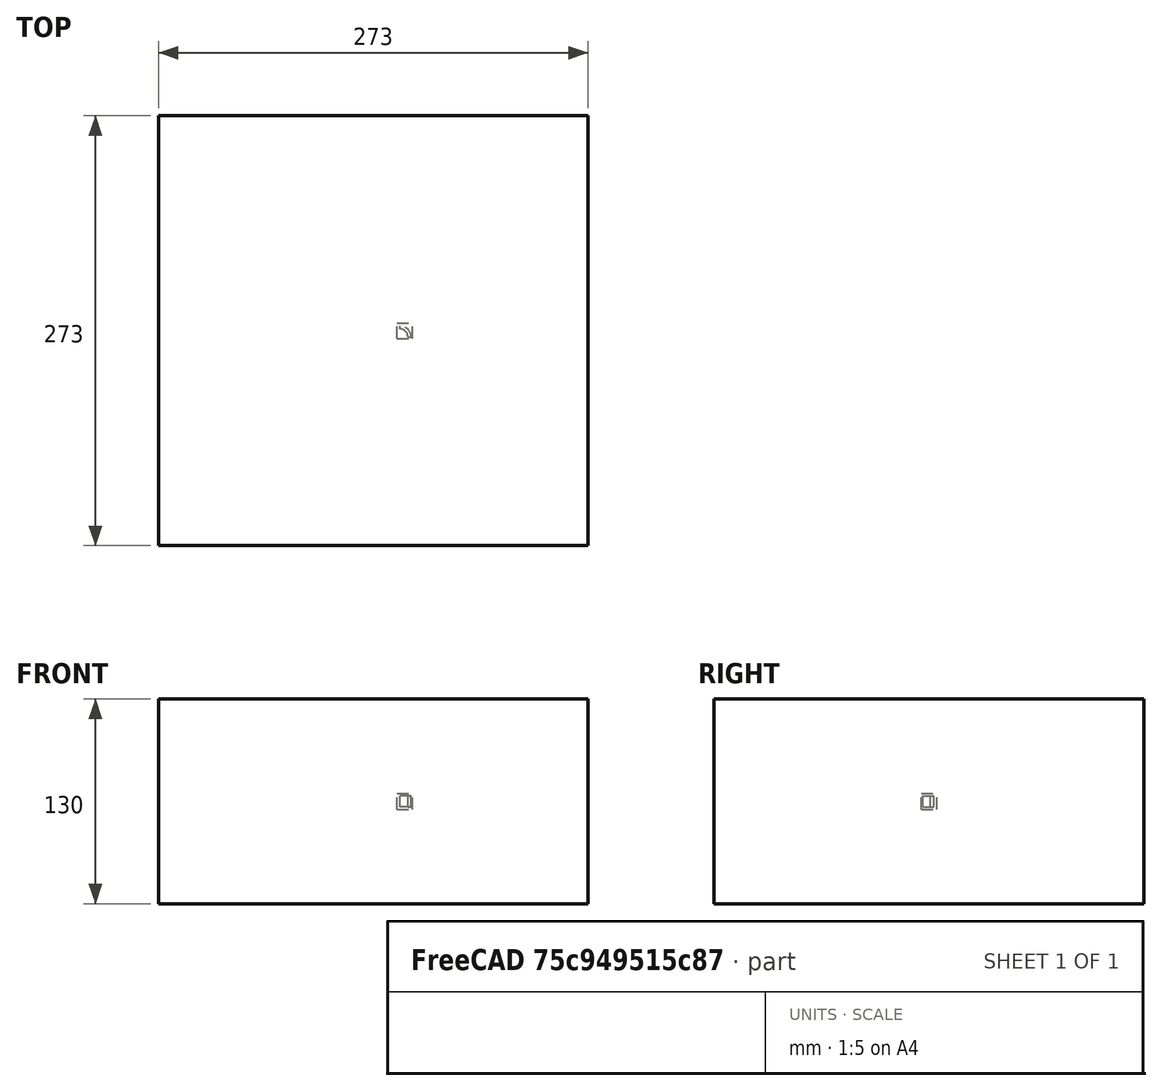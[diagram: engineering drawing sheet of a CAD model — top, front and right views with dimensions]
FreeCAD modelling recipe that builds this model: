
FCSTD DOCUMENT  (FreeCAD 0.20RUnknown)
Label: polarArray-container-d
License: All rights reserved
LicenseURL: http://en.wikipedia.org/wiki/All_rights_reserved
objects: App::DocumentObjectGroupPython×1251, Part::FeaturePython×4, App::Part×4
note: 3 computed .brp shape members not serialized (recipe doc carries the construction recipe); baked Part::Feature solids carry a one-line shape summary decoded from their .brp

FEATURE [App::DocumentObjectGroupPython] HALFPI  # scripted group (container) (typed FeaturePython)
  name = HALFPI
  value = pi/2.
FEATURE [App::DocumentObjectGroupPython] PI  # scripted group (container) (typed FeaturePython)
  name = PI
  value = 1.*pi
FEATURE [App::DocumentObjectGroupPython] TWOPI  # scripted group (container) (typed FeaturePython)
  name = TWOPI
  value = 2.*pi
FEATURE [App::DocumentObjectGroupPython] Constants  # scripted group (container) (typed FeaturePython)
  Group = -> [HALFPI,PI,TWOPI]
FEATURE [App::DocumentObjectGroupPython] Variables  # scripted group (container) (typed FeaturePython)
FEATURE [App::DocumentObjectGroupPython] Quantities  # scripted group (container) (typed FeaturePython)
FEATURE [App::DocumentObjectGroupPython] Isotopes  # scripted group (container) (typed FeaturePython)
FEATURE [App::DocumentObjectGroupPython] Elements  # scripted group (container) (typed FeaturePython)
FEATURE [App::DocumentObjectGroupPython] Matrix  # scripted group (container) (typed FeaturePython)
FEATURE [App::DocumentObjectGroupPython] Surfaces  # scripted group (container) (typed FeaturePython)
FEATURE [App::DocumentObjectGroupPython] Opticals  # scripted group (container) (typed FeaturePython)
  Group = -> [Matrix,Surfaces]
FEATURE [App::DocumentObjectGroupPython] G4Isotopes  # scripted group (container) (typed FeaturePython)
FEATURE [App::DocumentObjectGroupPython] H_element  # scripted group (container) (typed FeaturePython)
  Z = 1
  atom_value = 1.008
  formula = H
  name = H_element
FEATURE [App::DocumentObjectGroupPython] He_element  # scripted group (container) (typed FeaturePython)
  Z = 2
  atom_value = 4.0026
  formula = He
  name = He_element
FEATURE [App::DocumentObjectGroupPython] Li_element  # scripted group (container) (typed FeaturePython)
  Z = 3
  atom_value = 6.94
  formula = Li
  name = Li_element
FEATURE [App::DocumentObjectGroupPython] Be_element  # scripted group (container) (typed FeaturePython)
  Z = 4
  atom_value = 9.01218
  formula = Be
  name = Be_element
FEATURE [App::DocumentObjectGroupPython] B_element  # scripted group (container) (typed FeaturePython)
  Z = 5
  atom_value = 10.81
  formula = B
  name = B_element
FEATURE [App::DocumentObjectGroupPython] C_element  # scripted group (container) (typed FeaturePython)
  Z = 6
  atom_value = 12.011
  formula = C
  name = C_element
FEATURE [App::DocumentObjectGroupPython] N_element  # scripted group (container) (typed FeaturePython)
  Z = 7
  atom_value = 14.007
  formula = N
  name = N_element
FEATURE [App::DocumentObjectGroupPython] O_element  # scripted group (container) (typed FeaturePython)
  Z = 8
  atom_value = 15.999
  formula = O
  name = O_element
FEATURE [App::DocumentObjectGroupPython] F_element  # scripted group (container) (typed FeaturePython)
  Z = 9
  atom_value = 18.9984
  formula = F
  name = F_element
FEATURE [App::DocumentObjectGroupPython] Ne_element  # scripted group (container) (typed FeaturePython)
  Z = 10
  atom_value = 20.1797
  formula = Ne
  name = Ne_element
FEATURE [App::DocumentObjectGroupPython] Na_element  # scripted group (container) (typed FeaturePython)
  Z = 11
  atom_value = 22.9898
  formula = Na
  name = Na_element
FEATURE [App::DocumentObjectGroupPython] Mg_element  # scripted group (container) (typed FeaturePython)
  Z = 12
  atom_value = 24.305
  formula = Mg
  name = Mg_element
FEATURE [App::DocumentObjectGroupPython] Al_element  # scripted group (container) (typed FeaturePython)
  Z = 13
  atom_value = 26.9815
  formula = Al
  name = Al_element
FEATURE [App::DocumentObjectGroupPython] Si_element  # scripted group (container) (typed FeaturePython)
  Z = 14
  atom_value = 28.085
  formula = Si
  name = Si_element
FEATURE [App::DocumentObjectGroupPython] P_element  # scripted group (container) (typed FeaturePython)
  Z = 15
  atom_value = 30.9738
  formula = P
  name = P_element
FEATURE [App::DocumentObjectGroupPython] S_element  # scripted group (container) (typed FeaturePython)
  Z = 16
  atom_value = 32.06
  formula = S
  name = S_element
FEATURE [App::DocumentObjectGroupPython] Cl_element  # scripted group (container) (typed FeaturePython)
  Z = 17
  atom_value = 35.45
  formula = Cl
  name = Cl_element
FEATURE [App::DocumentObjectGroupPython] Ar_element  # scripted group (container) (typed FeaturePython)
  Z = 18
  atom_value = 39.95
  formula = Ar
  name = Ar_element
FEATURE [App::DocumentObjectGroupPython] K_element  # scripted group (container) (typed FeaturePython)
  Z = 19
  atom_value = 39.0983
  formula = K
  name = K_element
FEATURE [App::DocumentObjectGroupPython] Ca_element  # scripted group (container) (typed FeaturePython)
  Z = 20
  atom_value = 40.078
  formula = Ca
  name = Ca_element
FEATURE [App::DocumentObjectGroupPython] Sc_element  # scripted group (container) (typed FeaturePython)
  Z = 21
  atom_value = 44.9559
  formula = Sc
  name = Sc_element
FEATURE [App::DocumentObjectGroupPython] Ti_element  # scripted group (container) (typed FeaturePython)
  Z = 22
  atom_value = 47.867
  formula = Ti
  name = Ti_element
FEATURE [App::DocumentObjectGroupPython] V_element  # scripted group (container) (typed FeaturePython)
  Z = 23
  atom_value = 50.9415
  formula = V
  name = V_element
FEATURE [App::DocumentObjectGroupPython] Cr_element  # scripted group (container) (typed FeaturePython)
  Z = 24
  atom_value = 51.9961
  formula = Cr
  name = Cr_element
FEATURE [App::DocumentObjectGroupPython] Mn_element  # scripted group (container) (typed FeaturePython)
  Z = 25
  atom_value = 54.938
  formula = Mn
  name = Mn_element
FEATURE [App::DocumentObjectGroupPython] Fe_element  # scripted group (container) (typed FeaturePython)
  Z = 26
  atom_value = 55.845
  formula = Fe
  name = Fe_element
FEATURE [App::DocumentObjectGroupPython] Co_element  # scripted group (container) (typed FeaturePython)
  Z = 27
  atom_value = 58.9332
  formula = Co
  name = Co_element
FEATURE [App::DocumentObjectGroupPython] Ni_element  # scripted group (container) (typed FeaturePython)
  Z = 28
  atom_value = 58.6934
  formula = Ni
  name = Ni_element
FEATURE [App::DocumentObjectGroupPython] Cu_element  # scripted group (container) (typed FeaturePython)
  Z = 29
  atom_value = 63.546
  formula = Cu
  name = Cu_element
FEATURE [App::DocumentObjectGroupPython] Zn_element  # scripted group (container) (typed FeaturePython)
  Z = 30
  atom_value = 65.38
  formula = Zn
  name = Zn_element
FEATURE [App::DocumentObjectGroupPython] Ga_element  # scripted group (container) (typed FeaturePython)
  Z = 31
  atom_value = 69.723
  formula = Ga
  name = Ga_element
FEATURE [App::DocumentObjectGroupPython] Ge_element  # scripted group (container) (typed FeaturePython)
  Z = 32
  atom_value = 72.63
  formula = Ge
  name = Ge_element
FEATURE [App::DocumentObjectGroupPython] As_element  # scripted group (container) (typed FeaturePython)
  Z = 33
  atom_value = 74.9216
  formula = As
  name = As_element
FEATURE [App::DocumentObjectGroupPython] Se_element  # scripted group (container) (typed FeaturePython)
  Z = 34
  atom_value = 78.971
  formula = Se
  name = Se_element
FEATURE [App::DocumentObjectGroupPython] Br_element  # scripted group (container) (typed FeaturePython)
  Z = 35
  atom_value = 79.904
  formula = Br
  name = Br_element
FEATURE [App::DocumentObjectGroupPython] Kr_element  # scripted group (container) (typed FeaturePython)
  Z = 36
  atom_value = 83.798
  formula = Kr
  name = Kr_element
FEATURE [App::DocumentObjectGroupPython] Rb_element  # scripted group (container) (typed FeaturePython)
  Z = 37
  atom_value = 85.4678
  formula = Rb
  name = Rb_element
FEATURE [App::DocumentObjectGroupPython] Sr_element  # scripted group (container) (typed FeaturePython)
  Z = 38
  atom_value = 87.62
  formula = Sr
  name = Sr_element
FEATURE [App::DocumentObjectGroupPython] Y_element  # scripted group (container) (typed FeaturePython)
  Z = 39
  atom_value = 88.9058
  formula = Y
  name = Y_element
FEATURE [App::DocumentObjectGroupPython] Zr_element  # scripted group (container) (typed FeaturePython)
  Z = 40
  atom_value = 91.224
  formula = Zr
  name = Zr_element
FEATURE [App::DocumentObjectGroupPython] Nb_element  # scripted group (container) (typed FeaturePython)
  Z = 41
  atom_value = 92.9064
  formula = Nb
  name = Nb_element
FEATURE [App::DocumentObjectGroupPython] Mo_element  # scripted group (container) (typed FeaturePython)
  Z = 42
  atom_value = 95.95
  formula = Mo
  name = Mo_element
FEATURE [App::DocumentObjectGroupPython] Tc_element  # scripted group (container) (typed FeaturePython)
  Z = 43
  atom_value = 97
  formula = Tc
  name = Tc_element
FEATURE [App::DocumentObjectGroupPython] Ru_element  # scripted group (container) (typed FeaturePython)
  Z = 44
  atom_value = 101.07
  formula = Ru
  name = Ru_element
FEATURE [App::DocumentObjectGroupPython] Rh_element  # scripted group (container) (typed FeaturePython)
  Z = 45
  atom_value = 102.905
  formula = Rh
  name = Rh_element
FEATURE [App::DocumentObjectGroupPython] Pd_element  # scripted group (container) (typed FeaturePython)
  Z = 46
  atom_value = 106.42
  formula = Pd
  name = Pd_element
FEATURE [App::DocumentObjectGroupPython] Ag_element  # scripted group (container) (typed FeaturePython)
  Z = 47
  atom_value = 107.868
  formula = Ag
  name = Ag_element
FEATURE [App::DocumentObjectGroupPython] Cd_element  # scripted group (container) (typed FeaturePython)
  Z = 48
  atom_value = 112.414
  formula = Cd
  name = Cd_element
FEATURE [App::DocumentObjectGroupPython] In_element  # scripted group (container) (typed FeaturePython)
  Z = 49
  atom_value = 114.818
  formula = In
  name = In_element
FEATURE [App::DocumentObjectGroupPython] Sn_element  # scripted group (container) (typed FeaturePython)
  Z = 50
  atom_value = 118.71
  formula = Sn
  name = Sn_element
FEATURE [App::DocumentObjectGroupPython] Sb_element  # scripted group (container) (typed FeaturePython)
  Z = 51
  atom_value = 121.76
  formula = Sb
  name = Sb_element
FEATURE [App::DocumentObjectGroupPython] Te_element  # scripted group (container) (typed FeaturePython)
  Z = 52
  atom_value = 127.6
  formula = Te
  name = Te_element
FEATURE [App::DocumentObjectGroupPython] I_element  # scripted group (container) (typed FeaturePython)
  Z = 53
  atom_value = 126.904
  formula = I
  name = I_element
FEATURE [App::DocumentObjectGroupPython] Xe_element  # scripted group (container) (typed FeaturePython)
  Z = 54
  atom_value = 131.293
  formula = Xe
  name = Xe_element
FEATURE [App::DocumentObjectGroupPython] Cs_element  # scripted group (container) (typed FeaturePython)
  Z = 55
  atom_value = 132.905
  formula = Cs
  name = Cs_element
FEATURE [App::DocumentObjectGroupPython] Ba_element  # scripted group (container) (typed FeaturePython)
  Z = 56
  atom_value = 137.327
  formula = Ba
  name = Ba_element
FEATURE [App::DocumentObjectGroupPython] La_element  # scripted group (container) (typed FeaturePython)
  Z = 57
  atom_value = 138.905
  formula = La
  name = La_element
FEATURE [App::DocumentObjectGroupPython] Ce_element  # scripted group (container) (typed FeaturePython)
  Z = 58
  atom_value = 140.116
  formula = Ce
  name = Ce_element
FEATURE [App::DocumentObjectGroupPython] Pr_element  # scripted group (container) (typed FeaturePython)
  Z = 59
  atom_value = 140.908
  formula = Pr
  name = Pr_element
FEATURE [App::DocumentObjectGroupPython] Nd_element  # scripted group (container) (typed FeaturePython)
  Z = 60
  atom_value = 144.242
  formula = Nd
  name = Nd_element
FEATURE [App::DocumentObjectGroupPython] Pm_element  # scripted group (container) (typed FeaturePython)
  Z = 61
  atom_value = 145
  formula = Pm
  name = Pm_element
FEATURE [App::DocumentObjectGroupPython] Sm_element  # scripted group (container) (typed FeaturePython)
  Z = 62
  atom_value = 150.36
  formula = Sm
  name = Sm_element
FEATURE [App::DocumentObjectGroupPython] Eu_element  # scripted group (container) (typed FeaturePython)
  Z = 63
  atom_value = 151.964
  formula = Eu
  name = Eu_element
FEATURE [App::DocumentObjectGroupPython] Gd_element  # scripted group (container) (typed FeaturePython)
  Z = 64
  atom_value = 157.25
  formula = Gd
  name = Gd_element
FEATURE [App::DocumentObjectGroupPython] Tb_element  # scripted group (container) (typed FeaturePython)
  Z = 65
  atom_value = 158.925
  formula = Tb
  name = Tb_element
FEATURE [App::DocumentObjectGroupPython] Dy_element  # scripted group (container) (typed FeaturePython)
  Z = 66
  atom_value = 162.5
  formula = Dy
  name = Dy_element
FEATURE [App::DocumentObjectGroupPython] Ho_element  # scripted group (container) (typed FeaturePython)
  Z = 67
  atom_value = 164.93
  formula = Ho
  name = Ho_element
FEATURE [App::DocumentObjectGroupPython] Er_element  # scripted group (container) (typed FeaturePython)
  Z = 68
  atom_value = 167.259
  formula = Er
  name = Er_element
FEATURE [App::DocumentObjectGroupPython] Tm_element  # scripted group (container) (typed FeaturePython)
  Z = 69
  atom_value = 168.934
  formula = Tm
  name = Tm_element
FEATURE [App::DocumentObjectGroupPython] Yb_element  # scripted group (container) (typed FeaturePython)
  Z = 70
  atom_value = 173.045
  formula = Yb
  name = Yb_element
FEATURE [App::DocumentObjectGroupPython] Lu_element  # scripted group (container) (typed FeaturePython)
  Z = 71
  atom_value = 174.967
  formula = Lu
  name = Lu_element
FEATURE [App::DocumentObjectGroupPython] Hf_element  # scripted group (container) (typed FeaturePython)
  Z = 72
  atom_value = 178.49
  formula = Hf
  name = Hf_element
FEATURE [App::DocumentObjectGroupPython] Ta_element  # scripted group (container) (typed FeaturePython)
  Z = 73
  atom_value = 180.948
  formula = Ta
  name = Ta_element
FEATURE [App::DocumentObjectGroupPython] W_element  # scripted group (container) (typed FeaturePython)
  Z = 74
  atom_value = 183.84
  formula = W
  name = W_element
FEATURE [App::DocumentObjectGroupPython] Re_element  # scripted group (container) (typed FeaturePython)
  Z = 75
  atom_value = 186.207
  formula = Re
  name = Re_element
FEATURE [App::DocumentObjectGroupPython] Os_element  # scripted group (container) (typed FeaturePython)
  Z = 76
  atom_value = 190.23
  formula = Os
  name = Os_element
FEATURE [App::DocumentObjectGroupPython] Ir_element  # scripted group (container) (typed FeaturePython)
  Z = 77
  atom_value = 192.217
  formula = Ir
  name = Ir_element
FEATURE [App::DocumentObjectGroupPython] Pt_element  # scripted group (container) (typed FeaturePython)
  Z = 78
  atom_value = 195.084
  formula = Pt
  name = Pt_element
FEATURE [App::DocumentObjectGroupPython] Au_element  # scripted group (container) (typed FeaturePython)
  Z = 79
  atom_value = 196.967
  formula = Au
  name = Au_element
FEATURE [App::DocumentObjectGroupPython] Hg_element  # scripted group (container) (typed FeaturePython)
  Z = 80
  atom_value = 200.592
  formula = Hg
  name = Hg_element
FEATURE [App::DocumentObjectGroupPython] Tl_element  # scripted group (container) (typed FeaturePython)
  Z = 81
  atom_value = 204.38
  formula = Tl
  name = Tl_element
FEATURE [App::DocumentObjectGroupPython] Pb_element  # scripted group (container) (typed FeaturePython)
  Z = 82
  atom_value = 207.2
  formula = Pb
  name = Pb_element
FEATURE [App::DocumentObjectGroupPython] Bi_element  # scripted group (container) (typed FeaturePython)
  Z = 83
  atom_value = 208.98
  formula = Bi
  name = Bi_element
FEATURE [App::DocumentObjectGroupPython] Po_element  # scripted group (container) (typed FeaturePython)
  Z = 84
  atom_value = 209
  formula = Po
  name = Po_element
FEATURE [App::DocumentObjectGroupPython] At_element  # scripted group (container) (typed FeaturePython)
  Z = 85
  atom_value = 210
  formula = At
  name = At_element
FEATURE [App::DocumentObjectGroupPython] Rn_element  # scripted group (container) (typed FeaturePython)
  Z = 86
  atom_value = 222
  formula = Rn
  name = Rn_element
FEATURE [App::DocumentObjectGroupPython] Fr_element  # scripted group (container) (typed FeaturePython)
  Z = 87
  atom_value = 223
  formula = Fr
  name = Fr_element
FEATURE [App::DocumentObjectGroupPython] Ra_element  # scripted group (container) (typed FeaturePython)
  Z = 88
  atom_value = 226
  formula = Ra
  name = Ra_element
FEATURE [App::DocumentObjectGroupPython] Ac_element  # scripted group (container) (typed FeaturePython)
  Z = 89
  atom_value = 227
  formula = Ac
  name = Ac_element
FEATURE [App::DocumentObjectGroupPython] Th_element  # scripted group (container) (typed FeaturePython)
  Z = 90
  atom_value = 232.038
  formula = Th
  name = Th_element
FEATURE [App::DocumentObjectGroupPython] Pa_element  # scripted group (container) (typed FeaturePython)
  Z = 91
  atom_value = 231.036
  formula = Pa
  name = Pa_element
FEATURE [App::DocumentObjectGroupPython] U_element  # scripted group (container) (typed FeaturePython)
  Z = 92
  atom_value = 238.029
  formula = U
  name = U_element
FEATURE [App::DocumentObjectGroupPython] Np_element  # scripted group (container) (typed FeaturePython)
  Z = 93
  atom_value = 237
  formula = Np
  name = Np_element
FEATURE [App::DocumentObjectGroupPython] Pu_element  # scripted group (container) (typed FeaturePython)
  Z = 94
  atom_value = 244
  formula = Pu
  name = Pu_element
FEATURE [App::DocumentObjectGroupPython] Am_element  # scripted group (container) (typed FeaturePython)
  Z = 95
  atom_value = 243
  formula = Am
  name = Am_element
FEATURE [App::DocumentObjectGroupPython] Cm_element  # scripted group (container) (typed FeaturePython)
  Z = 96
  atom_value = 247
  formula = Cm
  name = Cm_element
FEATURE [App::DocumentObjectGroupPython] Bk_element  # scripted group (container) (typed FeaturePython)
  Z = 97
  atom_value = 247
  formula = Bk
  name = Bk_element
FEATURE [App::DocumentObjectGroupPython] Cf_element  # scripted group (container) (typed FeaturePython)
  Z = 98
  atom_value = 251
  formula = Cf
  name = Cf_element
FEATURE [App::DocumentObjectGroupPython] G4Elements  # scripted group (container) (typed FeaturePython)
  Group = -> [H_element,He_element,Li_element,Be_element,B_element,C_element,N_element,O_element,F_element,Ne_element,Na_element,Mg_element,Al_element,Si_element,P_element,S_element,Cl_element,Ar_element,K_element,Ca_element,Sc_element,Ti_element,V_element,Cr_element,Mn_element,Fe_element,Co_element,Ni_element,Cu_element,Zn_element,Ga_element,Ge_element,As_element,Se_element,Br_element,Kr_element,Rb_element,+61 more]
FEATURE [App::DocumentObjectGroupPython] H_element001  label="H_element : 0.101"  # scripted group (container) (typed FeaturePython)
  n = 0.101327
FEATURE [App::DocumentObjectGroupPython] C_element001  label="C_element : 0.775"  # scripted group (container) (typed FeaturePython)
  n = 0.7755
FEATURE [App::DocumentObjectGroupPython] N_element001  label="N_element : 0.035"  # scripted group (container) (typed FeaturePython)
  n = 0.035057
FEATURE [App::DocumentObjectGroupPython] O_element001  label="O_element : 0.052"  # scripted group (container) (typed FeaturePython)
  n = 0.0523159
FEATURE [App::DocumentObjectGroupPython] F_element001  label="F_element : 0.017"  # scripted group (container) (typed FeaturePython)
  n = 0.017422
FEATURE [App::DocumentObjectGroupPython] Ca_element001  label="Ca_element : 0.018"  # scripted group (container) (typed FeaturePython)
  n = 0.018378
FEATURE [App::DocumentObjectGroupPython] G4_A_150_TISSUE  label="G4_A-150_TISSUE"  # scripted group (container) (typed FeaturePython)
  Dunit = g/cm3
  Dvalue = 1.127
  Group = -> [H_element001,C_element001,N_element001,O_element001,F_element001,Ca_element001]
  conduct = 2
  density = 1
  expand = 3
  formula = G4_A-150_TISSUE
  name = G4_A-150_TISSUE
  specific = 4
FEATURE [App::DocumentObjectGroupPython] C_element002  label="C_element : 3"  # scripted group (container) (typed FeaturePython)
  n = 3
  ref = C_element
FEATURE [App::DocumentObjectGroupPython] H_element002  label="H_element : 6"  # scripted group (container) (typed FeaturePython)
  n = 6
  ref = H_element
FEATURE [App::DocumentObjectGroupPython] O_element002  label="O_element : 1"  # scripted group (container) (typed FeaturePython)
  n = 1
  ref = O_element
FEATURE [App::DocumentObjectGroupPython] G4_ACETONE  # scripted group (container) (typed FeaturePython)
  Dunit = g/cm3
  Dvalue = 0.7899
  Group = -> [C_element002,H_element002,O_element002]
  conduct = 2
  density = 1
  expand = 3
  formula = G4_ACETONE
  name = G4_ACETONE
  specific = 4
FEATURE [App::DocumentObjectGroupPython] C_element003  label="C_element : 2"  # scripted group (container) (typed FeaturePython)
  n = 2
  ref = C_element
FEATURE [App::DocumentObjectGroupPython] H_element003  label="H_element : 2"  # scripted group (container) (typed FeaturePython)
  n = 2
  ref = H_element
FEATURE [App::DocumentObjectGroupPython] G4_ACETYLENE  # scripted group (container) (typed FeaturePython)
  Dunit = g/cm3
  Dvalue = 0.0010967
  Group = -> [C_element003,H_element003]
  conduct = 2
  density = 1
  expand = 3
  formula = G4_ACETYLENE
  name = G4_ACETYLENE
  specific = 4
FEATURE [App::DocumentObjectGroupPython] C_element004  label="C_element : 5"  # scripted group (container) (typed FeaturePython)
  n = 5
  ref = C_element
FEATURE [App::DocumentObjectGroupPython] H_element004  label="H_element : 5"  # scripted group (container) (typed FeaturePython)
  n = 5
  ref = H_element
FEATURE [App::DocumentObjectGroupPython] N_element002  label="N_element : 5"  # scripted group (container) (typed FeaturePython)
  n = 5
  ref = N_element
FEATURE [App::DocumentObjectGroupPython] G4_ADENINE  # scripted group (container) (typed FeaturePython)
  Dunit = g/cm3
  Dvalue = 1.6
  Group = -> [C_element004,H_element004,N_element002]
  conduct = 2
  density = 1
  expand = 3
  formula = G4_ADENINE
  name = G4_ADENINE
  specific = 4
FEATURE [App::DocumentObjectGroupPython] H_element005  label="H_element : 0.114"  # scripted group (container) (typed FeaturePython)
  n = 0.114
FEATURE [App::DocumentObjectGroupPython] C_element005  label="C_element : 0.598"  # scripted group (container) (typed FeaturePython)
  n = 0.598
FEATURE [App::DocumentObjectGroupPython] N_element003  label="N_element : 0.007"  # scripted group (container) (typed FeaturePython)
  n = 0.007
FEATURE [App::DocumentObjectGroupPython] O_element003  label="O_element : 0.278"  # scripted group (container) (typed FeaturePython)
  n = 0.278
FEATURE [App::DocumentObjectGroupPython] Na_element001  label="Na_element : 0.001"  # scripted group (container) (typed FeaturePython)
  n = 0.001
FEATURE [App::DocumentObjectGroupPython] S_element001  label="S_element : 0.001"  # scripted group (container) (typed FeaturePython)
  n = 0.001
FEATURE [App::DocumentObjectGroupPython] Cl_element001  label="Cl_element : 0.001"  # scripted group (container) (typed FeaturePython)
  n = 0.001
FEATURE [App::DocumentObjectGroupPython] G4_ADIPOSE_TISSUE_ICRP  # scripted group (container) (typed FeaturePython)
  Dunit = g/cm3
  Dvalue = 0.95
  Group = -> [H_element005,C_element005,N_element003,O_element003,Na_element001,S_element001,Cl_element001]
  conduct = 2
  density = 1
  expand = 3
  formula = G4_ADIPOSE_TISSUE_ICRP
  name = G4_ADIPOSE_TISSUE_ICRP
  specific = 4
FEATURE [App::DocumentObjectGroupPython] C_element006  label="C_element : 0.000"  # scripted group (container) (typed FeaturePython)
  n = 0.000124
FEATURE [App::DocumentObjectGroupPython] N_element004  label="N_element : 0.755"  # scripted group (container) (typed FeaturePython)
  n = 0.755268
FEATURE [App::DocumentObjectGroupPython] O_element004  label="O_element : 0.232"  # scripted group (container) (typed FeaturePython)
  n = 0.231781
FEATURE [App::DocumentObjectGroupPython] Ar_element001  label="Ar_element : 0.013"  # scripted group (container) (typed FeaturePython)
  n = 0.012827
FEATURE [App::DocumentObjectGroupPython] G4_AIR  # scripted group (container) (typed FeaturePython)
  Dunit = g/cm3
  Dvalue = 0.00120479
  Group = -> [C_element006,N_element004,O_element004,Ar_element001]
  conduct = 2
  density = 1
  expand = 3
  formula = G4_AIR
  name = G4_AIR
  specific = 4
FEATURE [App::DocumentObjectGroupPython] C_element007  label="C_element : 006"  # scripted group (container) (typed FeaturePython)
  n = 3
  ref = C_element
FEATURE [App::DocumentObjectGroupPython] H_element006  label="H_element : 7"  # scripted group (container) (typed FeaturePython)
  n = 7
  ref = H_element
FEATURE [App::DocumentObjectGroupPython] N_element005  label="N_element : 1"  # scripted group (container) (typed FeaturePython)
  n = 1
  ref = N_element
FEATURE [App::DocumentObjectGroupPython] O_element005  label="O_element : 2"  # scripted group (container) (typed FeaturePython)
  n = 2
  ref = O_element
FEATURE [App::DocumentObjectGroupPython] G4_ALANINE  # scripted group (container) (typed FeaturePython)
  Dunit = g/cm3
  Dvalue = 1.42
  Group = -> [C_element007,H_element006,N_element005,O_element005]
  conduct = 2
  density = 1
  expand = 3
  formula = G4_ALANINE
  name = G4_ALANINE
  specific = 4
FEATURE [App::DocumentObjectGroupPython] Al_element001  label="Al_element : 2"  # scripted group (container) (typed FeaturePython)
  n = 2
  ref = Al_element
FEATURE [App::DocumentObjectGroupPython] O_element006  label="O_element : 3"  # scripted group (container) (typed FeaturePython)
  n = 3
  ref = O_element
FEATURE [App::DocumentObjectGroupPython] G4_ALUMINUM_OXIDE  # scripted group (container) (typed FeaturePython)
  Dunit = g/cm3
  Dvalue = 3.97
  Group = -> [Al_element001,O_element006]
  conduct = 2
  density = 1
  expand = 3
  formula = G4_ALUMINUM_OXIDE
  name = G4_ALUMINUM_OXIDE
  specific = 4
FEATURE [App::DocumentObjectGroupPython] H_element007  label="H_element : 0.106"  # scripted group (container) (typed FeaturePython)
  n = 0.10593
FEATURE [App::DocumentObjectGroupPython] C_element008  label="C_element : 0.789"  # scripted group (container) (typed FeaturePython)
  n = 0.788974
FEATURE [App::DocumentObjectGroupPython] O_element007  label="O_element : 0.105"  # scripted group (container) (typed FeaturePython)
  n = 0.105096
FEATURE [App::DocumentObjectGroupPython] G4_AMBER  # scripted group (container) (typed FeaturePython)
  Dunit = g/cm3
  Dvalue = 1.1
  Group = -> [H_element007,C_element008,O_element007]
  conduct = 2
  density = 1
  expand = 3
  formula = G4_AMBER
  name = G4_AMBER
  specific = 4
FEATURE [App::DocumentObjectGroupPython] N_element006  label="N_element : 006"  # scripted group (container) (typed FeaturePython)
  n = 1
  ref = N_element
FEATURE [App::DocumentObjectGroupPython] H_element008  label="H_element : 3"  # scripted group (container) (typed FeaturePython)
  n = 3
  ref = H_element
FEATURE [App::DocumentObjectGroupPython] G4_AMMONIA  # scripted group (container) (typed FeaturePython)
  Dunit = g/cm3
  Dvalue = 0.000826019
  Group = -> [N_element006,H_element008]
  conduct = 2
  density = 1
  expand = 3
  formula = G4_AMMONIA
  name = G4_AMMONIA
  specific = 4
FEATURE [App::DocumentObjectGroupPython] C_element009  label="C_element : 6"  # scripted group (container) (typed FeaturePython)
  n = 6
  ref = C_element
FEATURE [App::DocumentObjectGroupPython] H_element009  label="H_element : 008"  # scripted group (container) (typed FeaturePython)
  n = 7
  ref = H_element
FEATURE [App::DocumentObjectGroupPython] N_element007  label="N_element : 007"  # scripted group (container) (typed FeaturePython)
  n = 1
  ref = N_element
FEATURE [App::DocumentObjectGroupPython] G4_ANILINE  # scripted group (container) (typed FeaturePython)
  Dunit = g/cm3
  Dvalue = 1.0235
  Group = -> [C_element009,H_element009,N_element007]
  conduct = 2
  density = 1
  expand = 3
  formula = G4_ANILINE
  name = G4_ANILINE
  specific = 4
FEATURE [App::DocumentObjectGroupPython] C_element010  label="C_element : 14"  # scripted group (container) (typed FeaturePython)
  n = 14
  ref = C_element
FEATURE [App::DocumentObjectGroupPython] H_element010  label="H_element : 10"  # scripted group (container) (typed FeaturePython)
  n = 10
  ref = H_element
FEATURE [App::DocumentObjectGroupPython] G4_ANTHRACENE  # scripted group (container) (typed FeaturePython)
  Dunit = g/cm3
  Dvalue = 1.283
  Group = -> [C_element010,H_element010]
  conduct = 2
  density = 1
  expand = 3
  formula = G4_ANTHRACENE
  name = G4_ANTHRACENE
  specific = 4
FEATURE [App::DocumentObjectGroupPython] H_element011  label="H_element : 0.065"  # scripted group (container) (typed FeaturePython)
  n = 0.0654709
FEATURE [App::DocumentObjectGroupPython] C_element011  label="C_element : 0.537"  # scripted group (container) (typed FeaturePython)
  n = 0.536944
FEATURE [App::DocumentObjectGroupPython] N_element008  label="N_element : 0.021"  # scripted group (container) (typed FeaturePython)
  n = 0.0215
FEATURE [App::DocumentObjectGroupPython] O_element008  label="O_element : 0.032"  # scripted group (container) (typed FeaturePython)
  n = 0.032085
FEATURE [App::DocumentObjectGroupPython] F_element002  label="F_element : 0.167"  # scripted group (container) (typed FeaturePython)
  n = 0.167411
FEATURE [App::DocumentObjectGroupPython] Ca_element002  label="Ca_element : 0.177"  # scripted group (container) (typed FeaturePython)
  n = 0.176589
FEATURE [App::DocumentObjectGroupPython] G4_B_100_BONE  label="G4_B-100_BONE"  # scripted group (container) (typed FeaturePython)
  Dunit = g/cm3
  Dvalue = 1.45
  Group = -> [H_element011,C_element011,N_element008,O_element008,F_element002,Ca_element002]
  conduct = 2
  density = 1
  expand = 3
  formula = G4_B-100_BONE
  name = G4_B-100_BONE
  specific = 4
FEATURE [App::DocumentObjectGroupPython] H_element012  label="H_element : 0.057"  # scripted group (container) (typed FeaturePython)
  n = 0.057441
FEATURE [App::DocumentObjectGroupPython] C_element012  label="C_element : 0.790"  # scripted group (container) (typed FeaturePython)
  n = 0.774591
FEATURE [App::DocumentObjectGroupPython] O_element009  label="O_element : 0.168"  # scripted group (container) (typed FeaturePython)
  n = 0.167968
FEATURE [App::DocumentObjectGroupPython] G4_BAKELITE  # scripted group (container) (typed FeaturePython)
  Dunit = g/cm3
  Dvalue = 1.25
  Group = -> [H_element012,C_element012,O_element009]
  conduct = 2
  density = 1
  expand = 3
  formula = G4_BAKELITE
  name = G4_BAKELITE
  specific = 4
FEATURE [App::DocumentObjectGroupPython] Ba_element001  label="Ba_element : 1"  # scripted group (container) (typed FeaturePython)
  n = 1
  ref = Ba_element
FEATURE [App::DocumentObjectGroupPython] F_element003  label="F_element : 2"  # scripted group (container) (typed FeaturePython)
  n = 2
  ref = F_element
FEATURE [App::DocumentObjectGroupPython] G4_BARIUM_FLUORIDE  # scripted group (container) (typed FeaturePython)
  Dunit = g/cm3
  Dvalue = 4.89
  Group = -> [Ba_element001,F_element003]
  conduct = 2
  density = 1
  expand = 3
  formula = G4_BARIUM_FLUORIDE
  name = G4_BARIUM_FLUORIDE
  specific = 4
FEATURE [App::DocumentObjectGroupPython] Ba_element002  label="Ba_element : 002"  # scripted group (container) (typed FeaturePython)
  n = 1
  ref = Ba_element
FEATURE [App::DocumentObjectGroupPython] S_element002  label="S_element : 1"  # scripted group (container) (typed FeaturePython)
  n = 1
  ref = S_element
FEATURE [App::DocumentObjectGroupPython] O_element010  label="O_element : 4"  # scripted group (container) (typed FeaturePython)
  n = 4
  ref = O_element
FEATURE [App::DocumentObjectGroupPython] G4_BARIUM_SULFATE  # scripted group (container) (typed FeaturePython)
  Dunit = g/cm3
  Dvalue = 4.5
  Group = -> [Ba_element002,S_element002,O_element010]
  conduct = 2
  density = 1
  expand = 3
  formula = G4_BARIUM_SULFATE
  name = G4_BARIUM_SULFATE
  specific = 4
FEATURE [App::DocumentObjectGroupPython] C_element013  label="C_element : 007"  # scripted group (container) (typed FeaturePython)
  n = 6
  ref = C_element
FEATURE [App::DocumentObjectGroupPython] H_element013  label="H_element : 009"  # scripted group (container) (typed FeaturePython)
  n = 6
  ref = H_element
FEATURE [App::DocumentObjectGroupPython] G4_BENZENE  # scripted group (container) (typed FeaturePython)
  Dunit = g/cm3
  Dvalue = 0.87865
  Group = -> [C_element013,H_element013]
  conduct = 2
  density = 1
  expand = 3
  formula = G4_BENZENE
  name = G4_BENZENE
  specific = 4
FEATURE [App::DocumentObjectGroupPython] Be_element001  label="Be_element : 1"  # scripted group (container) (typed FeaturePython)
  n = 1
  ref = Be_element
FEATURE [App::DocumentObjectGroupPython] O_element011  label="O_element : 005"  # scripted group (container) (typed FeaturePython)
  n = 1
  ref = O_element
FEATURE [App::DocumentObjectGroupPython] G4_BERYLLIUM_OXIDE  # scripted group (container) (typed FeaturePython)
  Dunit = g/cm3
  Dvalue = 3.01
  Group = -> [Be_element001,O_element011]
  conduct = 2
  density = 1
  expand = 3
  formula = G4_BERYLLIUM_OXIDE
  name = G4_BERYLLIUM_OXIDE
  specific = 4
FEATURE [App::DocumentObjectGroupPython] Bi_element001  label="Bi_element : 4"  # scripted group (container) (typed FeaturePython)
  n = 4
  ref = Bi_element
FEATURE [App::DocumentObjectGroupPython] Ge_element001  label="Ge_element : 3"  # scripted group (container) (typed FeaturePython)
  n = 3
  ref = Ge_element
FEATURE [App::DocumentObjectGroupPython] O_element012  label="O_element : 12"  # scripted group (container) (typed FeaturePython)
  n = 12
  ref = O_element
FEATURE [App::DocumentObjectGroupPython] G4_BGO  # scripted group (container) (typed FeaturePython)
  Dunit = g/cm3
  Dvalue = 7.13
  Group = -> [Bi_element001,Ge_element001,O_element012]
  conduct = 2
  density = 1
  expand = 3
  formula = G4_BGO
  name = G4_BGO
  specific = 4
FEATURE [App::DocumentObjectGroupPython] H_element014  label="H_element : 0.102"  # scripted group (container) (typed FeaturePython)
  n = 0.102
FEATURE [App::DocumentObjectGroupPython] C_element014  label="C_element : 0.110"  # scripted group (container) (typed FeaturePython)
  n = 0.11
FEATURE [App::DocumentObjectGroupPython] N_element009  label="N_element : 0.033"  # scripted group (container) (typed FeaturePython)
  n = 0.033
FEATURE [App::DocumentObjectGroupPython] O_element013  label="O_element : 0.745"  # scripted group (container) (typed FeaturePython)
  n = 0.745
FEATURE [App::DocumentObjectGroupPython] Na_element002  label="Na_element : 0.002"  # scripted group (container) (typed FeaturePython)
  n = 0.001
FEATURE [App::DocumentObjectGroupPython] P_element001  label="P_element : 0.001"  # scripted group (container) (typed FeaturePython)
  n = 0.001
FEATURE [App::DocumentObjectGroupPython] S_element003  label="S_element : 0.002"  # scripted group (container) (typed FeaturePython)
  n = 0.002
FEATURE [App::DocumentObjectGroupPython] Cl_element002  label="Cl_element : 0.003"  # scripted group (container) (typed FeaturePython)
  n = 0.003
FEATURE [App::DocumentObjectGroupPython] K_element001  label="K_element : 0.002"  # scripted group (container) (typed FeaturePython)
  n = 0.002
FEATURE [App::DocumentObjectGroupPython] Fe_element001  label="Fe_element : 0.001"  # scripted group (container) (typed FeaturePython)
  n = 0.001
FEATURE [App::DocumentObjectGroupPython] G4_BLOOD_ICRP  # scripted group (container) (typed FeaturePython)
  Dunit = g/cm3
  Dvalue = 1.06
  Group = -> [H_element014,C_element014,N_element009,O_element013,Na_element002,P_element001,S_element003,Cl_element002,K_element001,Fe_element001]
  conduct = 2
  density = 1
  expand = 3
  formula = G4_BLOOD_ICRP
  name = G4_BLOOD_ICRP
  specific = 4
FEATURE [App::DocumentObjectGroupPython] H_element015  label="H_element : 0.064"  # scripted group (container) (typed FeaturePython)
  n = 0.064
FEATURE [App::DocumentObjectGroupPython] C_element015  label="C_element : 0.278"  # scripted group (container) (typed FeaturePython)
  n = 0.278
FEATURE [App::DocumentObjectGroupPython] N_element010  label="N_element : 0.027"  # scripted group (container) (typed FeaturePython)
  n = 0.027
FEATURE [App::DocumentObjectGroupPython] O_element014  label="O_element : 0.410"  # scripted group (container) (typed FeaturePython)
  n = 0.41
FEATURE [App::DocumentObjectGroupPython] Mg_element001  label="Mg_element : 0.002"  # scripted group (container) (typed FeaturePython)
  n = 0.002
FEATURE [App::DocumentObjectGroupPython] P_element002  label="P_element : 0.070"  # scripted group (container) (typed FeaturePython)
  n = 0.07
FEATURE [App::DocumentObjectGroupPython] S_element004  label="S_element : 0.003"  # scripted group (container) (typed FeaturePython)
  n = 0.002
FEATURE [App::DocumentObjectGroupPython] Ca_element003  label="Ca_element : 0.147"  # scripted group (container) (typed FeaturePython)
  n = 0.147
FEATURE [App::DocumentObjectGroupPython] G4_BONE_COMPACT_ICRU  # scripted group (container) (typed FeaturePython)
  Dunit = g/cm3
  Dvalue = 1.85
  Group = -> [H_element015,C_element015,N_element010,O_element014,Mg_element001,P_element002,S_element004,Ca_element003]
  conduct = 2
  density = 1
  expand = 3
  formula = G4_BONE_COMPACT_ICRU
  name = G4_BONE_COMPACT_ICRU
  specific = 4
FEATURE [App::DocumentObjectGroupPython] H_element016  label="H_element : 0.034"  # scripted group (container) (typed FeaturePython)
  n = 0.034
FEATURE [App::DocumentObjectGroupPython] C_element016  label="C_element : 0.155"  # scripted group (container) (typed FeaturePython)
  n = 0.155
FEATURE [App::DocumentObjectGroupPython] N_element011  label="N_element : 0.042"  # scripted group (container) (typed FeaturePython)
  n = 0.042
FEATURE [App::DocumentObjectGroupPython] O_element015  label="O_element : 0.435"  # scripted group (container) (typed FeaturePython)
  n = 0.435
FEATURE [App::DocumentObjectGroupPython] Na_element003  label="Na_element : 0.003"  # scripted group (container) (typed FeaturePython)
  n = 0.001
FEATURE [App::DocumentObjectGroupPython] Mg_element002  label="Mg_element : 0.003"  # scripted group (container) (typed FeaturePython)
  n = 0.002
FEATURE [App::DocumentObjectGroupPython] P_element003  label="P_element : 0.103"  # scripted group (container) (typed FeaturePython)
  n = 0.103
FEATURE [App::DocumentObjectGroupPython] S_element005  label="S_element : 0.004"  # scripted group (container) (typed FeaturePython)
  n = 0.003
FEATURE [App::DocumentObjectGroupPython] Ca_element004  label="Ca_element : 0.225"  # scripted group (container) (typed FeaturePython)
  n = 0.225
FEATURE [App::DocumentObjectGroupPython] G4_BONE_CORTICAL_ICRP  # scripted group (container) (typed FeaturePython)
  Dunit = g/cm3
  Dvalue = 1.92
  Group = -> [H_element016,C_element016,N_element011,O_element015,Na_element003,Mg_element002,P_element003,S_element005,Ca_element004]
  conduct = 2
  density = 1
  expand = 3
  formula = G4_BONE_CORTICAL_ICRP
  name = G4_BONE_CORTICAL_ICRP
  specific = 4
FEATURE [App::DocumentObjectGroupPython] B_element001  label="B_element : 4"  # scripted group (container) (typed FeaturePython)
  n = 4
  ref = B_element
FEATURE [App::DocumentObjectGroupPython] C_element017  label="C_element : 1"  # scripted group (container) (typed FeaturePython)
  n = 1
  ref = C_element
FEATURE [App::DocumentObjectGroupPython] G4_BORON_CARBIDE  # scripted group (container) (typed FeaturePython)
  Dunit = g/cm3
  Dvalue = 2.52
  Group = -> [B_element001,C_element017]
  conduct = 2
  density = 1
  expand = 3
  formula = G4_BORON_CARBIDE
  name = G4_BORON_CARBIDE
  specific = 4
FEATURE [App::DocumentObjectGroupPython] B_element002  label="B_element : 2"  # scripted group (container) (typed FeaturePython)
  n = 2
  ref = B_element
FEATURE [App::DocumentObjectGroupPython] O_element016  label="O_element : 006"  # scripted group (container) (typed FeaturePython)
  n = 3
  ref = O_element
FEATURE [App::DocumentObjectGroupPython] G4_BORON_OXIDE  # scripted group (container) (typed FeaturePython)
  Dunit = g/cm3
  Dvalue = 1.812
  Group = -> [B_element002,O_element016]
  conduct = 2
  density = 1
  expand = 3
  formula = G4_BORON_OXIDE
  name = G4_BORON_OXIDE
  specific = 4
FEATURE [App::DocumentObjectGroupPython] H_element017  label="H_element : 0.107"  # scripted group (container) (typed FeaturePython)
  n = 0.107
FEATURE [App::DocumentObjectGroupPython] C_element018  label="C_element : 0.145"  # scripted group (container) (typed FeaturePython)
  n = 0.145
FEATURE [App::DocumentObjectGroupPython] N_element012  label="N_element : 0.022"  # scripted group (container) (typed FeaturePython)
  n = 0.022
FEATURE [App::DocumentObjectGroupPython] O_element017  label="O_element : 0.712"  # scripted group (container) (typed FeaturePython)
  n = 0.712
FEATURE [App::DocumentObjectGroupPython] Na_element004  label="Na_element : 0.004"  # scripted group (container) (typed FeaturePython)
  n = 0.002
FEATURE [App::DocumentObjectGroupPython] P_element004  label="P_element : 0.004"  # scripted group (container) (typed FeaturePython)
  n = 0.004
FEATURE [App::DocumentObjectGroupPython] S_element006  label="S_element : 0.005"  # scripted group (container) (typed FeaturePython)
  n = 0.002
FEATURE [App::DocumentObjectGroupPython] Cl_element003  label="Cl_element : 0.004"  # scripted group (container) (typed FeaturePython)
  n = 0.003
FEATURE [App::DocumentObjectGroupPython] K_element002  label="K_element : 0.003"  # scripted group (container) (typed FeaturePython)
  n = 0.003
FEATURE [App::DocumentObjectGroupPython] G4_BRAIN_ICRP  # scripted group (container) (typed FeaturePython)
  Dunit = g/cm3
  Dvalue = 1.04
  Group = -> [H_element017,C_element018,N_element012,O_element017,Na_element004,P_element004,S_element006,Cl_element003,K_element002]
  conduct = 2
  density = 1
  expand = 3
  formula = G4_BRAIN_ICRP
  name = G4_BRAIN_ICRP
  specific = 4
FEATURE [App::DocumentObjectGroupPython] C_element019  label="C_element : 4"  # scripted group (container) (typed FeaturePython)
  n = 4
  ref = C_element
FEATURE [App::DocumentObjectGroupPython] H_element018  label="H_element : 010"  # scripted group (container) (typed FeaturePython)
  n = 10
  ref = H_element
FEATURE [App::DocumentObjectGroupPython] G4_BUTANE  # scripted group (container) (typed FeaturePython)
  Dunit = g/cm3
  Dvalue = 0.00249343
  Group = -> [C_element019,H_element018]
  conduct = 2
  density = 1
  expand = 3
  formula = G4_BUTANE
  name = G4_BUTANE
  specific = 4
FEATURE [App::DocumentObjectGroupPython] C_element020  label="C_element : 008"  # scripted group (container) (typed FeaturePython)
  n = 4
  ref = C_element
FEATURE [App::DocumentObjectGroupPython] H_element019  label="H_element : 011"  # scripted group (container) (typed FeaturePython)
  n = 10
  ref = H_element
FEATURE [App::DocumentObjectGroupPython] O_element018  label="O_element : 007"  # scripted group (container) (typed FeaturePython)
  n = 1
  ref = O_element
FEATURE [App::DocumentObjectGroupPython] G4_N_BUTYL_ALCOHOL  label="G4_N-BUTYL_ALCOHOL"  # scripted group (container) (typed FeaturePython)
  Dunit = g/cm3
  Dvalue = 0.8098
  Group = -> [C_element020,H_element019,O_element018]
  conduct = 2
  density = 1
  expand = 3
  formula = G4_N-BUTYL_ALCOHOL
  name = G4_N-BUTYL_ALCOHOL
  specific = 4
FEATURE [App::DocumentObjectGroupPython] H_element020  label="H_element : 0.025"  # scripted group (container) (typed FeaturePython)
  n = 0.02468
FEATURE [App::DocumentObjectGroupPython] C_element021  label="C_element : 0.502"  # scripted group (container) (typed FeaturePython)
  n = 0.501611
FEATURE [App::DocumentObjectGroupPython] O_element019  label="O_element : 0.005"  # scripted group (container) (typed FeaturePython)
  n = 0.004527
FEATURE [App::DocumentObjectGroupPython] F_element004  label="F_element : 0.465"  # scripted group (container) (typed FeaturePython)
  n = 0.465209
FEATURE [App::DocumentObjectGroupPython] Si_element001  label="Si_element : 0.004"  # scripted group (container) (typed FeaturePython)
  n = 0.003973
FEATURE [App::DocumentObjectGroupPython] G4_C_552  label="G4_C-552"  # scripted group (container) (typed FeaturePython)
  Dunit = g/cm3
  Dvalue = 1.76
  Group = -> [H_element020,C_element021,O_element019,F_element004,Si_element001]
  conduct = 2
  density = 1
  expand = 3
  formula = G4_C-552
  name = G4_C-552
  specific = 4
FEATURE [App::DocumentObjectGroupPython] Cd_element001  label="Cd_element : 1"  # scripted group (container) (typed FeaturePython)
  n = 1
  ref = Cd_element
FEATURE [App::DocumentObjectGroupPython] Te_element001  label="Te_element : 1"  # scripted group (container) (typed FeaturePython)
  n = 1
  ref = Te_element
FEATURE [App::DocumentObjectGroupPython] G4_CADMIUM_TELLURIDE  # scripted group (container) (typed FeaturePython)
  Dunit = g/cm3
  Dvalue = 6.2
  Group = -> [Cd_element001,Te_element001]
  conduct = 2
  density = 1
  expand = 3
  formula = G4_CADMIUM_TELLURIDE
  name = G4_CADMIUM_TELLURIDE
  specific = 4
FEATURE [App::DocumentObjectGroupPython] Cd_element002  label="Cd_element : 002"  # scripted group (container) (typed FeaturePython)
  n = 1
  ref = Cd_element
FEATURE [App::DocumentObjectGroupPython] W_element001  label="W_element : 1"  # scripted group (container) (typed FeaturePython)
  n = 1
  ref = W_element
FEATURE [App::DocumentObjectGroupPython] O_element020  label="O_element : 008"  # scripted group (container) (typed FeaturePython)
  n = 4
  ref = O_element
FEATURE [App::DocumentObjectGroupPython] G4_CADMIUM_TUNGSTATE  # scripted group (container) (typed FeaturePython)
  Dunit = g/cm3
  Dvalue = 7.9
  Group = -> [Cd_element002,W_element001,O_element020]
  conduct = 2
  density = 1
  expand = 3
  formula = G4_CADMIUM_TUNGSTATE
  name = G4_CADMIUM_TUNGSTATE
  specific = 4
FEATURE [App::DocumentObjectGroupPython] Ca_element005  label="Ca_element : 1"  # scripted group (container) (typed FeaturePython)
  n = 1
  ref = Ca_element
FEATURE [App::DocumentObjectGroupPython] C_element022  label="C_element : 009"  # scripted group (container) (typed FeaturePython)
  n = 1
  ref = C_element
FEATURE [App::DocumentObjectGroupPython] O_element021  label="O_element : 009"  # scripted group (container) (typed FeaturePython)
  n = 3
  ref = O_element
FEATURE [App::DocumentObjectGroupPython] G4_CALCIUM_CARBONATE  # scripted group (container) (typed FeaturePython)
  Dunit = g/cm3
  Dvalue = 2.8
  Group = -> [Ca_element005,C_element022,O_element021]
  conduct = 2
  density = 1
  expand = 3
  formula = G4_CALCIUM_CARBONATE
  name = G4_CALCIUM_CARBONATE
  specific = 4
FEATURE [App::DocumentObjectGroupPython] Ca_element006  label="Ca_element : 002"  # scripted group (container) (typed FeaturePython)
  n = 1
  ref = Ca_element
FEATURE [App::DocumentObjectGroupPython] F_element005  label="F_element : 003"  # scripted group (container) (typed FeaturePython)
  n = 2
  ref = F_element
FEATURE [App::DocumentObjectGroupPython] G4_CALCIUM_FLUORIDE  # scripted group (container) (typed FeaturePython)
  Dunit = g/cm3
  Dvalue = 3.18
  Group = -> [Ca_element006,F_element005]
  conduct = 2
  density = 1
  expand = 3
  formula = G4_CALCIUM_FLUORIDE
  name = G4_CALCIUM_FLUORIDE
  specific = 4
FEATURE [App::DocumentObjectGroupPython] Ca_element007  label="Ca_element : 003"  # scripted group (container) (typed FeaturePython)
  n = 1
  ref = Ca_element
FEATURE [App::DocumentObjectGroupPython] O_element022  label="O_element : 010"  # scripted group (container) (typed FeaturePython)
  n = 1
  ref = O_element
FEATURE [App::DocumentObjectGroupPython] G4_CALCIUM_OXIDE  # scripted group (container) (typed FeaturePython)
  Dunit = g/cm3
  Dvalue = 3.3
  Group = -> [Ca_element007,O_element022]
  conduct = 2
  density = 1
  expand = 3
  formula = G4_CALCIUM_OXIDE
  name = G4_CALCIUM_OXIDE
  specific = 4
FEATURE [App::DocumentObjectGroupPython] Ca_element008  label="Ca_element : 004"  # scripted group (container) (typed FeaturePython)
  n = 1
  ref = Ca_element
FEATURE [App::DocumentObjectGroupPython] S_element007  label="S_element : 002"  # scripted group (container) (typed FeaturePython)
  n = 1
  ref = S_element
FEATURE [App::DocumentObjectGroupPython] O_element023  label="O_element : 011"  # scripted group (container) (typed FeaturePython)
  n = 4
  ref = O_element
FEATURE [App::DocumentObjectGroupPython] G4_CALCIUM_SULFATE  # scripted group (container) (typed FeaturePython)
  Dunit = g/cm3
  Dvalue = 2.96
  Group = -> [Ca_element008,S_element007,O_element023]
  conduct = 2
  density = 1
  expand = 3
  formula = G4_CALCIUM_SULFATE
  name = G4_CALCIUM_SULFATE
  specific = 4
FEATURE [App::DocumentObjectGroupPython] Ca_element009  label="Ca_element : 005"  # scripted group (container) (typed FeaturePython)
  n = 1
  ref = Ca_element
FEATURE [App::DocumentObjectGroupPython] W_element002  label="W_element : 002"  # scripted group (container) (typed FeaturePython)
  n = 1
  ref = W_element
FEATURE [App::DocumentObjectGroupPython] O_element024  label="O_element : 012"  # scripted group (container) (typed FeaturePython)
  n = 4
  ref = O_element
FEATURE [App::DocumentObjectGroupPython] G4_CALCIUM_TUNGSTATE  # scripted group (container) (typed FeaturePython)
  Dunit = g/cm3
  Dvalue = 6.062
  Group = -> [Ca_element009,W_element002,O_element024]
  conduct = 2
  density = 1
  expand = 3
  formula = G4_CALCIUM_TUNGSTATE
  name = G4_CALCIUM_TUNGSTATE
  specific = 4
FEATURE [App::DocumentObjectGroupPython] C_element023  label="C_element : 010"  # scripted group (container) (typed FeaturePython)
  n = 1
  ref = C_element
FEATURE [App::DocumentObjectGroupPython] O_element025  label="O_element : 013"  # scripted group (container) (typed FeaturePython)
  n = 2
  ref = O_element
FEATURE [App::DocumentObjectGroupPython] G4_CARBON_DIOXIDE  # scripted group (container) (typed FeaturePython)
  Dunit = g/cm3
  Dvalue = 0.00184212
  Group = -> [C_element023,O_element025]
  conduct = 2
  density = 1
  expand = 3
  formula = G4_CARBON_DIOXIDE
  name = G4_CARBON_DIOXIDE
  specific = 4
FEATURE [App::DocumentObjectGroupPython] C_element024  label="C_element : 011"  # scripted group (container) (typed FeaturePython)
  n = 1
  ref = C_element
FEATURE [App::DocumentObjectGroupPython] Cl_element004  label="Cl_element : 4"  # scripted group (container) (typed FeaturePython)
  n = 4
  ref = Cl_element
FEATURE [App::DocumentObjectGroupPython] G4_CARBON_TETRACHLORIDE  # scripted group (container) (typed FeaturePython)
  Dunit = g/cm3
  Dvalue = 1.594
  Group = -> [C_element024,Cl_element004]
  conduct = 2
  density = 1
  expand = 3
  formula = G4_CARBON_TETRACHLORIDE
  name = G4_CARBON_TETRACHLORIDE
  specific = 4
FEATURE [App::DocumentObjectGroupPython] C_element025  label="C_element : 012"  # scripted group (container) (typed FeaturePython)
  n = 6
  ref = C_element
FEATURE [App::DocumentObjectGroupPython] H_element021  label="H_element : 012"  # scripted group (container) (typed FeaturePython)
  n = 10
  ref = H_element
FEATURE [App::DocumentObjectGroupPython] O_element026  label="O_element : 5"  # scripted group (container) (typed FeaturePython)
  n = 5
  ref = O_element
FEATURE [App::DocumentObjectGroupPython] G4_CELLULOSE_CELLOPHANE  # scripted group (container) (typed FeaturePython)
  Dunit = g/cm3
  Dvalue = 1.42
  Group = -> [C_element025,H_element021,O_element026]
  conduct = 2
  density = 1
  expand = 3
  formula = G4_CELLULOSE_CELLOPHANE
  name = G4_CELLULOSE_CELLOPHANE
  specific = 4
FEATURE [App::DocumentObjectGroupPython] H_element022  label="H_element : 0.067"  # scripted group (container) (typed FeaturePython)
  n = 0.067125
FEATURE [App::DocumentObjectGroupPython] C_element026  label="C_element : 0.545"  # scripted group (container) (typed FeaturePython)
  n = 0.545403
FEATURE [App::DocumentObjectGroupPython] O_element027  label="O_element : 0.387"  # scripted group (container) (typed FeaturePython)
  n = 0.387472
FEATURE [App::DocumentObjectGroupPython] G4_CELLULOSE_BUTYRATE  # scripted group (container) (typed FeaturePython)
  Dunit = g/cm3
  Dvalue = 1.2
  Group = -> [H_element022,C_element026,O_element027]
  conduct = 2
  density = 1
  expand = 3
  formula = G4_CELLULOSE_BUTYRATE
  name = G4_CELLULOSE_BUTYRATE
  specific = 4
FEATURE [App::DocumentObjectGroupPython] H_element023  label="H_element : 0.029"  # scripted group (container) (typed FeaturePython)
  n = 0.029216
FEATURE [App::DocumentObjectGroupPython] C_element027  label="C_element : 0.271"  # scripted group (container) (typed FeaturePython)
  n = 0.271296
FEATURE [App::DocumentObjectGroupPython] N_element013  label="N_element : 0.121"  # scripted group (container) (typed FeaturePython)
  n = 0.121276
FEATURE [App::DocumentObjectGroupPython] O_element028  label="O_element : 0.578"  # scripted group (container) (typed FeaturePython)
  n = 0.578212
FEATURE [App::DocumentObjectGroupPython] G4_CELLULOSE_NITRATE  # scripted group (container) (typed FeaturePython)
  Dunit = g/cm3
  Dvalue = 1.49
  Group = -> [H_element023,C_element027,N_element013,O_element028]
  conduct = 2
  density = 1
  expand = 3
  formula = G4_CELLULOSE_NITRATE
  name = G4_CELLULOSE_NITRATE
  specific = 4
FEATURE [App::DocumentObjectGroupPython] H_element024  label="H_element : 0.108"  # scripted group (container) (typed FeaturePython)
  n = 0.107596
FEATURE [App::DocumentObjectGroupPython] N_element014  label="N_element : 0.001"  # scripted group (container) (typed FeaturePython)
  n = 0.0008
FEATURE [App::DocumentObjectGroupPython] O_element029  label="O_element : 0.875"  # scripted group (container) (typed FeaturePython)
  n = 0.874976
FEATURE [App::DocumentObjectGroupPython] S_element008  label="S_element : 0.015"  # scripted group (container) (typed FeaturePython)
  n = 0.014627
FEATURE [App::DocumentObjectGroupPython] Ce_element001  label="Ce_element : 0.002"  # scripted group (container) (typed FeaturePython)
  n = 0.002001
FEATURE [App::DocumentObjectGroupPython] G4_CERIC_SULFATE  # scripted group (container) (typed FeaturePython)
  Dunit = g/cm3
  Dvalue = 1.03
  Group = -> [H_element024,N_element014,O_element029,S_element008,Ce_element001]
  conduct = 2
  density = 1
  expand = 3
  formula = G4_CERIC_SULFATE
  name = G4_CERIC_SULFATE
  specific = 4
FEATURE [App::DocumentObjectGroupPython] Cs_element001  label="Cs_element : 1"  # scripted group (container) (typed FeaturePython)
  n = 1
  ref = Cs_element
FEATURE [App::DocumentObjectGroupPython] F_element006  label="F_element : 1"  # scripted group (container) (typed FeaturePython)
  n = 1
  ref = F_element
FEATURE [App::DocumentObjectGroupPython] G4_CESIUM_FLUORIDE  # scripted group (container) (typed FeaturePython)
  Dunit = g/cm3
  Dvalue = 4.115
  Group = -> [Cs_element001,F_element006]
  conduct = 2
  density = 1
  expand = 3
  formula = G4_CESIUM_FLUORIDE
  name = G4_CESIUM_FLUORIDE
  specific = 4
FEATURE [App::DocumentObjectGroupPython] Cs_element002  label="Cs_element : 002"  # scripted group (container) (typed FeaturePython)
  n = 1
  ref = Cs_element
FEATURE [App::DocumentObjectGroupPython] I_element001  label="I_element : 1"  # scripted group (container) (typed FeaturePython)
  n = 1
  ref = I_element
FEATURE [App::DocumentObjectGroupPython] G4_CESIUM_IODIDE  # scripted group (container) (typed FeaturePython)
  Dunit = g/cm3
  Dvalue = 4.51
  Group = -> [Cs_element002,I_element001]
  conduct = 2
  density = 1
  expand = 3
  formula = G4_CESIUM_IODIDE
  name = G4_CESIUM_IODIDE
  specific = 4
FEATURE [App::DocumentObjectGroupPython] C_element028  label="C_element : 013"  # scripted group (container) (typed FeaturePython)
  n = 6
  ref = C_element
FEATURE [App::DocumentObjectGroupPython] H_element025  label="H_element : 013"  # scripted group (container) (typed FeaturePython)
  n = 5
  ref = H_element
FEATURE [App::DocumentObjectGroupPython] Cl_element005  label="Cl_element : 1"  # scripted group (container) (typed FeaturePython)
  n = 1
  ref = Cl_element
FEATURE [App::DocumentObjectGroupPython] G4_CHLOROBENZENE  # scripted group (container) (typed FeaturePython)
  Dunit = g/cm3
  Dvalue = 1.1058
  Group = -> [C_element028,H_element025,Cl_element005]
  conduct = 2
  density = 1
  expand = 3
  formula = G4_CHLOROBENZENE
  name = G4_CHLOROBENZENE
  specific = 4
FEATURE [App::DocumentObjectGroupPython] C_element029  label="C_element : 014"  # scripted group (container) (typed FeaturePython)
  n = 1
  ref = C_element
FEATURE [App::DocumentObjectGroupPython] H_element026  label="H_element : 1"  # scripted group (container) (typed FeaturePython)
  n = 1
  ref = H_element
FEATURE [App::DocumentObjectGroupPython] Cl_element006  label="Cl_element : 3"  # scripted group (container) (typed FeaturePython)
  n = 3
  ref = Cl_element
FEATURE [App::DocumentObjectGroupPython] G4_CHLOROFORM  # scripted group (container) (typed FeaturePython)
  Dunit = g/cm3
  Dvalue = 1.4832
  Group = -> [C_element029,H_element026,Cl_element006]
  conduct = 2
  density = 1
  expand = 3
  formula = G4_CHLOROFORM
  name = G4_CHLOROFORM
  specific = 4
FEATURE [App::DocumentObjectGroupPython] H_element027  label="H_element : 0.010"  # scripted group (container) (typed FeaturePython)
  n = 0.01
FEATURE [App::DocumentObjectGroupPython] C_element030  label="C_element : 0.001"  # scripted group (container) (typed FeaturePython)
  n = 0.001
FEATURE [App::DocumentObjectGroupPython] O_element030  label="O_element : 0.529"  # scripted group (container) (typed FeaturePython)
  n = 0.529107
FEATURE [App::DocumentObjectGroupPython] Na_element005  label="Na_element : 0.016"  # scripted group (container) (typed FeaturePython)
  n = 0.016
FEATURE [App::DocumentObjectGroupPython] Mg_element003  label="Mg_element : 0.004"  # scripted group (container) (typed FeaturePython)
  n = 0.002
FEATURE [App::DocumentObjectGroupPython] Al_element002  label="Al_element : 0.034"  # scripted group (container) (typed FeaturePython)
  n = 0.033872
FEATURE [App::DocumentObjectGroupPython] Si_element002  label="Si_element : 0.337"  # scripted group (container) (typed FeaturePython)
  n = 0.337021
FEATURE [App::DocumentObjectGroupPython] K_element003  label="K_element : 0.013"  # scripted group (container) (typed FeaturePython)
  n = 0.013
FEATURE [App::DocumentObjectGroupPython] Ca_element010  label="Ca_element : 0.044"  # scripted group (container) (typed FeaturePython)
  n = 0.044
FEATURE [App::DocumentObjectGroupPython] Fe_element002  label="Fe_element : 0.014"  # scripted group (container) (typed FeaturePython)
  n = 0.014
FEATURE [App::DocumentObjectGroupPython] G4_CONCRETE  # scripted group (container) (typed FeaturePython)
  Dunit = g/cm3
  Dvalue = 2.3
  Group = -> [H_element027,C_element030,O_element030,Na_element005,Mg_element003,Al_element002,Si_element002,K_element003,Ca_element010,Fe_element002]
  conduct = 2
  density = 1
  expand = 3
  formula = G4_CONCRETE
  name = G4_CONCRETE
  specific = 4
FEATURE [App::DocumentObjectGroupPython] C_element031  label="C_element : 015"  # scripted group (container) (typed FeaturePython)
  n = 6
  ref = C_element
FEATURE [App::DocumentObjectGroupPython] H_element028  label="H_element : 12"  # scripted group (container) (typed FeaturePython)
  n = 12
  ref = H_element
FEATURE [App::DocumentObjectGroupPython] G4_CYCLOHEXANE  # scripted group (container) (typed FeaturePython)
  Dunit = g/cm3
  Dvalue = 0.779
  Group = -> [C_element031,H_element028]
  conduct = 2
  density = 1
  expand = 3
  formula = G4_CYCLOHEXANE
  name = G4_CYCLOHEXANE
  specific = 4
FEATURE [App::DocumentObjectGroupPython] C_element032  label="C_element : 016"  # scripted group (container) (typed FeaturePython)
  n = 6
  ref = C_element
FEATURE [App::DocumentObjectGroupPython] H_element029  label="H_element : 4"  # scripted group (container) (typed FeaturePython)
  n = 4
  ref = H_element
FEATURE [App::DocumentObjectGroupPython] Cl_element007  label="Cl_element : 2"  # scripted group (container) (typed FeaturePython)
  n = 2
  ref = Cl_element
FEATURE [App::DocumentObjectGroupPython] G4_1_2_DICHLOROBENZENE  label="G4_1.2-DICHLOROBENZENE"  # scripted group (container) (typed FeaturePython)
  Dunit = g/cm3
  Dvalue = 1.3048
  Group = -> [C_element032,H_element029,Cl_element007]
  conduct = 2
  density = 1
  expand = 3
  formula = G4_1.2-DICHLOROBENZENE
  name = G4_1.2-DICHLOROBENZENE
  specific = 4
FEATURE [App::DocumentObjectGroupPython] C_element033  label="C_element : 017"  # scripted group (container) (typed FeaturePython)
  n = 4
  ref = C_element
FEATURE [App::DocumentObjectGroupPython] H_element030  label="H_element : 8"  # scripted group (container) (typed FeaturePython)
  n = 8
  ref = H_element
FEATURE [App::DocumentObjectGroupPython] O_element031  label="O_element : 014"  # scripted group (container) (typed FeaturePython)
  n = 1
  ref = O_element
FEATURE [App::DocumentObjectGroupPython] Cl_element008  label="Cl_element : 005"  # scripted group (container) (typed FeaturePython)
  n = 2
  ref = Cl_element
FEATURE [App::DocumentObjectGroupPython] G4_DICHLORODIETHYL_ETHER  # scripted group (container) (typed FeaturePython)
  Dunit = g/cm3
  Dvalue = 1.2199
  Group = -> [C_element033,H_element030,O_element031,Cl_element008]
  conduct = 2
  density = 1
  expand = 3
  formula = G4_DICHLORODIETHYL_ETHER
  name = G4_DICHLORODIETHYL_ETHER
  specific = 4
FEATURE [App::DocumentObjectGroupPython] C_element034  label="C_element : 018"  # scripted group (container) (typed FeaturePython)
  n = 2
  ref = C_element
FEATURE [App::DocumentObjectGroupPython] H_element031  label="H_element : 014"  # scripted group (container) (typed FeaturePython)
  n = 4
  ref = H_element
FEATURE [App::DocumentObjectGroupPython] Cl_element009  label="Cl_element : 006"  # scripted group (container) (typed FeaturePython)
  n = 2
  ref = Cl_element
FEATURE [App::DocumentObjectGroupPython] G4_1_2_DICHLOROETHANE  label="G4_1.2-DICHLOROETHANE"  # scripted group (container) (typed FeaturePython)
  Dunit = g/cm3
  Dvalue = 1.2351
  Group = -> [C_element034,H_element031,Cl_element009]
  conduct = 2
  density = 1
  expand = 3
  formula = G4_1.2-DICHLOROETHANE
  name = G4_1.2-DICHLOROETHANE
  specific = 4
FEATURE [App::DocumentObjectGroupPython] C_element035  label="C_element : 019"  # scripted group (container) (typed FeaturePython)
  n = 4
  ref = C_element
FEATURE [App::DocumentObjectGroupPython] H_element032  label="H_element : 015"  # scripted group (container) (typed FeaturePython)
  n = 10
  ref = H_element
FEATURE [App::DocumentObjectGroupPython] O_element032  label="O_element : 015"  # scripted group (container) (typed FeaturePython)
  n = 1
  ref = O_element
FEATURE [App::DocumentObjectGroupPython] G4_DIETHYL_ETHER  # scripted group (container) (typed FeaturePython)
  Dunit = g/cm3
  Dvalue = 0.71378
  Group = -> [C_element035,H_element032,O_element032]
  conduct = 2
  density = 1
  expand = 3
  formula = G4_DIETHYL_ETHER
  name = G4_DIETHYL_ETHER
  specific = 4
FEATURE [App::DocumentObjectGroupPython] C_element036  label="C_element : 020"  # scripted group (container) (typed FeaturePython)
  n = 3
  ref = C_element
FEATURE [App::DocumentObjectGroupPython] H_element033  label="H_element : 016"  # scripted group (container) (typed FeaturePython)
  n = 7
  ref = H_element
FEATURE [App::DocumentObjectGroupPython] N_element015  label="N_element : 008"  # scripted group (container) (typed FeaturePython)
  n = 1
  ref = N_element
FEATURE [App::DocumentObjectGroupPython] O_element033  label="O_element : 016"  # scripted group (container) (typed FeaturePython)
  n = 1
  ref = O_element
FEATURE [App::DocumentObjectGroupPython] G4_N_N_DIMETHYL_FORMAMIDE  label="G4_N.N-DIMETHYL_FORMAMIDE"  # scripted group (container) (typed FeaturePython)
  Dunit = g/cm3
  Dvalue = 0.9487
  Group = -> [C_element036,H_element033,N_element015,O_element033]
  conduct = 2
  density = 1
  expand = 3
  formula = G4_N.N-DIMETHYL_FORMAMIDE
  name = G4_N.N-DIMETHYL_FORMAMIDE
  specific = 4
FEATURE [App::DocumentObjectGroupPython] C_element037  label="C_element : 021"  # scripted group (container) (typed FeaturePython)
  n = 2
  ref = C_element
FEATURE [App::DocumentObjectGroupPython] H_element034  label="H_element : 017"  # scripted group (container) (typed FeaturePython)
  n = 6
  ref = H_element
FEATURE [App::DocumentObjectGroupPython] O_element034  label="O_element : 017"  # scripted group (container) (typed FeaturePython)
  n = 1
  ref = O_element
FEATURE [App::DocumentObjectGroupPython] S_element009  label="S_element : 003"  # scripted group (container) (typed FeaturePython)
  n = 1
  ref = S_element
FEATURE [App::DocumentObjectGroupPython] G4_DIMETHYL_SULFOXIDE  # scripted group (container) (typed FeaturePython)
  Dunit = g/cm3
  Dvalue = 1.1014
  Group = -> [C_element037,H_element034,O_element034,S_element009]
  conduct = 2
  density = 1
  expand = 3
  formula = G4_DIMETHYL_SULFOXIDE
  name = G4_DIMETHYL_SULFOXIDE
  specific = 4
FEATURE [App::DocumentObjectGroupPython] C_element038  label="C_element : 022"  # scripted group (container) (typed FeaturePython)
  n = 2
  ref = C_element
FEATURE [App::DocumentObjectGroupPython] H_element035  label="H_element : 018"  # scripted group (container) (typed FeaturePython)
  n = 6
  ref = H_element
FEATURE [App::DocumentObjectGroupPython] G4_ETHANE  # scripted group (container) (typed FeaturePython)
  Dunit = g/cm3
  Dvalue = 0.00125324
  Group = -> [C_element038,H_element035]
  conduct = 2
  density = 1
  expand = 3
  formula = G4_ETHANE
  name = G4_ETHANE
  specific = 4
FEATURE [App::DocumentObjectGroupPython] C_element039  label="C_element : 023"  # scripted group (container) (typed FeaturePython)
  n = 2
  ref = C_element
FEATURE [App::DocumentObjectGroupPython] H_element036  label="H_element : 019"  # scripted group (container) (typed FeaturePython)
  n = 6
  ref = H_element
FEATURE [App::DocumentObjectGroupPython] O_element035  label="O_element : 018"  # scripted group (container) (typed FeaturePython)
  n = 1
  ref = O_element
FEATURE [App::DocumentObjectGroupPython] G4_ETHYL_ALCOHOL  # scripted group (container) (typed FeaturePython)
  Dunit = g/cm3
  Dvalue = 0.7893
  Group = -> [C_element039,H_element036,O_element035]
  conduct = 2
  density = 1
  expand = 3
  formula = G4_ETHYL_ALCOHOL
  name = G4_ETHYL_ALCOHOL
  specific = 4
FEATURE [App::DocumentObjectGroupPython] H_element037  label="H_element : 0.090"  # scripted group (container) (typed FeaturePython)
  n = 0.090027
FEATURE [App::DocumentObjectGroupPython] C_element040  label="C_element : 0.585"  # scripted group (container) (typed FeaturePython)
  n = 0.585182
FEATURE [App::DocumentObjectGroupPython] O_element036  label="O_element : 0.325"  # scripted group (container) (typed FeaturePython)
  n = 0.324791
FEATURE [App::DocumentObjectGroupPython] G4_ETHYL_CELLULOSE  # scripted group (container) (typed FeaturePython)
  Dunit = g/cm3
  Dvalue = 1.13
  Group = -> [H_element037,C_element040,O_element036]
  conduct = 2
  density = 1
  expand = 3
  formula = G4_ETHYL_CELLULOSE
  name = G4_ETHYL_CELLULOSE
  specific = 4
FEATURE [App::DocumentObjectGroupPython] C_element041  label="C_element : 024"  # scripted group (container) (typed FeaturePython)
  n = 2
  ref = C_element
FEATURE [App::DocumentObjectGroupPython] H_element038  label="H_element : 020"  # scripted group (container) (typed FeaturePython)
  n = 4
  ref = H_element
FEATURE [App::DocumentObjectGroupPython] G4_ETHYLENE  # scripted group (container) (typed FeaturePython)
  Dunit = g/cm3
  Dvalue = 0.00117497
  Group = -> [C_element041,H_element038]
  conduct = 2
  density = 1
  expand = 3
  formula = G4_ETHYLENE
  name = G4_ETHYLENE
  specific = 4
FEATURE [App::DocumentObjectGroupPython] H_element039  label="H_element : 0.096"  # scripted group (container) (typed FeaturePython)
  n = 0.096
FEATURE [App::DocumentObjectGroupPython] C_element042  label="C_element : 0.195"  # scripted group (container) (typed FeaturePython)
  n = 0.195
FEATURE [App::DocumentObjectGroupPython] N_element016  label="N_element : 0.057"  # scripted group (container) (typed FeaturePython)
  n = 0.057
FEATURE [App::DocumentObjectGroupPython] O_element037  label="O_element : 0.646"  # scripted group (container) (typed FeaturePython)
  n = 0.646
FEATURE [App::DocumentObjectGroupPython] Na_element006  label="Na_element : 0.017"  # scripted group (container) (typed FeaturePython)
  n = 0.001
FEATURE [App::DocumentObjectGroupPython] P_element005  label="P_element : 0.104"  # scripted group (container) (typed FeaturePython)
  n = 0.001
FEATURE [App::DocumentObjectGroupPython] S_element010  label="S_element : 0.016"  # scripted group (container) (typed FeaturePython)
  n = 0.003
FEATURE [App::DocumentObjectGroupPython] Cl_element010  label="Cl_element : 0.005"  # scripted group (container) (typed FeaturePython)
  n = 0.001
FEATURE [App::DocumentObjectGroupPython] G4_EYE_LENS_ICRP  # scripted group (container) (typed FeaturePython)
  Dunit = g/cm3
  Dvalue = 1.07
  Group = -> [H_element039,C_element042,N_element016,O_element037,Na_element006,P_element005,S_element010,Cl_element010]
  conduct = 2
  density = 1
  expand = 3
  formula = G4_EYE_LENS_ICRP
  name = G4_EYE_LENS_ICRP
  specific = 4
FEATURE [App::DocumentObjectGroupPython] Fe_element003  label="Fe_element : 2"  # scripted group (container) (typed FeaturePython)
  n = 2
  ref = Fe_element
FEATURE [App::DocumentObjectGroupPython] O_element038  label="O_element : 019"  # scripted group (container) (typed FeaturePython)
  n = 3
  ref = O_element
FEATURE [App::DocumentObjectGroupPython] G4_FERRIC_OXIDE  # scripted group (container) (typed FeaturePython)
  Dunit = g/cm3
  Dvalue = 5.2
  Group = -> [Fe_element003,O_element038]
  conduct = 2
  density = 1
  expand = 3
  formula = G4_FERRIC_OXIDE
  name = G4_FERRIC_OXIDE
  specific = 4
FEATURE [App::DocumentObjectGroupPython] Fe_element004  label="Fe_element : 1"  # scripted group (container) (typed FeaturePython)
  n = 1
  ref = Fe_element
FEATURE [App::DocumentObjectGroupPython] B_element003  label="B_element : 1"  # scripted group (container) (typed FeaturePython)
  n = 1
  ref = B_element
FEATURE [App::DocumentObjectGroupPython] G4_FERROBORIDE  # scripted group (container) (typed FeaturePython)
  Dunit = g/cm3
  Dvalue = 7.15
  Group = -> [Fe_element004,B_element003]
  conduct = 2
  density = 1
  expand = 3
  formula = G4_FERROBORIDE
  name = G4_FERROBORIDE
  specific = 4
FEATURE [App::DocumentObjectGroupPython] Fe_element005  label="Fe_element : 003"  # scripted group (container) (typed FeaturePython)
  n = 1
  ref = Fe_element
FEATURE [App::DocumentObjectGroupPython] O_element039  label="O_element : 020"  # scripted group (container) (typed FeaturePython)
  n = 1
  ref = O_element
FEATURE [App::DocumentObjectGroupPython] G4_FERROUS_OXIDE  # scripted group (container) (typed FeaturePython)
  Dunit = g/cm3
  Dvalue = 5.7
  Group = -> [Fe_element005,O_element039]
  conduct = 2
  density = 1
  expand = 3
  formula = G4_FERROUS_OXIDE
  name = G4_FERROUS_OXIDE
  specific = 4
FEATURE [App::DocumentObjectGroupPython] H_element040  label="H_element : 0.115"  # scripted group (container) (typed FeaturePython)
  n = 0.108259
FEATURE [App::DocumentObjectGroupPython] N_element017  label="N_element : 0.000"  # scripted group (container) (typed FeaturePython)
  n = 2.7e-05
FEATURE [App::DocumentObjectGroupPython] O_element040  label="O_element : 0.879"  # scripted group (container) (typed FeaturePython)
  n = 0.878636
FEATURE [App::DocumentObjectGroupPython] Na_element007  label="Na_element : 0.000"  # scripted group (container) (typed FeaturePython)
  n = 2.2e-05
FEATURE [App::DocumentObjectGroupPython] S_element011  label="S_element : 0.013"  # scripted group (container) (typed FeaturePython)
  n = 0.012968
FEATURE [App::DocumentObjectGroupPython] Cl_element011  label="Cl_element : 0.000"  # scripted group (container) (typed FeaturePython)
  n = 3.4e-05
FEATURE [App::DocumentObjectGroupPython] Fe_element006  label="Fe_element : 0.000"  # scripted group (container) (typed FeaturePython)
  n = 5.4e-05
FEATURE [App::DocumentObjectGroupPython] G4_FERROUS_SULFATE  # scripted group (container) (typed FeaturePython)
  Dunit = g/cm3
  Dvalue = 1.024
  Group = -> [H_element040,N_element017,O_element040,Na_element007,S_element011,Cl_element011,Fe_element006]
  conduct = 2
  density = 1
  expand = 3
  formula = G4_FERROUS_SULFATE
  name = G4_FERROUS_SULFATE
  specific = 4
FEATURE [App::DocumentObjectGroupPython] C_element043  label="C_element : 0.099"  # scripted group (container) (typed FeaturePython)
  n = 0.099335
FEATURE [App::DocumentObjectGroupPython] F_element007  label="F_element : 0.314"  # scripted group (container) (typed FeaturePython)
  n = 0.314247
FEATURE [App::DocumentObjectGroupPython] Cl_element012  label="Cl_element : 0.586"  # scripted group (container) (typed FeaturePython)
  n = 0.586418
FEATURE [App::DocumentObjectGroupPython] G4_FREON_12  label="G4_FREON-12"  # scripted group (container) (typed FeaturePython)
  Dunit = g/cm3
  Dvalue = 1.12
  Group = -> [C_element043,F_element007,Cl_element012]
  conduct = 2
  density = 1
  expand = 3
  formula = G4_FREON-12
  name = G4_FREON-12
  specific = 4
FEATURE [App::DocumentObjectGroupPython] C_element044  label="C_element : 0.057"  # scripted group (container) (typed FeaturePython)
  n = 0.057245
FEATURE [App::DocumentObjectGroupPython] F_element008  label="F_element : 0.181"  # scripted group (container) (typed FeaturePython)
  n = 0.181096
FEATURE [App::DocumentObjectGroupPython] Br_element001  label="Br_element : 0.762"  # scripted group (container) (typed FeaturePython)
  n = 0.761659
FEATURE [App::DocumentObjectGroupPython] G4_FREON_12B2  label="G4_FREON-12B2"  # scripted group (container) (typed FeaturePython)
  Dunit = g/cm3
  Dvalue = 1.8
  Group = -> [C_element044,F_element008,Br_element001]
  conduct = 2
  density = 1
  expand = 3
  formula = G4_FREON-12B2
  name = G4_FREON-12B2
  specific = 4
FEATURE [App::DocumentObjectGroupPython] C_element045  label="C_element : 0.115"  # scripted group (container) (typed FeaturePython)
  n = 0.114983
FEATURE [App::DocumentObjectGroupPython] F_element009  label="F_element : 0.546"  # scripted group (container) (typed FeaturePython)
  n = 0.545621
FEATURE [App::DocumentObjectGroupPython] Cl_element013  label="Cl_element : 0.339"  # scripted group (container) (typed FeaturePython)
  n = 0.339396
FEATURE [App::DocumentObjectGroupPython] G4_FREON_13  label="G4_FREON-13"  # scripted group (container) (typed FeaturePython)
  Dunit = g/cm3
  Dvalue = 0.95
  Group = -> [C_element045,F_element009,Cl_element013]
  conduct = 2
  density = 1
  expand = 3
  formula = G4_FREON-13
  name = G4_FREON-13
  specific = 4
FEATURE [App::DocumentObjectGroupPython] C_element046  label="C_element : 025"  # scripted group (container) (typed FeaturePython)
  n = 1
  ref = C_element
FEATURE [App::DocumentObjectGroupPython] F_element010  label="F_element : 3"  # scripted group (container) (typed FeaturePython)
  n = 3
  ref = F_element
FEATURE [App::DocumentObjectGroupPython] Br_element002  label="Br_element : 1"  # scripted group (container) (typed FeaturePython)
  n = 1
  ref = Br_element
FEATURE [App::DocumentObjectGroupPython] G4_FREON_13B1  label="G4_FREON-13B1"  # scripted group (container) (typed FeaturePython)
  Dunit = g/cm3
  Dvalue = 1.5
  Group = -> [C_element046,F_element010,Br_element002]
  conduct = 2
  density = 1
  expand = 3
  formula = G4_FREON-13B1
  name = G4_FREON-13B1
  specific = 4
FEATURE [App::DocumentObjectGroupPython] C_element047  label="C_element : 0.061"  # scripted group (container) (typed FeaturePython)
  n = 0.061309
FEATURE [App::DocumentObjectGroupPython] F_element011  label="F_element : 0.291"  # scripted group (container) (typed FeaturePython)
  n = 0.290924
FEATURE [App::DocumentObjectGroupPython] I_element002  label="I_element : 0.648"  # scripted group (container) (typed FeaturePython)
  n = 0.647767
FEATURE [App::DocumentObjectGroupPython] G4_FREON_13I1  label="G4_FREON-13I1"  # scripted group (container) (typed FeaturePython)
  Dunit = g/cm3
  Dvalue = 1.8
  Group = -> [C_element047,F_element011,I_element002]
  conduct = 2
  density = 1
  expand = 3
  formula = G4_FREON-13I1
  name = G4_FREON-13I1
  specific = 4
FEATURE [App::DocumentObjectGroupPython] Gd_element001  label="Gd_element : 2"  # scripted group (container) (typed FeaturePython)
  n = 2
  ref = Gd_element
FEATURE [App::DocumentObjectGroupPython] O_element041  label="O_element : 021"  # scripted group (container) (typed FeaturePython)
  n = 2
  ref = O_element
FEATURE [App::DocumentObjectGroupPython] S_element012  label="S_element : 004"  # scripted group (container) (typed FeaturePython)
  n = 1
  ref = S_element
FEATURE [App::DocumentObjectGroupPython] G4_GADOLINIUM_OXYSULFIDE  # scripted group (container) (typed FeaturePython)
  Dunit = g/cm3
  Dvalue = 7.44
  Group = -> [Gd_element001,O_element041,S_element012]
  conduct = 2
  density = 1
  expand = 3
  formula = G4_GADOLINIUM_OXYSULFIDE
  name = G4_GADOLINIUM_OXYSULFIDE
  specific = 4
FEATURE [App::DocumentObjectGroupPython] Ga_element001  label="Ga_element : 1"  # scripted group (container) (typed FeaturePython)
  n = 1
  ref = Ga_element
FEATURE [App::DocumentObjectGroupPython] As_element001  label="As_element : 1"  # scripted group (container) (typed FeaturePython)
  n = 1
  ref = As_element
FEATURE [App::DocumentObjectGroupPython] G4_GALLIUM_ARSENIDE  # scripted group (container) (typed FeaturePython)
  Dunit = g/cm3
  Dvalue = 5.31
  Group = -> [Ga_element001,As_element001]
  conduct = 2
  density = 1
  expand = 3
  formula = G4_GALLIUM_ARSENIDE
  name = G4_GALLIUM_ARSENIDE
  specific = 4
FEATURE [App::DocumentObjectGroupPython] H_element041  label="H_element : 0.081"  # scripted group (container) (typed FeaturePython)
  n = 0.08118
FEATURE [App::DocumentObjectGroupPython] C_element048  label="C_element : 0.416"  # scripted group (container) (typed FeaturePython)
  n = 0.41606
FEATURE [App::DocumentObjectGroupPython] N_element018  label="N_element : 0.111"  # scripted group (container) (typed FeaturePython)
  n = 0.11124
FEATURE [App::DocumentObjectGroupPython] O_element042  label="O_element : 0.381"  # scripted group (container) (typed FeaturePython)
  n = 0.38064
FEATURE [App::DocumentObjectGroupPython] S_element013  label="S_element : 0.011"  # scripted group (container) (typed FeaturePython)
  n = 0.01088
FEATURE [App::DocumentObjectGroupPython] G4_GEL_PHOTO_EMULSION  # scripted group (container) (typed FeaturePython)
  Dunit = g/cm3
  Dvalue = 1.2914
  Group = -> [H_element041,C_element048,N_element018,O_element042,S_element013]
  conduct = 2
  density = 1
  expand = 3
  formula = G4_GEL_PHOTO_EMULSION
  name = G4_GEL_PHOTO_EMULSION
  specific = 4
FEATURE [App::DocumentObjectGroupPython] B_element004  label="B_element : 0.040"  # scripted group (container) (typed FeaturePython)
  n = 0.0400639
FEATURE [App::DocumentObjectGroupPython] O_element043  label="O_element : 0.540"  # scripted group (container) (typed FeaturePython)
  n = 0.539561
FEATURE [App::DocumentObjectGroupPython] Na_element008  label="Na_element : 0.028"  # scripted group (container) (typed FeaturePython)
  n = 0.0281909
FEATURE [App::DocumentObjectGroupPython] Al_element003  label="Al_element : 0.012"  # scripted group (container) (typed FeaturePython)
  n = 0.011644
FEATURE [App::DocumentObjectGroupPython] Si_element003  label="Si_element : 0.377"  # scripted group (container) (typed FeaturePython)
  n = 0.377219
FEATURE [App::DocumentObjectGroupPython] K_element004  label="K_element : 0.014"  # scripted group (container) (typed FeaturePython)
  n = 0.00332099
FEATURE [App::DocumentObjectGroupPython] G4_Pyrex_Glass  # scripted group (container) (typed FeaturePython)
  Dunit = g/cm3
  Dvalue = 2.23
  Group = -> [B_element004,O_element043,Na_element008,Al_element003,Si_element003,K_element004]
  conduct = 2
  density = 1
  expand = 3
  formula = G4_Pyrex_Glass
  name = G4_Pyrex_Glass
  specific = 4
FEATURE [App::DocumentObjectGroupPython] O_element044  label="O_element : 0.156"  # scripted group (container) (typed FeaturePython)
  n = 0.156453
FEATURE [App::DocumentObjectGroupPython] Si_element004  label="Si_element : 0.081"  # scripted group (container) (typed FeaturePython)
  n = 0.080866
FEATURE [App::DocumentObjectGroupPython] Ti_element001  label="Ti_element : 0.008"  # scripted group (container) (typed FeaturePython)
  n = 0.008092
FEATURE [App::DocumentObjectGroupPython] As_element002  label="As_element : 0.003"  # scripted group (container) (typed FeaturePython)
  n = 0.002651
FEATURE [App::DocumentObjectGroupPython] Pb_element001  label="Pb_element : 0.752"  # scripted group (container) (typed FeaturePython)
  n = 0.751938
FEATURE [App::DocumentObjectGroupPython] G4_GLASS_LEAD  # scripted group (container) (typed FeaturePython)
  Dunit = g/cm3
  Dvalue = 6.22
  Group = -> [O_element044,Si_element004,Ti_element001,As_element002,Pb_element001]
  conduct = 2
  density = 1
  expand = 3
  formula = G4_GLASS_LEAD
  name = G4_GLASS_LEAD
  specific = 4
FEATURE [App::DocumentObjectGroupPython] O_element045  label="O_element : 0.460"  # scripted group (container) (typed FeaturePython)
  n = 0.4598
FEATURE [App::DocumentObjectGroupPython] Na_element009  label="Na_element : 0.096"  # scripted group (container) (typed FeaturePython)
  n = 0.0964411
FEATURE [App::DocumentObjectGroupPython] Si_element005  label="Si_element : 0.378"  # scripted group (container) (typed FeaturePython)
  n = 0.336553
FEATURE [App::DocumentObjectGroupPython] Ca_element011  label="Ca_element : 0.107"  # scripted group (container) (typed FeaturePython)
  n = 0.107205
FEATURE [App::DocumentObjectGroupPython] G4_GLASS_PLATE  # scripted group (container) (typed FeaturePython)
  Dunit = g/cm3
  Dvalue = 2.4
  Group = -> [O_element045,Na_element009,Si_element005,Ca_element011]
  conduct = 2
  density = 1
  expand = 3
  formula = G4_GLASS_PLATE
  name = G4_GLASS_PLATE
  specific = 4
FEATURE [App::DocumentObjectGroupPython] C_element049  label="C_element : 026"  # scripted group (container) (typed FeaturePython)
  n = 5
  ref = C_element
FEATURE [App::DocumentObjectGroupPython] H_element042  label="H_element : 021"  # scripted group (container) (typed FeaturePython)
  n = 10
  ref = H_element
FEATURE [App::DocumentObjectGroupPython] N_element019  label="N_element : 2"  # scripted group (container) (typed FeaturePython)
  n = 2
  ref = N_element
FEATURE [App::DocumentObjectGroupPython] O_element046  label="O_element : 022"  # scripted group (container) (typed FeaturePython)
  n = 3
  ref = O_element
FEATURE [App::DocumentObjectGroupPython] G4_GLUTAMINE  # scripted group (container) (typed FeaturePython)
  Dunit = g/cm3
  Dvalue = 1.46
  Group = -> [C_element049,H_element042,N_element019,O_element046]
  conduct = 2
  density = 1
  expand = 3
  formula = G4_GLUTAMINE
  name = G4_GLUTAMINE
  specific = 4
FEATURE [App::DocumentObjectGroupPython] C_element050  label="C_element : 027"  # scripted group (container) (typed FeaturePython)
  n = 3
  ref = C_element
FEATURE [App::DocumentObjectGroupPython] H_element043  label="H_element : 022"  # scripted group (container) (typed FeaturePython)
  n = 8
  ref = H_element
FEATURE [App::DocumentObjectGroupPython] O_element047  label="O_element : 023"  # scripted group (container) (typed FeaturePython)
  n = 3
  ref = O_element
FEATURE [App::DocumentObjectGroupPython] G4_GLYCEROL  # scripted group (container) (typed FeaturePython)
  Dunit = g/cm3
  Dvalue = 1.2613
  Group = -> [C_element050,H_element043,O_element047]
  conduct = 2
  density = 1
  expand = 3
  formula = G4_GLYCEROL
  name = G4_GLYCEROL
  specific = 4
FEATURE [App::DocumentObjectGroupPython] C_element051  label="C_element : 028"  # scripted group (container) (typed FeaturePython)
  n = 5
  ref = C_element
FEATURE [App::DocumentObjectGroupPython] H_element044  label="H_element : 023"  # scripted group (container) (typed FeaturePython)
  n = 5
  ref = H_element
FEATURE [App::DocumentObjectGroupPython] N_element020  label="N_element : 009"  # scripted group (container) (typed FeaturePython)
  n = 5
  ref = N_element
FEATURE [App::DocumentObjectGroupPython] O_element048  label="O_element : 024"  # scripted group (container) (typed FeaturePython)
  n = 1
  ref = O_element
FEATURE [App::DocumentObjectGroupPython] G4_GUANINE  # scripted group (container) (typed FeaturePython)
  Dunit = g/cm3
  Dvalue = 2.2
  Group = -> [C_element051,H_element044,N_element020,O_element048]
  conduct = 2
  density = 1
  expand = 3
  formula = G4_GUANINE
  name = G4_GUANINE
  specific = 4
FEATURE [App::DocumentObjectGroupPython] Ca_element012  label="Ca_element : 006"  # scripted group (container) (typed FeaturePython)
  n = 1
  ref = Ca_element
FEATURE [App::DocumentObjectGroupPython] S_element014  label="S_element : 005"  # scripted group (container) (typed FeaturePython)
  n = 1
  ref = S_element
FEATURE [App::DocumentObjectGroupPython] O_element049  label="O_element : 6"  # scripted group (container) (typed FeaturePython)
  n = 6
  ref = O_element
FEATURE [App::DocumentObjectGroupPython] H_element045  label="H_element : 024"  # scripted group (container) (typed FeaturePython)
  n = 4
  ref = H_element
FEATURE [App::DocumentObjectGroupPython] G4_GYPSUM  # scripted group (container) (typed FeaturePython)
  Dunit = g/cm3
  Dvalue = 2.32
  Group = -> [Ca_element012,S_element014,O_element049,H_element045]
  conduct = 2
  density = 1
  expand = 3
  formula = G4_GYPSUM
  name = G4_GYPSUM
  specific = 4
FEATURE [App::DocumentObjectGroupPython] C_element052  label="C_element : 7"  # scripted group (container) (typed FeaturePython)
  n = 7
  ref = C_element
FEATURE [App::DocumentObjectGroupPython] H_element046  label="H_element : 16"  # scripted group (container) (typed FeaturePython)
  n = 16
  ref = H_element
FEATURE [App::DocumentObjectGroupPython] G4_N_HEPTANE  label="G4_N-HEPTANE"  # scripted group (container) (typed FeaturePython)
  Dunit = g/cm3
  Dvalue = 0.68376
  Group = -> [C_element052,H_element046]
  conduct = 2
  density = 1
  expand = 3
  formula = G4_N-HEPTANE
  name = G4_N-HEPTANE
  specific = 4
FEATURE [App::DocumentObjectGroupPython] C_element053  label="C_element : 029"  # scripted group (container) (typed FeaturePython)
  n = 6
  ref = C_element
FEATURE [App::DocumentObjectGroupPython] H_element047  label="H_element : 14"  # scripted group (container) (typed FeaturePython)
  n = 14
  ref = H_element
FEATURE [App::DocumentObjectGroupPython] G4_N_HEXANE  label="G4_N-HEXANE"  # scripted group (container) (typed FeaturePython)
  Dunit = g/cm3
  Dvalue = 0.6603
  Group = -> [C_element053,H_element047]
  conduct = 2
  density = 1
  expand = 3
  formula = G4_N-HEXANE
  name = G4_N-HEXANE
  specific = 4
FEATURE [App::DocumentObjectGroupPython] C_element054  label="C_element : 22"  # scripted group (container) (typed FeaturePython)
  n = 22
  ref = C_element
FEATURE [App::DocumentObjectGroupPython] H_element048  label="H_element : 025"  # scripted group (container) (typed FeaturePython)
  n = 10
  ref = H_element
FEATURE [App::DocumentObjectGroupPython] N_element021  label="N_element : 010"  # scripted group (container) (typed FeaturePython)
  n = 2
  ref = N_element
FEATURE [App::DocumentObjectGroupPython] O_element050  label="O_element : 025"  # scripted group (container) (typed FeaturePython)
  n = 5
  ref = O_element
FEATURE [App::DocumentObjectGroupPython] G4_KAPTON  # scripted group (container) (typed FeaturePython)
  Dunit = g/cm3
  Dvalue = 1.42
  Group = -> [C_element054,H_element048,N_element021,O_element050]
  conduct = 2
  density = 1
  expand = 3
  formula = G4_KAPTON
  name = G4_KAPTON
  specific = 4
FEATURE [App::DocumentObjectGroupPython] La_element001  label="La_element : 1"  # scripted group (container) (typed FeaturePython)
  n = 1
  ref = La_element
FEATURE [App::DocumentObjectGroupPython] Br_element003  label="Br_element : 002"  # scripted group (container) (typed FeaturePython)
  n = 1
  ref = Br_element
FEATURE [App::DocumentObjectGroupPython] O_element051  label="O_element : 026"  # scripted group (container) (typed FeaturePython)
  n = 1
  ref = O_element
FEATURE [App::DocumentObjectGroupPython] G4_LANTHANUM_OXYBROMIDE  # scripted group (container) (typed FeaturePython)
  Dunit = g/cm3
  Dvalue = 6.28
  Group = -> [La_element001,Br_element003,O_element051]
  conduct = 2
  density = 1
  expand = 3
  formula = G4_LANTHANUM_OXYBROMIDE
  name = G4_LANTHANUM_OXYBROMIDE
  specific = 4
FEATURE [App::DocumentObjectGroupPython] La_element002  label="La_element : 2"  # scripted group (container) (typed FeaturePython)
  n = 2
  ref = La_element
FEATURE [App::DocumentObjectGroupPython] O_element052  label="O_element : 027"  # scripted group (container) (typed FeaturePython)
  n = 2
  ref = O_element
FEATURE [App::DocumentObjectGroupPython] S_element015  label="S_element : 006"  # scripted group (container) (typed FeaturePython)
  n = 1
  ref = S_element
FEATURE [App::DocumentObjectGroupPython] G4_LANTHANUM_OXYSULFIDE  # scripted group (container) (typed FeaturePython)
  Dunit = g/cm3
  Dvalue = 5.86
  Group = -> [La_element002,O_element052,S_element015]
  conduct = 2
  density = 1
  expand = 3
  formula = G4_LANTHANUM_OXYSULFIDE
  name = G4_LANTHANUM_OXYSULFIDE
  specific = 4
FEATURE [App::DocumentObjectGroupPython] O_element053  label="O_element : 0.072"  # scripted group (container) (typed FeaturePython)
  n = 0.071682
FEATURE [App::DocumentObjectGroupPython] Pb_element002  label="Pb_element : 0.928"  # scripted group (container) (typed FeaturePython)
  n = 0.928318
FEATURE [App::DocumentObjectGroupPython] G4_LEAD_OXIDE  # scripted group (container) (typed FeaturePython)
  Dunit = g/cm3
  Dvalue = 9.53
  Group = -> [O_element053,Pb_element002]
  conduct = 2
  density = 1
  expand = 3
  formula = G4_LEAD_OXIDE
  name = G4_LEAD_OXIDE
  specific = 4
FEATURE [App::DocumentObjectGroupPython] Li_element001  label="Li_element : 1"  # scripted group (container) (typed FeaturePython)
  n = 1
  ref = Li_element
FEATURE [App::DocumentObjectGroupPython] N_element022  label="N_element : 011"  # scripted group (container) (typed FeaturePython)
  n = 1
  ref = N_element
FEATURE [App::DocumentObjectGroupPython] H_element049  label="H_element : 026"  # scripted group (container) (typed FeaturePython)
  n = 2
  ref = H_element
FEATURE [App::DocumentObjectGroupPython] G4_LITHIUM_AMIDE  # scripted group (container) (typed FeaturePython)
  Dunit = g/cm3
  Dvalue = 1.178
  Group = -> [Li_element001,N_element022,H_element049]
  conduct = 2
  density = 1
  expand = 3
  formula = G4_LITHIUM_AMIDE
  name = G4_LITHIUM_AMIDE
  specific = 4
FEATURE [App::DocumentObjectGroupPython] Li_element002  label="Li_element : 2"  # scripted group (container) (typed FeaturePython)
  n = 2
  ref = Li_element
FEATURE [App::DocumentObjectGroupPython] C_element055  label="C_element : 030"  # scripted group (container) (typed FeaturePython)
  n = 1
  ref = C_element
FEATURE [App::DocumentObjectGroupPython] O_element054  label="O_element : 028"  # scripted group (container) (typed FeaturePython)
  n = 3
  ref = O_element
FEATURE [App::DocumentObjectGroupPython] G4_LITHIUM_CARBONATE  # scripted group (container) (typed FeaturePython)
  Dunit = g/cm3
  Dvalue = 2.11
  Group = -> [Li_element002,C_element055,O_element054]
  conduct = 2
  density = 1
  expand = 3
  formula = G4_LITHIUM_CARBONATE
  name = G4_LITHIUM_CARBONATE
  specific = 4
FEATURE [App::DocumentObjectGroupPython] Li_element003  label="Li_element : 003"  # scripted group (container) (typed FeaturePython)
  n = 1
  ref = Li_element
FEATURE [App::DocumentObjectGroupPython] F_element012  label="F_element : 004"  # scripted group (container) (typed FeaturePython)
  n = 1
  ref = F_element
FEATURE [App::DocumentObjectGroupPython] G4_LITHIUM_FLUORIDE  # scripted group (container) (typed FeaturePython)
  Dunit = g/cm3
  Dvalue = 2.635
  Group = -> [Li_element003,F_element012]
  conduct = 2
  density = 1
  expand = 3
  formula = G4_LITHIUM_FLUORIDE
  name = G4_LITHIUM_FLUORIDE
  specific = 4
FEATURE [App::DocumentObjectGroupPython] Li_element004  label="Li_element : 004"  # scripted group (container) (typed FeaturePython)
  n = 1
  ref = Li_element
FEATURE [App::DocumentObjectGroupPython] H_element050  label="H_element : 027"  # scripted group (container) (typed FeaturePython)
  n = 1
  ref = H_element
FEATURE [App::DocumentObjectGroupPython] G4_LITHIUM_HYDRIDE  # scripted group (container) (typed FeaturePython)
  Dunit = g/cm3
  Dvalue = 0.82
  Group = -> [Li_element004,H_element050]
  conduct = 2
  density = 1
  expand = 3
  formula = G4_LITHIUM_HYDRIDE
  name = G4_LITHIUM_HYDRIDE
  specific = 4
FEATURE [App::DocumentObjectGroupPython] Li_element005  label="Li_element : 005"  # scripted group (container) (typed FeaturePython)
  n = 1
  ref = Li_element
FEATURE [App::DocumentObjectGroupPython] I_element003  label="I_element : 002"  # scripted group (container) (typed FeaturePython)
  n = 1
  ref = I_element
FEATURE [App::DocumentObjectGroupPython] G4_LITHIUM_IODIDE  # scripted group (container) (typed FeaturePython)
  Dunit = g/cm3
  Dvalue = 3.494
  Group = -> [Li_element005,I_element003]
  conduct = 2
  density = 1
  expand = 3
  formula = G4_LITHIUM_IODIDE
  name = G4_LITHIUM_IODIDE
  specific = 4
FEATURE [App::DocumentObjectGroupPython] Li_element006  label="Li_element : 006"  # scripted group (container) (typed FeaturePython)
  n = 2
  ref = Li_element
FEATURE [App::DocumentObjectGroupPython] O_element055  label="O_element : 029"  # scripted group (container) (typed FeaturePython)
  n = 1
  ref = O_element
FEATURE [App::DocumentObjectGroupPython] G4_LITHIUM_OXIDE  # scripted group (container) (typed FeaturePython)
  Dunit = g/cm3
  Dvalue = 2.013
  Group = -> [Li_element006,O_element055]
  conduct = 2
  density = 1
  expand = 3
  formula = G4_LITHIUM_OXIDE
  name = G4_LITHIUM_OXIDE
  specific = 4
FEATURE [App::DocumentObjectGroupPython] Li_element007  label="Li_element : 007"  # scripted group (container) (typed FeaturePython)
  n = 2
  ref = Li_element
FEATURE [App::DocumentObjectGroupPython] B_element005  label="B_element : 005"  # scripted group (container) (typed FeaturePython)
  n = 4
  ref = B_element
FEATURE [App::DocumentObjectGroupPython] O_element056  label="O_element : 7"  # scripted group (container) (typed FeaturePython)
  n = 7
  ref = O_element
FEATURE [App::DocumentObjectGroupPython] G4_LITHIUM_TETRABORATE  # scripted group (container) (typed FeaturePython)
  Dunit = g/cm3
  Dvalue = 2.44
  Group = -> [Li_element007,B_element005,O_element056]
  conduct = 2
  density = 1
  expand = 3
  formula = G4_LITHIUM_TETRABORATE
  name = G4_LITHIUM_TETRABORATE
  specific = 4
FEATURE [App::DocumentObjectGroupPython] H_element051  label="H_element : 0.105"  # scripted group (container) (typed FeaturePython)
  n = 0.105
FEATURE [App::DocumentObjectGroupPython] C_element056  label="C_element : 0.083"  # scripted group (container) (typed FeaturePython)
  n = 0.083
FEATURE [App::DocumentObjectGroupPython] N_element023  label="N_element : 0.023"  # scripted group (container) (typed FeaturePython)
  n = 0.023
FEATURE [App::DocumentObjectGroupPython] O_element057  label="O_element : 0.779"  # scripted group (container) (typed FeaturePython)
  n = 0.779
FEATURE [App::DocumentObjectGroupPython] Na_element010  label="Na_element : 0.097"  # scripted group (container) (typed FeaturePython)
  n = 0.002
FEATURE [App::DocumentObjectGroupPython] P_element006  label="P_element : 0.105"  # scripted group (container) (typed FeaturePython)
  n = 0.001
FEATURE [App::DocumentObjectGroupPython] S_element016  label="S_element : 0.017"  # scripted group (container) (typed FeaturePython)
  n = 0.002
FEATURE [App::DocumentObjectGroupPython] Cl_element014  label="Cl_element : 0.587"  # scripted group (container) (typed FeaturePython)
  n = 0.003
FEATURE [App::DocumentObjectGroupPython] K_element005  label="K_element : 0.015"  # scripted group (container) (typed FeaturePython)
  n = 0.002
FEATURE [App::DocumentObjectGroupPython] G4_LUNG_ICRP  # scripted group (container) (typed FeaturePython)
  Dunit = g/cm3
  Dvalue = 1.04
  Group = -> [H_element051,C_element056,N_element023,O_element057,Na_element010,P_element006,S_element016,Cl_element014,K_element005]
  conduct = 2
  density = 1
  expand = 3
  formula = G4_LUNG_ICRP
  name = G4_LUNG_ICRP
  specific = 4
FEATURE [App::DocumentObjectGroupPython] H_element052  label="H_element : 0.116"  # scripted group (container) (typed FeaturePython)
  n = 0.114318
FEATURE [App::DocumentObjectGroupPython] C_element057  label="C_element : 0.656"  # scripted group (container) (typed FeaturePython)
  n = 0.655824
FEATURE [App::DocumentObjectGroupPython] O_element058  label="O_element : 0.092"  # scripted group (container) (typed FeaturePython)
  n = 0.0921831
FEATURE [App::DocumentObjectGroupPython] Mg_element004  label="Mg_element : 0.135"  # scripted group (container) (typed FeaturePython)
  n = 0.134792
FEATURE [App::DocumentObjectGroupPython] Ca_element013  label="Ca_element : 0.003"  # scripted group (container) (typed FeaturePython)
  n = 0.002883
FEATURE [App::DocumentObjectGroupPython] G4_M3_WAX  # scripted group (container) (typed FeaturePython)
  Dunit = g/cm3
  Dvalue = 1.05
  Group = -> [H_element052,C_element057,O_element058,Mg_element004,Ca_element013]
  conduct = 2
  density = 1
  expand = 3
  formula = G4_M3_WAX
  name = G4_M3_WAX
  specific = 4
FEATURE [App::DocumentObjectGroupPython] Mg_element005  label="Mg_element : 1"  # scripted group (container) (typed FeaturePython)
  n = 1
  ref = Mg_element
FEATURE [App::DocumentObjectGroupPython] C_element058  label="C_element : 031"  # scripted group (container) (typed FeaturePython)
  n = 1
  ref = C_element
FEATURE [App::DocumentObjectGroupPython] O_element059  label="O_element : 030"  # scripted group (container) (typed FeaturePython)
  n = 3
  ref = O_element
FEATURE [App::DocumentObjectGroupPython] G4_MAGNESIUM_CARBONATE  # scripted group (container) (typed FeaturePython)
  Dunit = g/cm3
  Dvalue = 2.958
  Group = -> [Mg_element005,C_element058,O_element059]
  conduct = 2
  density = 1
  expand = 3
  formula = G4_MAGNESIUM_CARBONATE
  name = G4_MAGNESIUM_CARBONATE
  specific = 4
FEATURE [App::DocumentObjectGroupPython] Mg_element006  label="Mg_element : 002"  # scripted group (container) (typed FeaturePython)
  n = 1
  ref = Mg_element
FEATURE [App::DocumentObjectGroupPython] F_element013  label="F_element : 005"  # scripted group (container) (typed FeaturePython)
  n = 2
  ref = F_element
FEATURE [App::DocumentObjectGroupPython] G4_MAGNESIUM_FLUORIDE  # scripted group (container) (typed FeaturePython)
  Dunit = g/cm3
  Dvalue = 3
  Group = -> [Mg_element006,F_element013]
  conduct = 2
  density = 1
  expand = 3
  formula = G4_MAGNESIUM_FLUORIDE
  name = G4_MAGNESIUM_FLUORIDE
  specific = 4
FEATURE [App::DocumentObjectGroupPython] Mg_element007  label="Mg_element : 003"  # scripted group (container) (typed FeaturePython)
  n = 1
  ref = Mg_element
FEATURE [App::DocumentObjectGroupPython] O_element060  label="O_element : 031"  # scripted group (container) (typed FeaturePython)
  n = 1
  ref = O_element
FEATURE [App::DocumentObjectGroupPython] G4_MAGNESIUM_OXIDE  # scripted group (container) (typed FeaturePython)
  Dunit = g/cm3
  Dvalue = 3.58
  Group = -> [Mg_element007,O_element060]
  conduct = 2
  density = 1
  expand = 3
  formula = G4_MAGNESIUM_OXIDE
  name = G4_MAGNESIUM_OXIDE
  specific = 4
FEATURE [App::DocumentObjectGroupPython] Mg_element008  label="Mg_element : 004"  # scripted group (container) (typed FeaturePython)
  n = 1
  ref = Mg_element
FEATURE [App::DocumentObjectGroupPython] B_element006  label="B_element : 006"  # scripted group (container) (typed FeaturePython)
  n = 4
  ref = B_element
FEATURE [App::DocumentObjectGroupPython] O_element061  label="O_element : 032"  # scripted group (container) (typed FeaturePython)
  n = 7
  ref = O_element
FEATURE [App::DocumentObjectGroupPython] G4_MAGNESIUM_TETRABORATE  # scripted group (container) (typed FeaturePython)
  Dunit = g/cm3
  Dvalue = 2.53
  Group = -> [Mg_element008,B_element006,O_element061]
  conduct = 2
  density = 1
  expand = 3
  formula = G4_MAGNESIUM_TETRABORATE
  name = G4_MAGNESIUM_TETRABORATE
  specific = 4
FEATURE [App::DocumentObjectGroupPython] Hg_element001  label="Hg_element : 1"  # scripted group (container) (typed FeaturePython)
  n = 1
  ref = Hg_element
FEATURE [App::DocumentObjectGroupPython] I_element004  label="I_element : 2"  # scripted group (container) (typed FeaturePython)
  n = 2
  ref = I_element
FEATURE [App::DocumentObjectGroupPython] G4_MERCURIC_IODIDE  # scripted group (container) (typed FeaturePython)
  Dunit = g/cm3
  Dvalue = 6.36
  Group = -> [Hg_element001,I_element004]
  conduct = 2
  density = 1
  expand = 3
  formula = G4_MERCURIC_IODIDE
  name = G4_MERCURIC_IODIDE
  specific = 4
FEATURE [App::DocumentObjectGroupPython] C_element059  label="C_element : 032"  # scripted group (container) (typed FeaturePython)
  n = 1
  ref = C_element
FEATURE [App::DocumentObjectGroupPython] H_element053  label="H_element : 028"  # scripted group (container) (typed FeaturePython)
  n = 4
  ref = H_element
FEATURE [App::DocumentObjectGroupPython] G4_METHANE  # scripted group (container) (typed FeaturePython)
  Dunit = g/cm3
  Dvalue = 0.000667151
  Group = -> [C_element059,H_element053]
  conduct = 2
  density = 1
  expand = 3
  formula = G4_METHANE
  name = G4_METHANE
  specific = 4
FEATURE [App::DocumentObjectGroupPython] C_element060  label="C_element : 033"  # scripted group (container) (typed FeaturePython)
  n = 1
  ref = C_element
FEATURE [App::DocumentObjectGroupPython] H_element054  label="H_element : 029"  # scripted group (container) (typed FeaturePython)
  n = 4
  ref = H_element
FEATURE [App::DocumentObjectGroupPython] O_element062  label="O_element : 033"  # scripted group (container) (typed FeaturePython)
  n = 1
  ref = O_element
FEATURE [App::DocumentObjectGroupPython] G4_METHANOL  # scripted group (container) (typed FeaturePython)
  Dunit = g/cm3
  Dvalue = 0.7914
  Group = -> [C_element060,H_element054,O_element062]
  conduct = 2
  density = 1
  expand = 3
  formula = G4_METHANOL
  name = G4_METHANOL
  specific = 4
FEATURE [App::DocumentObjectGroupPython] H_element055  label="H_element : 0.134"  # scripted group (container) (typed FeaturePython)
  n = 0.13404
FEATURE [App::DocumentObjectGroupPython] C_element061  label="C_element : 0.778"  # scripted group (container) (typed FeaturePython)
  n = 0.77796
FEATURE [App::DocumentObjectGroupPython] O_element063  label="O_element : 0.035"  # scripted group (container) (typed FeaturePython)
  n = 0.03502
FEATURE [App::DocumentObjectGroupPython] Mg_element009  label="Mg_element : 0.039"  # scripted group (container) (typed FeaturePython)
  n = 0.038594
FEATURE [App::DocumentObjectGroupPython] Ti_element002  label="Ti_element : 0.014"  # scripted group (container) (typed FeaturePython)
  n = 0.014386
FEATURE [App::DocumentObjectGroupPython] G4_MIX_D_WAX  # scripted group (container) (typed FeaturePython)
  Dunit = g/cm3
  Dvalue = 0.99
  Group = -> [H_element055,C_element061,O_element063,Mg_element009,Ti_element002]
  conduct = 2
  density = 1
  expand = 3
  formula = G4_MIX_D_WAX
  name = G4_MIX_D_WAX
  specific = 4
FEATURE [App::DocumentObjectGroupPython] H_element056  label="H_element : 0.135"  # scripted group (container) (typed FeaturePython)
  n = 0.081192
FEATURE [App::DocumentObjectGroupPython] C_element062  label="C_element : 0.583"  # scripted group (container) (typed FeaturePython)
  n = 0.583442
FEATURE [App::DocumentObjectGroupPython] N_element024  label="N_element : 0.018"  # scripted group (container) (typed FeaturePython)
  n = 0.017798
FEATURE [App::DocumentObjectGroupPython] O_element064  label="O_element : 0.186"  # scripted group (container) (typed FeaturePython)
  n = 0.186381
FEATURE [App::DocumentObjectGroupPython] Mg_element010  label="Mg_element : 0.130"  # scripted group (container) (typed FeaturePython)
  n = 0.130287
FEATURE [App::DocumentObjectGroupPython] Cl_element015  label="Cl_element : 0.588"  # scripted group (container) (typed FeaturePython)
  n = 0.0009
FEATURE [App::DocumentObjectGroupPython] G4_MS20_TISSUE  # scripted group (container) (typed FeaturePython)
  Dunit = g/cm3
  Dvalue = 1
  Group = -> [H_element056,C_element062,N_element024,O_element064,Mg_element010,Cl_element015]
  conduct = 2
  density = 1
  expand = 3
  formula = G4_MS20_TISSUE
  name = G4_MS20_TISSUE
  specific = 4
FEATURE [App::DocumentObjectGroupPython] H_element057  label="H_element : 0.136"  # scripted group (container) (typed FeaturePython)
  n = 0.102
FEATURE [App::DocumentObjectGroupPython] C_element063  label="C_element : 0.143"  # scripted group (container) (typed FeaturePython)
  n = 0.143
FEATURE [App::DocumentObjectGroupPython] N_element025  label="N_element : 0.034"  # scripted group (container) (typed FeaturePython)
  n = 0.034
FEATURE [App::DocumentObjectGroupPython] O_element065  label="O_element : 0.710"  # scripted group (container) (typed FeaturePython)
  n = 0.71
FEATURE [App::DocumentObjectGroupPython] Na_element011  label="Na_element : 0.098"  # scripted group (container) (typed FeaturePython)
  n = 0.001
FEATURE [App::DocumentObjectGroupPython] P_element007  label="P_element : 0.002"  # scripted group (container) (typed FeaturePython)
  n = 0.002
FEATURE [App::DocumentObjectGroupPython] S_element017  label="S_element : 0.018"  # scripted group (container) (typed FeaturePython)
  n = 0.003
FEATURE [App::DocumentObjectGroupPython] Cl_element016  label="Cl_element : 0.589"  # scripted group (container) (typed FeaturePython)
  n = 0.001
FEATURE [App::DocumentObjectGroupPython] K_element006  label="K_element : 0.004"  # scripted group (container) (typed FeaturePython)
  n = 0.004
FEATURE [App::DocumentObjectGroupPython] G4_MUSCLE_SKELETAL_ICRP  # scripted group (container) (typed FeaturePython)
  Dunit = g/cm3
  Dvalue = 1.05
  Group = -> [H_element057,C_element063,N_element025,O_element065,Na_element011,P_element007,S_element017,Cl_element016,K_element006]
  conduct = 2
  density = 1
  expand = 3
  formula = G4_MUSCLE_SKELETAL_ICRP
  name = G4_MUSCLE_SKELETAL_ICRP
  specific = 4
FEATURE [App::DocumentObjectGroupPython] H_element058  label="H_element : 0.137"  # scripted group (container) (typed FeaturePython)
  n = 0.102102
FEATURE [App::DocumentObjectGroupPython] C_element064  label="C_element : 0.123"  # scripted group (container) (typed FeaturePython)
  n = 0.123123
FEATURE [App::DocumentObjectGroupPython] N_element026  label="N_element : 0.756"  # scripted group (container) (typed FeaturePython)
  n = 0.035035
FEATURE [App::DocumentObjectGroupPython] O_element066  label="O_element : 0.730"  # scripted group (container) (typed FeaturePython)
  n = 0.72973
FEATURE [App::DocumentObjectGroupPython] Na_element012  label="Na_element : 0.099"  # scripted group (container) (typed FeaturePython)
  n = 0.001001
FEATURE [App::DocumentObjectGroupPython] P_element008  label="P_element : 0.106"  # scripted group (container) (typed FeaturePython)
  n = 0.002002
FEATURE [App::DocumentObjectGroupPython] S_element018  label="S_element : 0.019"  # scripted group (container) (typed FeaturePython)
  n = 0.004004
FEATURE [App::DocumentObjectGroupPython] K_element007  label="K_element : 0.016"  # scripted group (container) (typed FeaturePython)
  n = 0.003003
FEATURE [App::DocumentObjectGroupPython] G4_MUSCLE_STRIATED_ICRU  # scripted group (container) (typed FeaturePython)
  Dunit = g/cm3
  Dvalue = 1.04
  Group = -> [H_element058,C_element064,N_element026,O_element066,Na_element012,P_element008,S_element018,K_element007]
  conduct = 2
  density = 1
  expand = 3
  formula = G4_MUSCLE_STRIATED_ICRU
  name = G4_MUSCLE_STRIATED_ICRU
  specific = 4
FEATURE [App::DocumentObjectGroupPython] H_element059  label="H_element : 0.098"  # scripted group (container) (typed FeaturePython)
  n = 0.0982341
FEATURE [App::DocumentObjectGroupPython] C_element065  label="C_element : 0.156"  # scripted group (container) (typed FeaturePython)
  n = 0.156214
FEATURE [App::DocumentObjectGroupPython] N_element027  label="N_element : 0.757"  # scripted group (container) (typed FeaturePython)
  n = 0.035451
FEATURE [App::DocumentObjectGroupPython] O_element067  label="O_element : 0.880"  # scripted group (container) (typed FeaturePython)
  n = 0.710101
FEATURE [App::DocumentObjectGroupPython] G4_MUSCLE_WITH_SUCROSE  # scripted group (container) (typed FeaturePython)
  Dunit = g/cm3
  Dvalue = 1.11
  Group = -> [H_element059,C_element065,N_element027,O_element067]
  conduct = 2
  density = 1
  expand = 3
  formula = G4_MUSCLE_WITH_SUCROSE
  name = G4_MUSCLE_WITH_SUCROSE
  specific = 4
FEATURE [App::DocumentObjectGroupPython] H_element060  label="H_element : 0.138"  # scripted group (container) (typed FeaturePython)
  n = 0.101969
FEATURE [App::DocumentObjectGroupPython] C_element066  label="C_element : 0.120"  # scripted group (container) (typed FeaturePython)
  n = 0.120058
FEATURE [App::DocumentObjectGroupPython] N_element028  label="N_element : 0.758"  # scripted group (container) (typed FeaturePython)
  n = 0.035451
FEATURE [App::DocumentObjectGroupPython] O_element068  label="O_element : 0.743"  # scripted group (container) (typed FeaturePython)
  n = 0.742522
FEATURE [App::DocumentObjectGroupPython] G4_MUSCLE_WITHOUT_SUCROSE  # scripted group (container) (typed FeaturePython)
  Dunit = g/cm3
  Dvalue = 1.07
  Group = -> [H_element060,C_element066,N_element028,O_element068]
  conduct = 2
  density = 1
  expand = 3
  formula = G4_MUSCLE_WITHOUT_SUCROSE
  name = G4_MUSCLE_WITHOUT_SUCROSE
  specific = 4
FEATURE [App::DocumentObjectGroupPython] C_element067  label="C_element : 10"  # scripted group (container) (typed FeaturePython)
  n = 10
  ref = C_element
FEATURE [App::DocumentObjectGroupPython] H_element061  label="H_element : 030"  # scripted group (container) (typed FeaturePython)
  n = 8
  ref = H_element
FEATURE [App::DocumentObjectGroupPython] G4_NAPHTHALENE  # scripted group (container) (typed FeaturePython)
  Dunit = g/cm3
  Dvalue = 1.145
  Group = -> [C_element067,H_element061]
  conduct = 2
  density = 1
  expand = 3
  formula = G4_NAPHTHALENE
  name = G4_NAPHTHALENE
  specific = 4
FEATURE [App::DocumentObjectGroupPython] C_element068  label="C_element : 034"  # scripted group (container) (typed FeaturePython)
  n = 6
  ref = C_element
FEATURE [App::DocumentObjectGroupPython] H_element062  label="H_element : 031"  # scripted group (container) (typed FeaturePython)
  n = 5
  ref = H_element
FEATURE [App::DocumentObjectGroupPython] N_element029  label="N_element : 012"  # scripted group (container) (typed FeaturePython)
  n = 1
  ref = N_element
FEATURE [App::DocumentObjectGroupPython] O_element069  label="O_element : 034"  # scripted group (container) (typed FeaturePython)
  n = 2
  ref = O_element
FEATURE [App::DocumentObjectGroupPython] G4_NITROBENZENE  # scripted group (container) (typed FeaturePython)
  Dunit = g/cm3
  Dvalue = 1.19867
  Group = -> [C_element068,H_element062,N_element029,O_element069]
  conduct = 2
  density = 1
  expand = 3
  formula = G4_NITROBENZENE
  name = G4_NITROBENZENE
  specific = 4
FEATURE [App::DocumentObjectGroupPython] N_element030  label="N_element : 013"  # scripted group (container) (typed FeaturePython)
  n = 2
  ref = N_element
FEATURE [App::DocumentObjectGroupPython] O_element070  label="O_element : 035"  # scripted group (container) (typed FeaturePython)
  n = 1
  ref = O_element
FEATURE [App::DocumentObjectGroupPython] G4_NITROUS_OXIDE  # scripted group (container) (typed FeaturePython)
  Dunit = g/cm3
  Dvalue = 0.00183094
  Group = -> [N_element030,O_element070]
  conduct = 2
  density = 1
  expand = 3
  formula = G4_NITROUS_OXIDE
  name = G4_NITROUS_OXIDE
  specific = 4
FEATURE [App::DocumentObjectGroupPython] H_element063  label="H_element : 0.104"  # scripted group (container) (typed FeaturePython)
  n = 0.103509
FEATURE [App::DocumentObjectGroupPython] C_element069  label="C_element : 0.648"  # scripted group (container) (typed FeaturePython)
  n = 0.648416
FEATURE [App::DocumentObjectGroupPython] N_element031  label="N_element : 0.100"  # scripted group (container) (typed FeaturePython)
  n = 0.0995361
FEATURE [App::DocumentObjectGroupPython] O_element071  label="O_element : 0.149"  # scripted group (container) (typed FeaturePython)
  n = 0.148539
FEATURE [App::DocumentObjectGroupPython] G4_NYLON_8062  label="G4_NYLON-8062"  # scripted group (container) (typed FeaturePython)
  Dunit = g/cm3
  Dvalue = 1.08
  Group = -> [H_element063,C_element069,N_element031,O_element071]
  conduct = 2
  density = 1
  expand = 3
  formula = G4_NYLON-8062
  name = G4_NYLON-8062
  specific = 4
FEATURE [App::DocumentObjectGroupPython] C_element070  label="C_element : 035"  # scripted group (container) (typed FeaturePython)
  n = 6
  ref = C_element
FEATURE [App::DocumentObjectGroupPython] H_element064  label="H_element : 11"  # scripted group (container) (typed FeaturePython)
  n = 11
  ref = H_element
FEATURE [App::DocumentObjectGroupPython] N_element032  label="N_element : 014"  # scripted group (container) (typed FeaturePython)
  n = 1
  ref = N_element
FEATURE [App::DocumentObjectGroupPython] O_element072  label="O_element : 036"  # scripted group (container) (typed FeaturePython)
  n = 1
  ref = O_element
FEATURE [App::DocumentObjectGroupPython] G4_NYLON_6_6  label="G4_NYLON-6-6"  # scripted group (container) (typed FeaturePython)
  Dunit = g/cm3
  Dvalue = 1.14
  Group = -> [C_element070,H_element064,N_element032,O_element072]
  conduct = 2
  density = 1
  expand = 3
  formula = G4_NYLON-6-6
  name = G4_NYLON-6-6
  specific = 4
FEATURE [App::DocumentObjectGroupPython] H_element065  label="H_element : 0.139"  # scripted group (container) (typed FeaturePython)
  n = 0.107062
FEATURE [App::DocumentObjectGroupPython] C_element071  label="C_element : 0.680"  # scripted group (container) (typed FeaturePython)
  n = 0.680449
FEATURE [App::DocumentObjectGroupPython] N_element033  label="N_element : 0.099"  # scripted group (container) (typed FeaturePython)
  n = 0.099189
FEATURE [App::DocumentObjectGroupPython] O_element073  label="O_element : 0.113"  # scripted group (container) (typed FeaturePython)
  n = 0.1133
FEATURE [App::DocumentObjectGroupPython] G4_NYLON_6_10  label="G4_NYLON-6-10"  # scripted group (container) (typed FeaturePython)
  Dunit = g/cm3
  Dvalue = 1.14
  Group = -> [H_element065,C_element071,N_element033,O_element073]
  conduct = 2
  density = 1
  expand = 3
  formula = G4_NYLON-6-10
  name = G4_NYLON-6-10
  specific = 4
FEATURE [App::DocumentObjectGroupPython] H_element066  label="H_element : 0.140"  # scripted group (container) (typed FeaturePython)
  n = 0.115476
FEATURE [App::DocumentObjectGroupPython] C_element072  label="C_element : 0.721"  # scripted group (container) (typed FeaturePython)
  n = 0.720818
FEATURE [App::DocumentObjectGroupPython] N_element034  label="N_element : 0.076"  # scripted group (container) (typed FeaturePython)
  n = 0.0764169
FEATURE [App::DocumentObjectGroupPython] O_element074  label="O_element : 0.087"  # scripted group (container) (typed FeaturePython)
  n = 0.0872889
FEATURE [App::DocumentObjectGroupPython] G4_NYLON_11_RILSAN  label="G4_NYLON-11_RILSAN"  # scripted group (container) (typed FeaturePython)
  Dunit = g/cm3
  Dvalue = 1.425
  Group = -> [H_element066,C_element072,N_element034,O_element074]
  conduct = 2
  density = 1
  expand = 3
  formula = G4_NYLON-11_RILSAN
  name = G4_NYLON-11_RILSAN
  specific = 4
FEATURE [App::DocumentObjectGroupPython] C_element073  label="C_element : 8"  # scripted group (container) (typed FeaturePython)
  n = 8
  ref = C_element
FEATURE [App::DocumentObjectGroupPython] H_element067  label="H_element : 18"  # scripted group (container) (typed FeaturePython)
  n = 18
  ref = H_element
FEATURE [App::DocumentObjectGroupPython] G4_OCTANE  # scripted group (container) (typed FeaturePython)
  Dunit = g/cm3
  Dvalue = 0.7026
  Group = -> [C_element073,H_element067]
  conduct = 2
  density = 1
  expand = 3
  formula = G4_OCTANE
  name = G4_OCTANE
  specific = 4
FEATURE [App::DocumentObjectGroupPython] C_element074  label="C_element : 25"  # scripted group (container) (typed FeaturePython)
  n = 25
  ref = C_element
FEATURE [App::DocumentObjectGroupPython] H_element068  label="H_element : 52"  # scripted group (container) (typed FeaturePython)
  n = 52
  ref = H_element
FEATURE [App::DocumentObjectGroupPython] G4_PARAFFIN  # scripted group (container) (typed FeaturePython)
  Dunit = g/cm3
  Dvalue = 0.93
  Group = -> [C_element074,H_element068]
  conduct = 2
  density = 1
  expand = 3
  formula = G4_PARAFFIN
  name = G4_PARAFFIN
  specific = 4
FEATURE [App::DocumentObjectGroupPython] C_element075  label="C_element : 036"  # scripted group (container) (typed FeaturePython)
  n = 5
  ref = C_element
FEATURE [App::DocumentObjectGroupPython] H_element069  label="H_element : 032"  # scripted group (container) (typed FeaturePython)
  n = 12
  ref = H_element
FEATURE [App::DocumentObjectGroupPython] G4_N_PENTANE  label="G4_N-PENTANE"  # scripted group (container) (typed FeaturePython)
  Dunit = g/cm3
  Dvalue = 0.6262
  Group = -> [C_element075,H_element069]
  conduct = 2
  density = 1
  expand = 3
  formula = G4_N-PENTANE
  name = G4_N-PENTANE
  specific = 4
FEATURE [App::DocumentObjectGroupPython] H_element070  label="H_element : 0.014"  # scripted group (container) (typed FeaturePython)
  n = 0.0141
FEATURE [App::DocumentObjectGroupPython] C_element076  label="C_element : 0.072"  # scripted group (container) (typed FeaturePython)
  n = 0.072261
FEATURE [App::DocumentObjectGroupPython] N_element035  label="N_element : 0.019"  # scripted group (container) (typed FeaturePython)
  n = 0.01932
FEATURE [App::DocumentObjectGroupPython] O_element075  label="O_element : 0.066"  # scripted group (container) (typed FeaturePython)
  n = 0.066101
FEATURE [App::DocumentObjectGroupPython] S_element019  label="S_element : 0.020"  # scripted group (container) (typed FeaturePython)
  n = 0.00189
FEATURE [App::DocumentObjectGroupPython] Br_element004  label="Br_element : 0.349"  # scripted group (container) (typed FeaturePython)
  n = 0.349103
FEATURE [App::DocumentObjectGroupPython] Ag_element001  label="Ag_element : 0.474"  # scripted group (container) (typed FeaturePython)
  n = 0.474105
FEATURE [App::DocumentObjectGroupPython] I_element005  label="I_element : 0.003"  # scripted group (container) (typed FeaturePython)
  n = 0.00312
FEATURE [App::DocumentObjectGroupPython] G4_PHOTO_EMULSION  # scripted group (container) (typed FeaturePython)
  Dunit = g/cm3
  Dvalue = 3.815
  Group = -> [H_element070,C_element076,N_element035,O_element075,S_element019,Br_element004,Ag_element001,I_element005]
  conduct = 2
  density = 1
  expand = 3
  formula = G4_PHOTO_EMULSION
  name = G4_PHOTO_EMULSION
  specific = 4
FEATURE [App::DocumentObjectGroupPython] C_element077  label="C_element : 9"  # scripted group (container) (typed FeaturePython)
  n = 9
  ref = C_element
FEATURE [App::DocumentObjectGroupPython] H_element071  label="H_element : 033"  # scripted group (container) (typed FeaturePython)
  n = 10
  ref = H_element
FEATURE [App::DocumentObjectGroupPython] G4_PLASTIC_SC_VINYLTOLUENE  # scripted group (container) (typed FeaturePython)
  Dunit = g/cm3
  Dvalue = 1.032
  Group = -> [C_element077,H_element071]
  conduct = 2
  density = 1
  expand = 3
  formula = G4_PLASTIC_SC_VINYLTOLUENE
  name = G4_PLASTIC_SC_VINYLTOLUENE
  specific = 4
FEATURE [App::DocumentObjectGroupPython] Pu_element001  label="Pu_element : 1"  # scripted group (container) (typed FeaturePython)
  n = 1
  ref = Pu_element
FEATURE [App::DocumentObjectGroupPython] O_element076  label="O_element : 037"  # scripted group (container) (typed FeaturePython)
  n = 2
  ref = O_element
FEATURE [App::DocumentObjectGroupPython] G4_PLUTONIUM_DIOXIDE  # scripted group (container) (typed FeaturePython)
  Dunit = g/cm3
  Dvalue = 11.46
  Group = -> [Pu_element001,O_element076]
  conduct = 2
  density = 1
  expand = 3
  formula = G4_PLUTONIUM_DIOXIDE
  name = G4_PLUTONIUM_DIOXIDE
  specific = 4
FEATURE [App::DocumentObjectGroupPython] C_element078  label="C_element : 037"  # scripted group (container) (typed FeaturePython)
  n = 3
  ref = C_element
FEATURE [App::DocumentObjectGroupPython] H_element072  label="H_element : 034"  # scripted group (container) (typed FeaturePython)
  n = 3
  ref = H_element
FEATURE [App::DocumentObjectGroupPython] N_element036  label="N_element : 015"  # scripted group (container) (typed FeaturePython)
  n = 1
  ref = N_element
FEATURE [App::DocumentObjectGroupPython] G4_POLYACRYLONITRILE  # scripted group (container) (typed FeaturePython)
  Dunit = g/cm3
  Dvalue = 1.17
  Group = -> [C_element078,H_element072,N_element036]
  conduct = 2
  density = 1
  expand = 3
  formula = G4_POLYACRYLONITRILE
  name = G4_POLYACRYLONITRILE
  specific = 4
FEATURE [App::DocumentObjectGroupPython] C_element079  label="C_element : 16"  # scripted group (container) (typed FeaturePython)
  n = 16
  ref = C_element
FEATURE [App::DocumentObjectGroupPython] H_element073  label="H_element : 035"  # scripted group (container) (typed FeaturePython)
  n = 14
  ref = H_element
FEATURE [App::DocumentObjectGroupPython] O_element077  label="O_element : 038"  # scripted group (container) (typed FeaturePython)
  n = 3
  ref = O_element
FEATURE [App::DocumentObjectGroupPython] G4_POLYCARBONATE  # scripted group (container) (typed FeaturePython)
  Dunit = g/cm3
  Dvalue = 1.2
  Group = -> [C_element079,H_element073,O_element077]
  conduct = 2
  density = 1
  expand = 3
  formula = G4_POLYCARBONATE
  name = G4_POLYCARBONATE
  specific = 4
FEATURE [App::DocumentObjectGroupPython] C_element080  label="C_element : 038"  # scripted group (container) (typed FeaturePython)
  n = 8
  ref = C_element
FEATURE [App::DocumentObjectGroupPython] H_element074  label="H_element : 036"  # scripted group (container) (typed FeaturePython)
  n = 7
  ref = H_element
FEATURE [App::DocumentObjectGroupPython] Cl_element017  label="Cl_element : 007"  # scripted group (container) (typed FeaturePython)
  n = 1
  ref = Cl_element
FEATURE [App::DocumentObjectGroupPython] G4_POLYCHLOROSTYRENE  # scripted group (container) (typed FeaturePython)
  Dunit = g/cm3
  Dvalue = 1.3
  Group = -> [C_element080,H_element074,Cl_element017]
  conduct = 2
  density = 1
  expand = 3
  formula = G4_POLYCHLOROSTYRENE
  name = G4_POLYCHLOROSTYRENE
  specific = 4
FEATURE [App::DocumentObjectGroupPython] C_element081  label="C_element : 039"  # scripted group (container) (typed FeaturePython)
  n = 1
  ref = C_element
FEATURE [App::DocumentObjectGroupPython] H_element075  label="H_element : 037"  # scripted group (container) (typed FeaturePython)
  n = 2
  ref = H_element
FEATURE [App::DocumentObjectGroupPython] G4_POLYETHYLENE  # scripted group (container) (typed FeaturePython)
  Dunit = g/cm3
  Dvalue = 0.94
  Group = -> [C_element081,H_element075]
  conduct = 2
  density = 1
  expand = 3
  formula = G4_POLYETHYLENE
  name = G4_POLYETHYLENE
  specific = 4
FEATURE [App::DocumentObjectGroupPython] C_element082  label="C_element : 040"  # scripted group (container) (typed FeaturePython)
  n = 10
  ref = C_element
FEATURE [App::DocumentObjectGroupPython] H_element076  label="H_element : 038"  # scripted group (container) (typed FeaturePython)
  n = 8
  ref = H_element
FEATURE [App::DocumentObjectGroupPython] O_element078  label="O_element : 039"  # scripted group (container) (typed FeaturePython)
  n = 4
  ref = O_element
FEATURE [App::DocumentObjectGroupPython] G4_MYLAR  # scripted group (container) (typed FeaturePython)
  Dunit = g/cm3
  Dvalue = 1.4
  Group = -> [C_element082,H_element076,O_element078]
  conduct = 2
  density = 1
  expand = 3
  formula = G4_MYLAR
  name = G4_MYLAR
  specific = 4
FEATURE [App::DocumentObjectGroupPython] C_element083  label="C_element : 041"  # scripted group (container) (typed FeaturePython)
  n = 5
  ref = C_element
FEATURE [App::DocumentObjectGroupPython] H_element077  label="H_element : 039"  # scripted group (container) (typed FeaturePython)
  n = 8
  ref = H_element
FEATURE [App::DocumentObjectGroupPython] O_element079  label="O_element : 040"  # scripted group (container) (typed FeaturePython)
  n = 2
  ref = O_element
FEATURE [App::DocumentObjectGroupPython] G4_PLEXIGLASS  # scripted group (container) (typed FeaturePython)
  Dunit = g/cm3
  Dvalue = 1.19
  Group = -> [C_element083,H_element077,O_element079]
  conduct = 2
  density = 1
  expand = 3
  formula = G4_PLEXIGLASS
  name = G4_PLEXIGLASS
  specific = 4
FEATURE [App::DocumentObjectGroupPython] C_element084  label="C_element : 042"  # scripted group (container) (typed FeaturePython)
  n = 1
  ref = C_element
FEATURE [App::DocumentObjectGroupPython] H_element078  label="H_element : 040"  # scripted group (container) (typed FeaturePython)
  n = 2
  ref = H_element
FEATURE [App::DocumentObjectGroupPython] O_element080  label="O_element : 041"  # scripted group (container) (typed FeaturePython)
  n = 1
  ref = O_element
FEATURE [App::DocumentObjectGroupPython] G4_POLYOXYMETHYLENE  # scripted group (container) (typed FeaturePython)
  Dunit = g/cm3
  Dvalue = 1.425
  Group = -> [C_element084,H_element078,O_element080]
  conduct = 2
  density = 1
  expand = 3
  formula = G4_POLYOXYMETHYLENE
  name = G4_POLYOXYMETHYLENE
  specific = 4
FEATURE [App::DocumentObjectGroupPython] C_element085  label="C_element : 043"  # scripted group (container) (typed FeaturePython)
  n = 2
  ref = C_element
FEATURE [App::DocumentObjectGroupPython] H_element079  label="H_element : 041"  # scripted group (container) (typed FeaturePython)
  n = 4
  ref = H_element
FEATURE [App::DocumentObjectGroupPython] G4_POLYPROPYLENE  # scripted group (container) (typed FeaturePython)
  Dunit = g/cm3
  Dvalue = 0.9
  Group = -> [C_element085,H_element079]
  conduct = 2
  density = 1
  expand = 3
  formula = G4_POLYPROPYLENE
  name = G4_POLYPROPYLENE
  specific = 4
FEATURE [App::DocumentObjectGroupPython] C_element086  label="C_element : 044"  # scripted group (container) (typed FeaturePython)
  n = 8
  ref = C_element
FEATURE [App::DocumentObjectGroupPython] H_element080  label="H_element : 042"  # scripted group (container) (typed FeaturePython)
  n = 8
  ref = H_element
FEATURE [App::DocumentObjectGroupPython] G4_POLYSTYRENE  # scripted group (container) (typed FeaturePython)
  Dunit = g/cm3
  Dvalue = 1.06
  Group = -> [C_element086,H_element080]
  conduct = 2
  density = 1
  expand = 3
  formula = G4_POLYSTYRENE
  name = G4_POLYSTYRENE
  specific = 4
FEATURE [App::DocumentObjectGroupPython] C_element087  label="C_element : 045"  # scripted group (container) (typed FeaturePython)
  n = 2
  ref = C_element
FEATURE [App::DocumentObjectGroupPython] F_element014  label="F_element : 4"  # scripted group (container) (typed FeaturePython)
  n = 4
  ref = F_element
FEATURE [App::DocumentObjectGroupPython] G4_TEFLON  # scripted group (container) (typed FeaturePython)
  Dunit = g/cm3
  Dvalue = 2.2
  Group = -> [C_element087,F_element014]
  conduct = 2
  density = 1
  expand = 3
  formula = G4_TEFLON
  name = G4_TEFLON
  specific = 4
FEATURE [App::DocumentObjectGroupPython] C_element088  label="C_element : 046"  # scripted group (container) (typed FeaturePython)
  n = 2
  ref = C_element
FEATURE [App::DocumentObjectGroupPython] F_element015  label="F_element : 006"  # scripted group (container) (typed FeaturePython)
  n = 3
  ref = F_element
FEATURE [App::DocumentObjectGroupPython] Cl_element018  label="Cl_element : 008"  # scripted group (container) (typed FeaturePython)
  n = 1
  ref = Cl_element
FEATURE [App::DocumentObjectGroupPython] G4_POLYTRIFLUOROCHLOROETHYLENE  # scripted group (container) (typed FeaturePython)
  Dunit = g/cm3
  Dvalue = 2.1
  Group = -> [C_element088,F_element015,Cl_element018]
  conduct = 2
  density = 1
  expand = 3
  formula = G4_POLYTRIFLUOROCHLOROETHYLENE
  name = G4_POLYTRIFLUOROCHLOROETHYLENE
  specific = 4
FEATURE [App::DocumentObjectGroupPython] C_element089  label="C_element : 047"  # scripted group (container) (typed FeaturePython)
  n = 4
  ref = C_element
FEATURE [App::DocumentObjectGroupPython] H_element081  label="H_element : 043"  # scripted group (container) (typed FeaturePython)
  n = 6
  ref = H_element
FEATURE [App::DocumentObjectGroupPython] O_element081  label="O_element : 042"  # scripted group (container) (typed FeaturePython)
  n = 2
  ref = O_element
FEATURE [App::DocumentObjectGroupPython] G4_POLYVINYL_ACETATE  # scripted group (container) (typed FeaturePython)
  Dunit = g/cm3
  Dvalue = 1.19
  Group = -> [C_element089,H_element081,O_element081]
  conduct = 2
  density = 1
  expand = 3
  formula = G4_POLYVINYL_ACETATE
  name = G4_POLYVINYL_ACETATE
  specific = 4
FEATURE [App::DocumentObjectGroupPython] C_element090  label="C_element : 048"  # scripted group (container) (typed FeaturePython)
  n = 2
  ref = C_element
FEATURE [App::DocumentObjectGroupPython] H_element082  label="H_element : 044"  # scripted group (container) (typed FeaturePython)
  n = 4
  ref = H_element
FEATURE [App::DocumentObjectGroupPython] O_element082  label="O_element : 043"  # scripted group (container) (typed FeaturePython)
  n = 1
  ref = O_element
FEATURE [App::DocumentObjectGroupPython] G4_POLYVINYL_ALCOHOL  # scripted group (container) (typed FeaturePython)
  Dunit = g/cm3
  Dvalue = 1.3
  Group = -> [C_element090,H_element082,O_element082]
  conduct = 2
  density = 1
  expand = 3
  formula = G4_POLYVINYL_ALCOHOL
  name = G4_POLYVINYL_ALCOHOL
  specific = 4
FEATURE [App::DocumentObjectGroupPython] C_element091  label="C_element : 049"  # scripted group (container) (typed FeaturePython)
  n = 8
  ref = C_element
FEATURE [App::DocumentObjectGroupPython] H_element083  label="H_element : 045"  # scripted group (container) (typed FeaturePython)
  n = 14
  ref = H_element
FEATURE [App::DocumentObjectGroupPython] O_element083  label="O_element : 044"  # scripted group (container) (typed FeaturePython)
  n = 2
  ref = O_element
FEATURE [App::DocumentObjectGroupPython] G4_POLYVINYL_BUTYRAL  # scripted group (container) (typed FeaturePython)
  Dunit = g/cm3
  Dvalue = 1.12
  Group = -> [C_element091,H_element083,O_element083]
  conduct = 2
  density = 1
  expand = 3
  formula = G4_POLYVINYL_BUTYRAL
  name = G4_POLYVINYL_BUTYRAL
  specific = 4
FEATURE [App::DocumentObjectGroupPython] C_element092  label="C_element : 050"  # scripted group (container) (typed FeaturePython)
  n = 2
  ref = C_element
FEATURE [App::DocumentObjectGroupPython] H_element084  label="H_element : 046"  # scripted group (container) (typed FeaturePython)
  n = 3
  ref = H_element
FEATURE [App::DocumentObjectGroupPython] Cl_element019  label="Cl_element : 009"  # scripted group (container) (typed FeaturePython)
  n = 1
  ref = Cl_element
FEATURE [App::DocumentObjectGroupPython] G4_POLYVINYL_CHLORIDE  # scripted group (container) (typed FeaturePython)
  Dunit = g/cm3
  Dvalue = 1.3
  Group = -> [C_element092,H_element084,Cl_element019]
  conduct = 2
  density = 1
  expand = 3
  formula = G4_POLYVINYL_CHLORIDE
  name = G4_POLYVINYL_CHLORIDE
  specific = 4
FEATURE [App::DocumentObjectGroupPython] C_element093  label="C_element : 051"  # scripted group (container) (typed FeaturePython)
  n = 2
  ref = C_element
FEATURE [App::DocumentObjectGroupPython] H_element085  label="H_element : 047"  # scripted group (container) (typed FeaturePython)
  n = 2
  ref = H_element
FEATURE [App::DocumentObjectGroupPython] Cl_element020  label="Cl_element : 010"  # scripted group (container) (typed FeaturePython)
  n = 2
  ref = Cl_element
FEATURE [App::DocumentObjectGroupPython] G4_POLYVINYLIDENE_CHLORIDE  # scripted group (container) (typed FeaturePython)
  Dunit = g/cm3
  Dvalue = 1.7
  Group = -> [C_element093,H_element085,Cl_element020]
  conduct = 2
  density = 1
  expand = 3
  formula = G4_POLYVINYLIDENE_CHLORIDE
  name = G4_POLYVINYLIDENE_CHLORIDE
  specific = 4
FEATURE [App::DocumentObjectGroupPython] C_element094  label="C_element : 052"  # scripted group (container) (typed FeaturePython)
  n = 2
  ref = C_element
FEATURE [App::DocumentObjectGroupPython] H_element086  label="H_element : 048"  # scripted group (container) (typed FeaturePython)
  n = 2
  ref = H_element
FEATURE [App::DocumentObjectGroupPython] F_element016  label="F_element : 007"  # scripted group (container) (typed FeaturePython)
  n = 2
  ref = F_element
FEATURE [App::DocumentObjectGroupPython] G4_POLYVINYLIDENE_FLUORIDE  # scripted group (container) (typed FeaturePython)
  Dunit = g/cm3
  Dvalue = 1.76
  Group = -> [C_element094,H_element086,F_element016]
  conduct = 2
  density = 1
  expand = 3
  formula = G4_POLYVINYLIDENE_FLUORIDE
  name = G4_POLYVINYLIDENE_FLUORIDE
  specific = 4
FEATURE [App::DocumentObjectGroupPython] C_element095  label="C_element : 053"  # scripted group (container) (typed FeaturePython)
  n = 6
  ref = C_element
FEATURE [App::DocumentObjectGroupPython] H_element087  label="H_element : 9"  # scripted group (container) (typed FeaturePython)
  n = 9
  ref = H_element
FEATURE [App::DocumentObjectGroupPython] N_element037  label="N_element : 016"  # scripted group (container) (typed FeaturePython)
  n = 1
  ref = N_element
FEATURE [App::DocumentObjectGroupPython] O_element084  label="O_element : 045"  # scripted group (container) (typed FeaturePython)
  n = 1
  ref = O_element
FEATURE [App::DocumentObjectGroupPython] G4_POLYVINYL_PYRROLIDONE  # scripted group (container) (typed FeaturePython)
  Dunit = g/cm3
  Dvalue = 1.25
  Group = -> [C_element095,H_element087,N_element037,O_element084]
  conduct = 2
  density = 1
  expand = 3
  formula = G4_POLYVINYL_PYRROLIDONE
  name = G4_POLYVINYL_PYRROLIDONE
  specific = 4
FEATURE [App::DocumentObjectGroupPython] K_element008  label="K_element : 1"  # scripted group (container) (typed FeaturePython)
  n = 1
  ref = K_element
FEATURE [App::DocumentObjectGroupPython] I_element006  label="I_element : 003"  # scripted group (container) (typed FeaturePython)
  n = 1
  ref = I_element
FEATURE [App::DocumentObjectGroupPython] G4_POTASSIUM_IODIDE  # scripted group (container) (typed FeaturePython)
  Dunit = g/cm3
  Dvalue = 3.13
  Group = -> [K_element008,I_element006]
  conduct = 2
  density = 1
  expand = 3
  formula = G4_POTASSIUM_IODIDE
  name = G4_POTASSIUM_IODIDE
  specific = 4
FEATURE [App::DocumentObjectGroupPython] K_element009  label="K_element : 2"  # scripted group (container) (typed FeaturePython)
  n = 2
  ref = K_element
FEATURE [App::DocumentObjectGroupPython] O_element085  label="O_element : 046"  # scripted group (container) (typed FeaturePython)
  n = 1
  ref = O_element
FEATURE [App::DocumentObjectGroupPython] G4_POTASSIUM_OXIDE  # scripted group (container) (typed FeaturePython)
  Dunit = g/cm3
  Dvalue = 2.32
  Group = -> [K_element009,O_element085]
  conduct = 2
  density = 1
  expand = 3
  formula = G4_POTASSIUM_OXIDE
  name = G4_POTASSIUM_OXIDE
  specific = 4
FEATURE [App::DocumentObjectGroupPython] C_element096  label="C_element : 054"  # scripted group (container) (typed FeaturePython)
  n = 3
  ref = C_element
FEATURE [App::DocumentObjectGroupPython] H_element088  label="H_element : 049"  # scripted group (container) (typed FeaturePython)
  n = 8
  ref = H_element
FEATURE [App::DocumentObjectGroupPython] G4_PROPANE  # scripted group (container) (typed FeaturePython)
  Dunit = g/cm3
  Dvalue = 0.00187939
  Group = -> [C_element096,H_element088]
  conduct = 2
  density = 1
  expand = 3
  formula = G4_PROPANE
  name = G4_PROPANE
  specific = 4
FEATURE [App::DocumentObjectGroupPython] C_element097  label="C_element : 055"  # scripted group (container) (typed FeaturePython)
  n = 3
  ref = C_element
FEATURE [App::DocumentObjectGroupPython] H_element089  label="H_element : 050"  # scripted group (container) (typed FeaturePython)
  n = 8
  ref = H_element
FEATURE [App::DocumentObjectGroupPython] G4_lPROPANE  # scripted group (container) (typed FeaturePython)
  Dunit = g/cm3
  Dvalue = 0.43
  Group = -> [C_element097,H_element089]
  conduct = 2
  density = 1
  expand = 3
  formula = G4_lPROPANE
  name = G4_lPROPANE
  specific = 4
FEATURE [App::DocumentObjectGroupPython] C_element098  label="C_element : 056"  # scripted group (container) (typed FeaturePython)
  n = 3
  ref = C_element
FEATURE [App::DocumentObjectGroupPython] H_element090  label="H_element : 051"  # scripted group (container) (typed FeaturePython)
  n = 8
  ref = H_element
FEATURE [App::DocumentObjectGroupPython] O_element086  label="O_element : 047"  # scripted group (container) (typed FeaturePython)
  n = 1
  ref = O_element
FEATURE [App::DocumentObjectGroupPython] G4_N_PROPYL_ALCOHOL  label="G4_N-PROPYL_ALCOHOL"  # scripted group (container) (typed FeaturePython)
  Dunit = g/cm3
  Dvalue = 0.8035
  Group = -> [C_element098,H_element090,O_element086]
  conduct = 2
  density = 1
  expand = 3
  formula = G4_N-PROPYL_ALCOHOL
  name = G4_N-PROPYL_ALCOHOL
  specific = 4
FEATURE [App::DocumentObjectGroupPython] C_element099  label="C_element : 057"  # scripted group (container) (typed FeaturePython)
  n = 5
  ref = C_element
FEATURE [App::DocumentObjectGroupPython] H_element091  label="H_element : 052"  # scripted group (container) (typed FeaturePython)
  n = 5
  ref = H_element
FEATURE [App::DocumentObjectGroupPython] N_element038  label="N_element : 017"  # scripted group (container) (typed FeaturePython)
  n = 1
  ref = N_element
FEATURE [App::DocumentObjectGroupPython] G4_PYRIDINE  # scripted group (container) (typed FeaturePython)
  Dunit = g/cm3
  Dvalue = 0.9819
  Group = -> [C_element099,H_element091,N_element038]
  conduct = 2
  density = 1
  expand = 3
  formula = G4_PYRIDINE
  name = G4_PYRIDINE
  specific = 4
FEATURE [App::DocumentObjectGroupPython] H_element092  label="H_element : 0.144"  # scripted group (container) (typed FeaturePython)
  n = 0.143711
FEATURE [App::DocumentObjectGroupPython] C_element100  label="C_element : 0.856"  # scripted group (container) (typed FeaturePython)
  n = 0.856289
FEATURE [App::DocumentObjectGroupPython] G4_RUBBER_BUTYL  # scripted group (container) (typed FeaturePython)
  Dunit = g/cm3
  Dvalue = 0.92
  Group = -> [H_element092,C_element100]
  conduct = 2
  density = 1
  expand = 3
  formula = G4_RUBBER_BUTYL
  name = G4_RUBBER_BUTYL
  specific = 4
FEATURE [App::DocumentObjectGroupPython] H_element093  label="H_element : 0.118"  # scripted group (container) (typed FeaturePython)
  n = 0.118371
FEATURE [App::DocumentObjectGroupPython] C_element101  label="C_element : 0.882"  # scripted group (container) (typed FeaturePython)
  n = 0.881629
FEATURE [App::DocumentObjectGroupPython] G4_RUBBER_NATURAL  # scripted group (container) (typed FeaturePython)
  Dunit = g/cm3
  Dvalue = 0.92
  Group = -> [H_element093,C_element101]
  conduct = 2
  density = 1
  expand = 3
  formula = G4_RUBBER_NATURAL
  name = G4_RUBBER_NATURAL
  specific = 4
FEATURE [App::DocumentObjectGroupPython] H_element094  label="H_element : 0.145"  # scripted group (container) (typed FeaturePython)
  n = 0.05692
FEATURE [App::DocumentObjectGroupPython] C_element102  label="C_element : 0.543"  # scripted group (container) (typed FeaturePython)
  n = 0.542646
FEATURE [App::DocumentObjectGroupPython] Cl_element021  label="Cl_element : 0.400"  # scripted group (container) (typed FeaturePython)
  n = 0.400434
FEATURE [App::DocumentObjectGroupPython] G4_RUBBER_NEOPRENE  # scripted group (container) (typed FeaturePython)
  Dunit = g/cm3
  Dvalue = 1.23
  Group = -> [H_element094,C_element102,Cl_element021]
  conduct = 2
  density = 1
  expand = 3
  formula = G4_RUBBER_NEOPRENE
  name = G4_RUBBER_NEOPRENE
  specific = 4
FEATURE [App::DocumentObjectGroupPython] Si_element006  label="Si_element : 1"  # scripted group (container) (typed FeaturePython)
  n = 1
  ref = Si_element
FEATURE [App::DocumentObjectGroupPython] O_element087  label="O_element : 048"  # scripted group (container) (typed FeaturePython)
  n = 2
  ref = O_element
FEATURE [App::DocumentObjectGroupPython] G4_SILICON_DIOXIDE  # scripted group (container) (typed FeaturePython)
  Dunit = g/cm3
  Dvalue = 2.32
  Group = -> [Si_element006,O_element087]
  conduct = 2
  density = 1
  expand = 3
  formula = G4_SILICON_DIOXIDE
  name = G4_SILICON_DIOXIDE
  specific = 4
FEATURE [App::DocumentObjectGroupPython] Ag_element002  label="Ag_element : 1"  # scripted group (container) (typed FeaturePython)
  n = 1
  ref = Ag_element
FEATURE [App::DocumentObjectGroupPython] Br_element005  label="Br_element : 003"  # scripted group (container) (typed FeaturePython)
  n = 1
  ref = Br_element
FEATURE [App::DocumentObjectGroupPython] G4_SILVER_BROMIDE  # scripted group (container) (typed FeaturePython)
  Dunit = g/cm3
  Dvalue = 6.473
  Group = -> [Ag_element002,Br_element005]
  conduct = 2
  density = 1
  expand = 3
  formula = G4_SILVER_BROMIDE
  name = G4_SILVER_BROMIDE
  specific = 4
FEATURE [App::DocumentObjectGroupPython] Ag_element003  label="Ag_element : 002"  # scripted group (container) (typed FeaturePython)
  n = 1
  ref = Ag_element
FEATURE [App::DocumentObjectGroupPython] Cl_element022  label="Cl_element : 011"  # scripted group (container) (typed FeaturePython)
  n = 1
  ref = Cl_element
FEATURE [App::DocumentObjectGroupPython] G4_SILVER_CHLORIDE  # scripted group (container) (typed FeaturePython)
  Dunit = g/cm3
  Dvalue = 5.56
  Group = -> [Ag_element003,Cl_element022]
  conduct = 2
  density = 1
  expand = 3
  formula = G4_SILVER_CHLORIDE
  name = G4_SILVER_CHLORIDE
  specific = 4
FEATURE [App::DocumentObjectGroupPython] Br_element006  label="Br_element : 0.423"  # scripted group (container) (typed FeaturePython)
  n = 0.422895
FEATURE [App::DocumentObjectGroupPython] Ag_element004  label="Ag_element : 0.574"  # scripted group (container) (typed FeaturePython)
  n = 0.573748
FEATURE [App::DocumentObjectGroupPython] I_element007  label="I_element : 0.649"  # scripted group (container) (typed FeaturePython)
  n = 0.003357
FEATURE [App::DocumentObjectGroupPython] G4_SILVER_HALIDES  # scripted group (container) (typed FeaturePython)
  Dunit = g/cm3
  Dvalue = 6.47
  Group = -> [Br_element006,Ag_element004,I_element007]
  conduct = 2
  density = 1
  expand = 3
  formula = G4_SILVER_HALIDES
  name = G4_SILVER_HALIDES
  specific = 4
FEATURE [App::DocumentObjectGroupPython] Ag_element005  label="Ag_element : 003"  # scripted group (container) (typed FeaturePython)
  n = 1
  ref = Ag_element
FEATURE [App::DocumentObjectGroupPython] I_element008  label="I_element : 004"  # scripted group (container) (typed FeaturePython)
  n = 1
  ref = I_element
FEATURE [App::DocumentObjectGroupPython] G4_SILVER_IODIDE  # scripted group (container) (typed FeaturePython)
  Dunit = g/cm3
  Dvalue = 6.01
  Group = -> [Ag_element005,I_element008]
  conduct = 2
  density = 1
  expand = 3
  formula = G4_SILVER_IODIDE
  name = G4_SILVER_IODIDE
  specific = 4
FEATURE [App::DocumentObjectGroupPython] H_element095  label="H_element : 0.100"  # scripted group (container) (typed FeaturePython)
  n = 0.1
FEATURE [App::DocumentObjectGroupPython] C_element103  label="C_element : 0.204"  # scripted group (container) (typed FeaturePython)
  n = 0.204
FEATURE [App::DocumentObjectGroupPython] N_element039  label="N_element : 0.759"  # scripted group (container) (typed FeaturePython)
  n = 0.042
FEATURE [App::DocumentObjectGroupPython] O_element088  label="O_element : 0.645"  # scripted group (container) (typed FeaturePython)
  n = 0.645
FEATURE [App::DocumentObjectGroupPython] Na_element013  label="Na_element : 0.100"  # scripted group (container) (typed FeaturePython)
  n = 0.002
FEATURE [App::DocumentObjectGroupPython] P_element009  label="P_element : 0.107"  # scripted group (container) (typed FeaturePython)
  n = 0.001
FEATURE [App::DocumentObjectGroupPython] S_element020  label="S_element : 0.021"  # scripted group (container) (typed FeaturePython)
  n = 0.002
FEATURE [App::DocumentObjectGroupPython] Cl_element023  label="Cl_element : 0.590"  # scripted group (container) (typed FeaturePython)
  n = 0.003
FEATURE [App::DocumentObjectGroupPython] K_element010  label="K_element : 0.001"  # scripted group (container) (typed FeaturePython)
  n = 0.001
FEATURE [App::DocumentObjectGroupPython] G4_SKIN_ICRP  # scripted group (container) (typed FeaturePython)
  Dunit = g/cm3
  Dvalue = 1.09
  Group = -> [H_element095,C_element103,N_element039,O_element088,Na_element013,P_element009,S_element020,Cl_element023,K_element010]
  conduct = 2
  density = 1
  expand = 3
  formula = G4_SKIN_ICRP
  name = G4_SKIN_ICRP
  specific = 4
FEATURE [App::DocumentObjectGroupPython] Na_element014  label="Na_element : 2"  # scripted group (container) (typed FeaturePython)
  n = 2
  ref = Na_element
FEATURE [App::DocumentObjectGroupPython] C_element104  label="C_element : 058"  # scripted group (container) (typed FeaturePython)
  n = 1
  ref = C_element
FEATURE [App::DocumentObjectGroupPython] O_element089  label="O_element : 049"  # scripted group (container) (typed FeaturePython)
  n = 3
  ref = O_element
FEATURE [App::DocumentObjectGroupPython] G4_SODIUM_CARBONATE  # scripted group (container) (typed FeaturePython)
  Dunit = g/cm3
  Dvalue = 2.532
  Group = -> [Na_element014,C_element104,O_element089]
  conduct = 2
  density = 1
  expand = 3
  formula = G4_SODIUM_CARBONATE
  name = G4_SODIUM_CARBONATE
  specific = 4
FEATURE [App::DocumentObjectGroupPython] Na_element015  label="Na_element : 1"  # scripted group (container) (typed FeaturePython)
  n = 1
  ref = Na_element
FEATURE [App::DocumentObjectGroupPython] I_element009  label="I_element : 005"  # scripted group (container) (typed FeaturePython)
  n = 1
  ref = I_element
FEATURE [App::DocumentObjectGroupPython] G4_SODIUM_IODIDE  # scripted group (container) (typed FeaturePython)
  Dunit = g/cm3
  Dvalue = 3.667
  Group = -> [Na_element015,I_element009]
  conduct = 2
  density = 1
  expand = 3
  formula = G4_SODIUM_IODIDE
  name = G4_SODIUM_IODIDE
  specific = 4
FEATURE [App::DocumentObjectGroupPython] Na_element016  label="Na_element : 003"  # scripted group (container) (typed FeaturePython)
  n = 2
  ref = Na_element
FEATURE [App::DocumentObjectGroupPython] O_element090  label="O_element : 050"  # scripted group (container) (typed FeaturePython)
  n = 1
  ref = O_element
FEATURE [App::DocumentObjectGroupPython] G4_SODIUM_MONOXIDE  # scripted group (container) (typed FeaturePython)
  Dunit = g/cm3
  Dvalue = 2.27
  Group = -> [Na_element016,O_element090]
  conduct = 2
  density = 1
  expand = 3
  formula = G4_SODIUM_MONOXIDE
  name = G4_SODIUM_MONOXIDE
  specific = 4
FEATURE [App::DocumentObjectGroupPython] Na_element017  label="Na_element : 004"  # scripted group (container) (typed FeaturePython)
  n = 1
  ref = Na_element
FEATURE [App::DocumentObjectGroupPython] N_element040  label="N_element : 018"  # scripted group (container) (typed FeaturePython)
  n = 1
  ref = N_element
FEATURE [App::DocumentObjectGroupPython] O_element091  label="O_element : 051"  # scripted group (container) (typed FeaturePython)
  n = 3
  ref = O_element
FEATURE [App::DocumentObjectGroupPython] G4_SODIUM_NITRATE  # scripted group (container) (typed FeaturePython)
  Dunit = g/cm3
  Dvalue = 2.261
  Group = -> [Na_element017,N_element040,O_element091]
  conduct = 2
  density = 1
  expand = 3
  formula = G4_SODIUM_NITRATE
  name = G4_SODIUM_NITRATE
  specific = 4
FEATURE [App::DocumentObjectGroupPython] C_element105  label="C_element : 059"  # scripted group (container) (typed FeaturePython)
  n = 14
  ref = C_element
FEATURE [App::DocumentObjectGroupPython] H_element096  label="H_element : 053"  # scripted group (container) (typed FeaturePython)
  n = 12
  ref = H_element
FEATURE [App::DocumentObjectGroupPython] G4_STILBENE  # scripted group (container) (typed FeaturePython)
  Dunit = g/cm3
  Dvalue = 0.9707
  Group = -> [C_element105,H_element096]
  conduct = 2
  density = 1
  expand = 3
  formula = G4_STILBENE
  name = G4_STILBENE
  specific = 4
FEATURE [App::DocumentObjectGroupPython] C_element106  label="C_element : 12"  # scripted group (container) (typed FeaturePython)
  n = 12
  ref = C_element
FEATURE [App::DocumentObjectGroupPython] H_element097  label="H_element : 22"  # scripted group (container) (typed FeaturePython)
  n = 22
  ref = H_element
FEATURE [App::DocumentObjectGroupPython] O_element092  label="O_element : 11"  # scripted group (container) (typed FeaturePython)
  n = 11
  ref = O_element
FEATURE [App::DocumentObjectGroupPython] G4_SUCROSE  # scripted group (container) (typed FeaturePython)
  Dunit = g/cm3
  Dvalue = 1.5805
  Group = -> [C_element106,H_element097,O_element092]
  conduct = 2
  density = 1
  expand = 3
  formula = G4_SUCROSE
  name = G4_SUCROSE
  specific = 4
FEATURE [App::DocumentObjectGroupPython] C_element107  label="C_element : 18"  # scripted group (container) (typed FeaturePython)
  n = 18
  ref = C_element
FEATURE [App::DocumentObjectGroupPython] H_element098  label="H_element : 054"  # scripted group (container) (typed FeaturePython)
  n = 14
  ref = H_element
FEATURE [App::DocumentObjectGroupPython] G4_TERPHENYL  # scripted group (container) (typed FeaturePython)
  Dunit = g/cm3
  Dvalue = 1.24
  Group = -> [C_element107,H_element098]
  conduct = 2
  density = 1
  expand = 3
  formula = G4_TERPHENYL
  name = G4_TERPHENYL
  specific = 4
FEATURE [App::DocumentObjectGroupPython] H_element099  label="H_element : 0.146"  # scripted group (container) (typed FeaturePython)
  n = 0.106
FEATURE [App::DocumentObjectGroupPython] C_element108  label="C_element : 0.883"  # scripted group (container) (typed FeaturePython)
  n = 0.099
FEATURE [App::DocumentObjectGroupPython] N_element041  label="N_element : 0.020"  # scripted group (container) (typed FeaturePython)
  n = 0.02
FEATURE [App::DocumentObjectGroupPython] O_element093  label="O_element : 0.766"  # scripted group (container) (typed FeaturePython)
  n = 0.766
FEATURE [App::DocumentObjectGroupPython] Na_element018  label="Na_element : 0.101"  # scripted group (container) (typed FeaturePython)
  n = 0.002
FEATURE [App::DocumentObjectGroupPython] P_element010  label="P_element : 0.108"  # scripted group (container) (typed FeaturePython)
  n = 0.001
FEATURE [App::DocumentObjectGroupPython] S_element021  label="S_element : 0.022"  # scripted group (container) (typed FeaturePython)
  n = 0.002
FEATURE [App::DocumentObjectGroupPython] Cl_element024  label="Cl_element : 0.002"  # scripted group (container) (typed FeaturePython)
  n = 0.002
FEATURE [App::DocumentObjectGroupPython] K_element011  label="K_element : 0.017"  # scripted group (container) (typed FeaturePython)
  n = 0.002
FEATURE [App::DocumentObjectGroupPython] G4_TESTIS_ICRP  # scripted group (container) (typed FeaturePython)
  Dunit = g/cm3
  Dvalue = 1.04
  Group = -> [H_element099,C_element108,N_element041,O_element093,Na_element018,P_element010,S_element021,Cl_element024,K_element011]
  conduct = 2
  density = 1
  expand = 3
  formula = G4_TESTIS_ICRP
  name = G4_TESTIS_ICRP
  specific = 4
FEATURE [App::DocumentObjectGroupPython] C_element109  label="C_element : 060"  # scripted group (container) (typed FeaturePython)
  n = 2
  ref = C_element
FEATURE [App::DocumentObjectGroupPython] Cl_element025  label="Cl_element : 012"  # scripted group (container) (typed FeaturePython)
  n = 4
  ref = Cl_element
FEATURE [App::DocumentObjectGroupPython] G4_TETRACHLOROETHYLENE  # scripted group (container) (typed FeaturePython)
  Dunit = g/cm3
  Dvalue = 1.625
  Group = -> [C_element109,Cl_element025]
  conduct = 2
  density = 1
  expand = 3
  formula = G4_TETRACHLOROETHYLENE
  name = G4_TETRACHLOROETHYLENE
  specific = 4
FEATURE [App::DocumentObjectGroupPython] Tl_element001  label="Tl_element : 1"  # scripted group (container) (typed FeaturePython)
  n = 1
  ref = Tl_element
FEATURE [App::DocumentObjectGroupPython] Cl_element026  label="Cl_element : 013"  # scripted group (container) (typed FeaturePython)
  n = 1
  ref = Cl_element
FEATURE [App::DocumentObjectGroupPython] G4_THALLIUM_CHLORIDE  # scripted group (container) (typed FeaturePython)
  Dunit = g/cm3
  Dvalue = 7.004
  Group = -> [Tl_element001,Cl_element026]
  conduct = 2
  density = 1
  expand = 3
  formula = G4_THALLIUM_CHLORIDE
  name = G4_THALLIUM_CHLORIDE
  specific = 4
FEATURE [App::DocumentObjectGroupPython] H_element100  label="H_element : 0.147"  # scripted group (container) (typed FeaturePython)
  n = 0.105
FEATURE [App::DocumentObjectGroupPython] C_element110  label="C_element : 0.256"  # scripted group (container) (typed FeaturePython)
  n = 0.256
FEATURE [App::DocumentObjectGroupPython] N_element042  label="N_element : 0.760"  # scripted group (container) (typed FeaturePython)
  n = 0.027
FEATURE [App::DocumentObjectGroupPython] O_element094  label="O_element : 0.602"  # scripted group (container) (typed FeaturePython)
  n = 0.602
FEATURE [App::DocumentObjectGroupPython] Na_element019  label="Na_element : 0.102"  # scripted group (container) (typed FeaturePython)
  n = 0.001
FEATURE [App::DocumentObjectGroupPython] P_element011  label="P_element : 0.109"  # scripted group (container) (typed FeaturePython)
  n = 0.002
FEATURE [App::DocumentObjectGroupPython] S_element022  label="S_element : 0.023"  # scripted group (container) (typed FeaturePython)
  n = 0.003
FEATURE [App::DocumentObjectGroupPython] Cl_element027  label="Cl_element : 0.591"  # scripted group (container) (typed FeaturePython)
  n = 0.002
FEATURE [App::DocumentObjectGroupPython] K_element012  label="K_element : 0.018"  # scripted group (container) (typed FeaturePython)
  n = 0.002
FEATURE [App::DocumentObjectGroupPython] G4_TISSUE_SOFT_ICRP  # scripted group (container) (typed FeaturePython)
  Dunit = g/cm3
  Dvalue = 1.03
  Group = -> [H_element100,C_element110,N_element042,O_element094,Na_element019,P_element011,S_element022,Cl_element027,K_element012]
  conduct = 2
  density = 1
  expand = 3
  formula = G4_TISSUE_SOFT_ICRP
  name = G4_TISSUE_SOFT_ICRP
  specific = 4
FEATURE [App::DocumentObjectGroupPython] H_element101  label="H_element : 0.148"  # scripted group (container) (typed FeaturePython)
  n = 0.101
FEATURE [App::DocumentObjectGroupPython] C_element111  label="C_element : 0.111"  # scripted group (container) (typed FeaturePython)
  n = 0.111
FEATURE [App::DocumentObjectGroupPython] N_element043  label="N_element : 0.026"  # scripted group (container) (typed FeaturePython)
  n = 0.026
FEATURE [App::DocumentObjectGroupPython] O_element095  label="O_element : 0.762"  # scripted group (container) (typed FeaturePython)
  n = 0.762
FEATURE [App::DocumentObjectGroupPython] G4_TISSUE_SOFT_ICRU_4  label="G4_TISSUE_SOFT_ICRU-4"  # scripted group (container) (typed FeaturePython)
  Dunit = g/cm3
  Dvalue = 1
  Group = -> [H_element101,C_element111,N_element043,O_element095]
  conduct = 2
  density = 1
  expand = 3
  formula = G4_TISSUE_SOFT_ICRU-4
  name = G4_TISSUE_SOFT_ICRU-4
  specific = 4
FEATURE [App::DocumentObjectGroupPython] H_element102  label="H_element : 0.149"  # scripted group (container) (typed FeaturePython)
  n = 0.101869
FEATURE [App::DocumentObjectGroupPython] C_element112  label="C_element : 0.456"  # scripted group (container) (typed FeaturePython)
  n = 0.456179
FEATURE [App::DocumentObjectGroupPython] N_element044  label="N_element : 0.761"  # scripted group (container) (typed FeaturePython)
  n = 0.035172
FEATURE [App::DocumentObjectGroupPython] O_element096  label="O_element : 0.407"  # scripted group (container) (typed FeaturePython)
  n = 0.40678
FEATURE [App::DocumentObjectGroupPython] G4_TISSUE_METHANE  label="G4_TISSUE-METHANE"  # scripted group (container) (typed FeaturePython)
  Dunit = g/cm3
  Dvalue = 0.00106409
  Group = -> [H_element102,C_element112,N_element044,O_element096]
  conduct = 2
  density = 1
  expand = 3
  formula = G4_TISSUE-METHANE
  name = G4_TISSUE-METHANE
  specific = 4
FEATURE [App::DocumentObjectGroupPython] H_element103  label="H_element : 0.103"  # scripted group (container) (typed FeaturePython)
  n = 0.102672
FEATURE [App::DocumentObjectGroupPython] C_element113  label="C_element : 0.569"  # scripted group (container) (typed FeaturePython)
  n = 0.56894
FEATURE [App::DocumentObjectGroupPython] N_element045  label="N_element : 0.762"  # scripted group (container) (typed FeaturePython)
  n = 0.035022
FEATURE [App::DocumentObjectGroupPython] O_element097  label="O_element : 0.293"  # scripted group (container) (typed FeaturePython)
  n = 0.293366
FEATURE [App::DocumentObjectGroupPython] G4_TISSUE_PROPANE  label="G4_TISSUE-PROPANE"  # scripted group (container) (typed FeaturePython)
  Dunit = g/cm3
  Dvalue = 0.00182628
  Group = -> [H_element103,C_element113,N_element045,O_element097]
  conduct = 2
  density = 1
  expand = 3
  formula = G4_TISSUE-PROPANE
  name = G4_TISSUE-PROPANE
  specific = 4
FEATURE [App::DocumentObjectGroupPython] Ti_element003  label="Ti_element : 1"  # scripted group (container) (typed FeaturePython)
  n = 1
  ref = Ti_element
FEATURE [App::DocumentObjectGroupPython] O_element098  label="O_element : 052"  # scripted group (container) (typed FeaturePython)
  n = 2
  ref = O_element
FEATURE [App::DocumentObjectGroupPython] G4_TITANIUM_DIOXIDE  # scripted group (container) (typed FeaturePython)
  Dunit = g/cm3
  Dvalue = 4.26
  Group = -> [Ti_element003,O_element098]
  conduct = 2
  density = 1
  expand = 3
  formula = G4_TITANIUM_DIOXIDE
  name = G4_TITANIUM_DIOXIDE
  specific = 4
FEATURE [App::DocumentObjectGroupPython] C_element114  label="C_element : 061"  # scripted group (container) (typed FeaturePython)
  n = 7
  ref = C_element
FEATURE [App::DocumentObjectGroupPython] H_element104  label="H_element : 055"  # scripted group (container) (typed FeaturePython)
  n = 8
  ref = H_element
FEATURE [App::DocumentObjectGroupPython] G4_TOLUENE  # scripted group (container) (typed FeaturePython)
  Dunit = g/cm3
  Dvalue = 0.8669
  Group = -> [C_element114,H_element104]
  conduct = 2
  density = 1
  expand = 3
  formula = G4_TOLUENE
  name = G4_TOLUENE
  specific = 4
FEATURE [App::DocumentObjectGroupPython] C_element115  label="C_element : 062"  # scripted group (container) (typed FeaturePython)
  n = 2
  ref = C_element
FEATURE [App::DocumentObjectGroupPython] H_element105  label="H_element : 056"  # scripted group (container) (typed FeaturePython)
  n = 1
  ref = H_element
FEATURE [App::DocumentObjectGroupPython] Cl_element028  label="Cl_element : 014"  # scripted group (container) (typed FeaturePython)
  n = 3
  ref = Cl_element
FEATURE [App::DocumentObjectGroupPython] G4_TRICHLOROETHYLENE  # scripted group (container) (typed FeaturePython)
  Dunit = g/cm3
  Dvalue = 1.46
  Group = -> [C_element115,H_element105,Cl_element028]
  conduct = 2
  density = 1
  expand = 3
  formula = G4_TRICHLOROETHYLENE
  name = G4_TRICHLOROETHYLENE
  specific = 4
FEATURE [App::DocumentObjectGroupPython] C_element116  label="C_element : 063"  # scripted group (container) (typed FeaturePython)
  n = 6
  ref = C_element
FEATURE [App::DocumentObjectGroupPython] H_element106  label="H_element : 15"  # scripted group (container) (typed FeaturePython)
  n = 15
  ref = H_element
FEATURE [App::DocumentObjectGroupPython] O_element099  label="O_element : 053"  # scripted group (container) (typed FeaturePython)
  n = 4
  ref = O_element
FEATURE [App::DocumentObjectGroupPython] P_element012  label="P_element : 1"  # scripted group (container) (typed FeaturePython)
  n = 1
  ref = P_element
FEATURE [App::DocumentObjectGroupPython] G4_TRIETHYL_PHOSPHATE  # scripted group (container) (typed FeaturePython)
  Dunit = g/cm3
  Dvalue = 1.07
  Group = -> [C_element116,H_element106,O_element099,P_element012]
  conduct = 2
  density = 1
  expand = 3
  formula = G4_TRIETHYL_PHOSPHATE
  name = G4_TRIETHYL_PHOSPHATE
  specific = 4
FEATURE [App::DocumentObjectGroupPython] W_element003  label="W_element : 003"  # scripted group (container) (typed FeaturePython)
  n = 1
  ref = W_element
FEATURE [App::DocumentObjectGroupPython] F_element017  label="F_element : 6"  # scripted group (container) (typed FeaturePython)
  n = 6
  ref = F_element
FEATURE [App::DocumentObjectGroupPython] G4_TUNGSTEN_HEXAFLUORIDE  # scripted group (container) (typed FeaturePython)
  Dunit = g/cm3
  Dvalue = 2.4
  Group = -> [W_element003,F_element017]
  conduct = 2
  density = 1
  expand = 3
  formula = G4_TUNGSTEN_HEXAFLUORIDE
  name = G4_TUNGSTEN_HEXAFLUORIDE
  specific = 4
FEATURE [App::DocumentObjectGroupPython] U_element001  label="U_element : 1"  # scripted group (container) (typed FeaturePython)
  n = 1
  ref = U_element
FEATURE [App::DocumentObjectGroupPython] C_element117  label="C_element : 064"  # scripted group (container) (typed FeaturePython)
  n = 2
  ref = C_element
FEATURE [App::DocumentObjectGroupPython] G4_URANIUM_DICARBIDE  # scripted group (container) (typed FeaturePython)
  Dunit = g/cm3
  Dvalue = 11.28
  Group = -> [U_element001,C_element117]
  conduct = 2
  density = 1
  expand = 3
  formula = G4_URANIUM_DICARBIDE
  name = G4_URANIUM_DICARBIDE
  specific = 4
FEATURE [App::DocumentObjectGroupPython] U_element002  label="U_element : 002"  # scripted group (container) (typed FeaturePython)
  n = 1
  ref = U_element
FEATURE [App::DocumentObjectGroupPython] C_element118  label="C_element : 065"  # scripted group (container) (typed FeaturePython)
  n = 1
  ref = C_element
FEATURE [App::DocumentObjectGroupPython] G4_URANIUM_MONOCARBIDE  # scripted group (container) (typed FeaturePython)
  Dunit = g/cm3
  Dvalue = 13.63
  Group = -> [U_element002,C_element118]
  conduct = 2
  density = 1
  expand = 3
  formula = G4_URANIUM_MONOCARBIDE
  name = G4_URANIUM_MONOCARBIDE
  specific = 4
FEATURE [App::DocumentObjectGroupPython] U_element003  label="U_element : 003"  # scripted group (container) (typed FeaturePython)
  n = 1
  ref = U_element
FEATURE [App::DocumentObjectGroupPython] O_element100  label="O_element : 054"  # scripted group (container) (typed FeaturePython)
  n = 2
  ref = O_element
FEATURE [App::DocumentObjectGroupPython] G4_URANIUM_OXIDE  # scripted group (container) (typed FeaturePython)
  Dunit = g/cm3
  Dvalue = 10.96
  Group = -> [U_element003,O_element100]
  conduct = 2
  density = 1
  expand = 3
  formula = G4_URANIUM_OXIDE
  name = G4_URANIUM_OXIDE
  specific = 4
FEATURE [App::DocumentObjectGroupPython] C_element119  label="C_element : 066"  # scripted group (container) (typed FeaturePython)
  n = 1
  ref = C_element
FEATURE [App::DocumentObjectGroupPython] H_element107  label="H_element : 057"  # scripted group (container) (typed FeaturePython)
  n = 4
  ref = H_element
FEATURE [App::DocumentObjectGroupPython] N_element046  label="N_element : 019"  # scripted group (container) (typed FeaturePython)
  n = 2
  ref = N_element
FEATURE [App::DocumentObjectGroupPython] O_element101  label="O_element : 055"  # scripted group (container) (typed FeaturePython)
  n = 1
  ref = O_element
FEATURE [App::DocumentObjectGroupPython] G4_UREA  # scripted group (container) (typed FeaturePython)
  Dunit = g/cm3
  Dvalue = 1.323
  Group = -> [C_element119,H_element107,N_element046,O_element101]
  conduct = 2
  density = 1
  expand = 3
  formula = G4_UREA
  name = G4_UREA
  specific = 4
FEATURE [App::DocumentObjectGroupPython] C_element120  label="C_element : 067"  # scripted group (container) (typed FeaturePython)
  n = 5
  ref = C_element
FEATURE [App::DocumentObjectGroupPython] H_element108  label="H_element : 058"  # scripted group (container) (typed FeaturePython)
  n = 11
  ref = H_element
FEATURE [App::DocumentObjectGroupPython] N_element047  label="N_element : 020"  # scripted group (container) (typed FeaturePython)
  n = 1
  ref = N_element
FEATURE [App::DocumentObjectGroupPython] O_element102  label="O_element : 056"  # scripted group (container) (typed FeaturePython)
  n = 2
  ref = O_element
FEATURE [App::DocumentObjectGroupPython] G4_VALINE  # scripted group (container) (typed FeaturePython)
  Dunit = g/cm3
  Dvalue = 1.23
  Group = -> [C_element120,H_element108,N_element047,O_element102]
  conduct = 2
  density = 1
  expand = 3
  formula = G4_VALINE
  name = G4_VALINE
  specific = 4
FEATURE [App::DocumentObjectGroupPython] H_element109  label="H_element : 0.009"  # scripted group (container) (typed FeaturePython)
  n = 0.009417
FEATURE [App::DocumentObjectGroupPython] C_element121  label="C_element : 0.281"  # scripted group (container) (typed FeaturePython)
  n = 0.280555
FEATURE [App::DocumentObjectGroupPython] F_element018  label="F_element : 0.710"  # scripted group (container) (typed FeaturePython)
  n = 0.710028
FEATURE [App::DocumentObjectGroupPython] G4_VITON  # scripted group (container) (typed FeaturePython)
  Dunit = g/cm3
  Dvalue = 1.8
  Group = -> [H_element109,C_element121,F_element018]
  conduct = 2
  density = 1
  expand = 3
  formula = G4_VITON
  name = G4_VITON
  specific = 4
FEATURE [App::DocumentObjectGroupPython] H_element110  label="H_element : 059"  # scripted group (container) (typed FeaturePython)
  n = 2
  ref = H_element
FEATURE [App::DocumentObjectGroupPython] O_element103  label="O_element : 057"  # scripted group (container) (typed FeaturePython)
  n = 1
  ref = O_element
FEATURE [App::DocumentObjectGroupPython] G4_WATER  # scripted group (container) (typed FeaturePython)
  Dunit = g/cm3
  Dvalue = 1
  Group = -> [H_element110,O_element103]
  conduct = 2
  density = 1
  expand = 3
  formula = G4_WATER
  name = G4_WATER
  specific = 4
FEATURE [App::DocumentObjectGroupPython] H_element111  label="H_element : 060"  # scripted group (container) (typed FeaturePython)
  n = 2
  ref = H_element
FEATURE [App::DocumentObjectGroupPython] O_element104  label="O_element : 058"  # scripted group (container) (typed FeaturePython)
  n = 1
  ref = O_element
FEATURE [App::DocumentObjectGroupPython] G4_WATER_VAPOR  # scripted group (container) (typed FeaturePython)
  Dunit = g/cm3
  Dvalue = 0.000756182
  Group = -> [H_element111,O_element104]
  conduct = 2
  density = 1
  expand = 3
  formula = G4_WATER_VAPOR
  name = G4_WATER_VAPOR
  specific = 4
FEATURE [App::DocumentObjectGroupPython] C_element122  label="C_element : 068"  # scripted group (container) (typed FeaturePython)
  n = 8
  ref = C_element
FEATURE [App::DocumentObjectGroupPython] H_element112  label="H_element : 061"  # scripted group (container) (typed FeaturePython)
  n = 10
  ref = H_element
FEATURE [App::DocumentObjectGroupPython] G4_XYLENE  # scripted group (container) (typed FeaturePython)
  Dunit = g/cm3
  Dvalue = 0.87
  Group = -> [C_element122,H_element112]
  conduct = 2
  density = 1
  expand = 3
  formula = G4_XYLENE
  name = G4_XYLENE
  specific = 4
FEATURE [App::DocumentObjectGroupPython] C_element123  label="C_element : 069"  # scripted group (container) (typed FeaturePython)
  n = 1
  ref = C_element
FEATURE [App::DocumentObjectGroupPython] G4_GRAPHITE  # scripted group (container) (typed FeaturePython)
  Dunit = g/cm3
  Dvalue = 2.21
  Group = -> [C_element123]
  conduct = 2
  density = 1
  expand = 3
  formula = G4_GRAPHITE
  name = G4_GRAPHITE
  specific = 4
FEATURE [App::DocumentObjectGroupPython] NIST  # scripted group (container) (typed FeaturePython)
  Group = -> [G4_A_150_TISSUE,G4_ACETONE,G4_ACETYLENE,G4_ADENINE,G4_ADIPOSE_TISSUE_ICRP,G4_AIR,G4_ALANINE,G4_ALUMINUM_OXIDE,G4_AMBER,G4_AMMONIA,G4_ANILINE,G4_ANTHRACENE,G4_B_100_BONE,G4_BAKELITE,G4_BARIUM_FLUORIDE,G4_BARIUM_SULFATE,G4_BENZENE,G4_BERYLLIUM_OXIDE,G4_BGO,G4_BLOOD_ICRP,G4_BONE_COMPACT_ICRU,G4_BONE_CORTICAL_ICRP,G4_BORON_CARBIDE,G4_BORON_OXIDE,G4_BRAIN_ICRP,G4_BUTANE,G4_N_BUTYL_ALCOHOL,G4_C_552,+152 more]
FEATURE [App::DocumentObjectGroupPython] H_element113  label="H_element : 062"  # scripted group (container) (typed FeaturePython)
  n = 1
  ref = H_element
FEATURE [App::DocumentObjectGroupPython] G4_H  # scripted group (container) (typed FeaturePython)
  Dunit = g/cm3
  Dvalue = 8.3748e-05
  Group = -> [H_element113]
  conduct = 2
  density = 1
  expand = 3
  formula = H
  name = G4_H
  specific = 4
FEATURE [App::DocumentObjectGroupPython] He_element001  label="He_element : 1"  # scripted group (container) (typed FeaturePython)
  n = 1
  ref = He_element
FEATURE [App::DocumentObjectGroupPython] G4_He  # scripted group (container) (typed FeaturePython)
  Dunit = g/cm3
  Dvalue = 0.000166322
  Group = -> [He_element001]
  conduct = 2
  density = 1
  expand = 3
  formula = He
  name = G4_He
  specific = 4
FEATURE [App::DocumentObjectGroupPython] Li_element008  label="Li_element : 008"  # scripted group (container) (typed FeaturePython)
  n = 1
  ref = Li_element
FEATURE [App::DocumentObjectGroupPython] G4_Li  # scripted group (container) (typed FeaturePython)
  Dunit = g/cm3
  Dvalue = 0.534
  Group = -> [Li_element008]
  conduct = 2
  density = 1
  expand = 3
  formula = Li
  name = G4_Li
  specific = 4
FEATURE [App::DocumentObjectGroupPython] Be_element002  label="Be_element : 002"  # scripted group (container) (typed FeaturePython)
  n = 1
  ref = Be_element
FEATURE [App::DocumentObjectGroupPython] G4_Be  # scripted group (container) (typed FeaturePython)
  Dunit = g/cm3
  Dvalue = 1.848
  Group = -> [Be_element002]
  conduct = 2
  density = 1
  expand = 3
  formula = Be
  name = G4_Be
  specific = 4
FEATURE [App::DocumentObjectGroupPython] B_element007  label="B_element : 007"  # scripted group (container) (typed FeaturePython)
  n = 1
  ref = B_element
FEATURE [App::DocumentObjectGroupPython] G4_B  # scripted group (container) (typed FeaturePython)
  Dunit = g/cm3
  Dvalue = 2.37
  Group = -> [B_element007]
  conduct = 2
  density = 1
  expand = 3
  formula = B
  name = G4_B
  specific = 4
FEATURE [App::DocumentObjectGroupPython] C_element124  label="C_element : 070"  # scripted group (container) (typed FeaturePython)
  n = 1
  ref = C_element
FEATURE [App::DocumentObjectGroupPython] G4_C  # scripted group (container) (typed FeaturePython)
  Dunit = g/cm3
  Dvalue = 2
  Group = -> [C_element124]
  conduct = 2
  density = 1
  expand = 3
  formula = C
  name = G4_C
  specific = 4
FEATURE [App::DocumentObjectGroupPython] N_element048  label="N_element : 021"  # scripted group (container) (typed FeaturePython)
  n = 1
  ref = N_element
FEATURE [App::DocumentObjectGroupPython] G4_N  # scripted group (container) (typed FeaturePython)
  Dunit = g/cm3
  Dvalue = 0.0011652
  Group = -> [N_element048]
  conduct = 2
  density = 1
  expand = 3
  formula = N
  name = G4_N
  specific = 4
FEATURE [App::DocumentObjectGroupPython] O_element105  label="O_element : 059"  # scripted group (container) (typed FeaturePython)
  n = 1
  ref = O_element
FEATURE [App::DocumentObjectGroupPython] G4_O  # scripted group (container) (typed FeaturePython)
  Dunit = g/cm3
  Dvalue = 0.00133151
  Group = -> [O_element105]
  conduct = 2
  density = 1
  expand = 3
  formula = O
  name = G4_O
  specific = 4
FEATURE [App::DocumentObjectGroupPython] F_element019  label="F_element : 008"  # scripted group (container) (typed FeaturePython)
  n = 1
  ref = F_element
FEATURE [App::DocumentObjectGroupPython] G4_F  # scripted group (container) (typed FeaturePython)
  Dunit = g/cm3
  Dvalue = 0.00158029
  Group = -> [F_element019]
  conduct = 2
  density = 1
  expand = 3
  formula = F
  name = G4_F
  specific = 4
FEATURE [App::DocumentObjectGroupPython] Ne_element001  label="Ne_element : 1"  # scripted group (container) (typed FeaturePython)
  n = 1
  ref = Ne_element
FEATURE [App::DocumentObjectGroupPython] G4_Ne  # scripted group (container) (typed FeaturePython)
  Dunit = g/cm3
  Dvalue = 0.000838505
  Group = -> [Ne_element001]
  conduct = 2
  density = 1
  expand = 3
  formula = Ne
  name = G4_Ne
  specific = 4
FEATURE [App::DocumentObjectGroupPython] Na_element020  label="Na_element : 005"  # scripted group (container) (typed FeaturePython)
  n = 1
  ref = Na_element
FEATURE [App::DocumentObjectGroupPython] G4_Na  # scripted group (container) (typed FeaturePython)
  Dunit = g/cm3
  Dvalue = 0.971
  Group = -> [Na_element020]
  conduct = 2
  density = 1
  expand = 3
  formula = Na
  name = G4_Na
  specific = 4
FEATURE [App::DocumentObjectGroupPython] Mg_element011  label="Mg_element : 005"  # scripted group (container) (typed FeaturePython)
  n = 1
  ref = Mg_element
FEATURE [App::DocumentObjectGroupPython] G4_Mg  # scripted group (container) (typed FeaturePython)
  Dunit = g/cm3
  Dvalue = 1.74
  Group = -> [Mg_element011]
  conduct = 2
  density = 1
  expand = 3
  formula = Mg
  name = G4_Mg
  specific = 4
FEATURE [App::DocumentObjectGroupPython] Al_element004  label="Al_element : 1"  # scripted group (container) (typed FeaturePython)
  n = 1
  ref = Al_element
FEATURE [App::DocumentObjectGroupPython] G4_Al  # scripted group (container) (typed FeaturePython)
  Dunit = g/cm3
  Dvalue = 2.699
  Group = -> [Al_element004]
  conduct = 2
  density = 1
  expand = 3
  formula = Al
  name = G4_Al
  specific = 4
FEATURE [App::DocumentObjectGroupPython] Si_element007  label="Si_element : 002"  # scripted group (container) (typed FeaturePython)
  n = 1
  ref = Si_element
FEATURE [App::DocumentObjectGroupPython] G4_Si  # scripted group (container) (typed FeaturePython)
  Dunit = g/cm3
  Dvalue = 2.33
  Group = -> [Si_element007]
  conduct = 2
  density = 1
  expand = 3
  formula = Si
  name = G4_Si
  specific = 4
FEATURE [App::DocumentObjectGroupPython] P_element013  label="P_element : 002"  # scripted group (container) (typed FeaturePython)
  n = 1
  ref = P_element
FEATURE [App::DocumentObjectGroupPython] G4_P  # scripted group (container) (typed FeaturePython)
  Dunit = g/cm3
  Dvalue = 2.2
  Group = -> [P_element013]
  conduct = 2
  density = 1
  expand = 3
  formula = P
  name = G4_P
  specific = 4
FEATURE [App::DocumentObjectGroupPython] S_element023  label="S_element : 007"  # scripted group (container) (typed FeaturePython)
  n = 1
  ref = S_element
FEATURE [App::DocumentObjectGroupPython] G4_S  # scripted group (container) (typed FeaturePython)
  Dunit = g/cm3
  Dvalue = 2
  Group = -> [S_element023]
  conduct = 2
  density = 1
  expand = 3
  formula = S
  name = G4_S
  specific = 4
FEATURE [App::DocumentObjectGroupPython] Cl_element029  label="Cl_element : 015"  # scripted group (container) (typed FeaturePython)
  n = 1
  ref = Cl_element
FEATURE [App::DocumentObjectGroupPython] G4_Cl  # scripted group (container) (typed FeaturePython)
  Dunit = g/cm3
  Dvalue = 0.00299473
  Group = -> [Cl_element029]
  conduct = 2
  density = 1
  expand = 3
  formula = Cl
  name = G4_Cl
  specific = 4
FEATURE [App::DocumentObjectGroupPython] Ar_element002  label="Ar_element : 1"  # scripted group (container) (typed FeaturePython)
  n = 1
  ref = Ar_element
FEATURE [App::DocumentObjectGroupPython] G4_Ar  # scripted group (container) (typed FeaturePython)
  Dunit = g/cm3
  Dvalue = 0.00166201
  Group = -> [Ar_element002]
  conduct = 2
  density = 1
  expand = 3
  formula = Ar
  name = G4_Ar
  specific = 4
FEATURE [App::DocumentObjectGroupPython] K_element013  label="K_element : 003"  # scripted group (container) (typed FeaturePython)
  n = 1
  ref = K_element
FEATURE [App::DocumentObjectGroupPython] G4_K  # scripted group (container) (typed FeaturePython)
  Dunit = g/cm3
  Dvalue = 0.862
  Group = -> [K_element013]
  conduct = 2
  density = 1
  expand = 3
  formula = K
  name = G4_K
  specific = 4
FEATURE [App::DocumentObjectGroupPython] Ca_element014  label="Ca_element : 007"  # scripted group (container) (typed FeaturePython)
  n = 1
  ref = Ca_element
FEATURE [App::DocumentObjectGroupPython] G4_Ca  # scripted group (container) (typed FeaturePython)
  Dunit = g/cm3
  Dvalue = 1.55
  Group = -> [Ca_element014]
  conduct = 2
  density = 1
  expand = 3
  formula = Ca
  name = G4_Ca
  specific = 4
FEATURE [App::DocumentObjectGroupPython] Sc_element001  label="Sc_element : 1"  # scripted group (container) (typed FeaturePython)
  n = 1
  ref = Sc_element
FEATURE [App::DocumentObjectGroupPython] G4_Sc  # scripted group (container) (typed FeaturePython)
  Dunit = g/cm3
  Dvalue = 2.989
  Group = -> [Sc_element001]
  conduct = 2
  density = 1
  expand = 3
  formula = Sc
  name = G4_Sc
  specific = 4
FEATURE [App::DocumentObjectGroupPython] Ti_element004  label="Ti_element : 002"  # scripted group (container) (typed FeaturePython)
  n = 1
  ref = Ti_element
FEATURE [App::DocumentObjectGroupPython] G4_Ti  # scripted group (container) (typed FeaturePython)
  Dunit = g/cm3
  Dvalue = 4.54
  Group = -> [Ti_element004]
  conduct = 2
  density = 1
  expand = 3
  formula = Ti
  name = G4_Ti
  specific = 4
FEATURE [App::DocumentObjectGroupPython] V_element001  label="V_element : 1"  # scripted group (container) (typed FeaturePython)
  n = 1
  ref = V_element
FEATURE [App::DocumentObjectGroupPython] G4_V  # scripted group (container) (typed FeaturePython)
  Dunit = g/cm3
  Dvalue = 6.11
  Group = -> [V_element001]
  conduct = 2
  density = 1
  expand = 3
  formula = V
  name = G4_V
  specific = 4
FEATURE [App::DocumentObjectGroupPython] Cr_element001  label="Cr_element : 1"  # scripted group (container) (typed FeaturePython)
  n = 1
  ref = Cr_element
FEATURE [App::DocumentObjectGroupPython] G4_Cr  # scripted group (container) (typed FeaturePython)
  Dunit = g/cm3
  Dvalue = 7.18
  Group = -> [Cr_element001]
  conduct = 2
  density = 1
  expand = 3
  formula = Cr
  name = G4_Cr
  specific = 4
FEATURE [App::DocumentObjectGroupPython] Mn_element001  label="Mn_element : 1"  # scripted group (container) (typed FeaturePython)
  n = 1
  ref = Mn_element
FEATURE [App::DocumentObjectGroupPython] G4_Mn  # scripted group (container) (typed FeaturePython)
  Dunit = g/cm3
  Dvalue = 7.44
  Group = -> [Mn_element001]
  conduct = 2
  density = 1
  expand = 3
  formula = Mn
  name = G4_Mn
  specific = 4
FEATURE [App::DocumentObjectGroupPython] Fe_element007  label="Fe_element : 004"  # scripted group (container) (typed FeaturePython)
  n = 1
  ref = Fe_element
FEATURE [App::DocumentObjectGroupPython] G4_Fe  # scripted group (container) (typed FeaturePython)
  Dunit = g/cm3
  Dvalue = 7.874
  Group = -> [Fe_element007]
  conduct = 2
  density = 1
  expand = 3
  formula = Fe
  name = G4_Fe
  specific = 4
FEATURE [App::DocumentObjectGroupPython] Co_element001  label="Co_element : 1"  # scripted group (container) (typed FeaturePython)
  n = 1
  ref = Co_element
FEATURE [App::DocumentObjectGroupPython] G4_Co  # scripted group (container) (typed FeaturePython)
  Dunit = g/cm3
  Dvalue = 8.9
  Group = -> [Co_element001]
  conduct = 2
  density = 1
  expand = 3
  formula = Co
  name = G4_Co
  specific = 4
FEATURE [App::DocumentObjectGroupPython] Ni_element001  label="Ni_element : 1"  # scripted group (container) (typed FeaturePython)
  n = 1
  ref = Ni_element
FEATURE [App::DocumentObjectGroupPython] G4_Ni  # scripted group (container) (typed FeaturePython)
  Dunit = g/cm3
  Dvalue = 8.902
  Group = -> [Ni_element001]
  conduct = 2
  density = 1
  expand = 3
  formula = Ni
  name = G4_Ni
  specific = 4
FEATURE [App::DocumentObjectGroupPython] Cu_element001  label="Cu_element : 1"  # scripted group (container) (typed FeaturePython)
  n = 1
  ref = Cu_element
FEATURE [App::DocumentObjectGroupPython] G4_Cu  # scripted group (container) (typed FeaturePython)
  Dunit = g/cm3
  Dvalue = 8.96
  Group = -> [Cu_element001]
  conduct = 2
  density = 1
  expand = 3
  formula = Cu
  name = G4_Cu
  specific = 4
FEATURE [App::DocumentObjectGroupPython] Zn_element001  label="Zn_element : 1"  # scripted group (container) (typed FeaturePython)
  n = 1
  ref = Zn_element
FEATURE [App::DocumentObjectGroupPython] G4_Zn  # scripted group (container) (typed FeaturePython)
  Dunit = g/cm3
  Dvalue = 7.133
  Group = -> [Zn_element001]
  conduct = 2
  density = 1
  expand = 3
  formula = Zn
  name = G4_Zn
  specific = 4
FEATURE [App::DocumentObjectGroupPython] Ga_element002  label="Ga_element : 002"  # scripted group (container) (typed FeaturePython)
  n = 1
  ref = Ga_element
FEATURE [App::DocumentObjectGroupPython] G4_Ga  # scripted group (container) (typed FeaturePython)
  Dunit = g/cm3
  Dvalue = 5.904
  Group = -> [Ga_element002]
  conduct = 2
  density = 1
  expand = 3
  formula = Ga
  name = G4_Ga
  specific = 4
FEATURE [App::DocumentObjectGroupPython] Ge_element002  label="Ge_element : 1"  # scripted group (container) (typed FeaturePython)
  n = 1
  ref = Ge_element
FEATURE [App::DocumentObjectGroupPython] G4_Ge  # scripted group (container) (typed FeaturePython)
  Dunit = g/cm3
  Dvalue = 5.323
  Group = -> [Ge_element002]
  conduct = 2
  density = 1
  expand = 3
  formula = Ge
  name = G4_Ge
  specific = 4
FEATURE [App::DocumentObjectGroupPython] As_element003  label="As_element : 002"  # scripted group (container) (typed FeaturePython)
  n = 1
  ref = As_element
FEATURE [App::DocumentObjectGroupPython] G4_As  # scripted group (container) (typed FeaturePython)
  Dunit = g/cm3
  Dvalue = 5.73
  Group = -> [As_element003]
  conduct = 2
  density = 1
  expand = 3
  formula = As
  name = G4_As
  specific = 4
FEATURE [App::DocumentObjectGroupPython] Se_element001  label="Se_element : 1"  # scripted group (container) (typed FeaturePython)
  n = 1
  ref = Se_element
FEATURE [App::DocumentObjectGroupPython] G4_Se  # scripted group (container) (typed FeaturePython)
  Dunit = g/cm3
  Dvalue = 4.5
  Group = -> [Se_element001]
  conduct = 2
  density = 1
  expand = 3
  formula = Se
  name = G4_Se
  specific = 4
FEATURE [App::DocumentObjectGroupPython] Br_element007  label="Br_element : 004"  # scripted group (container) (typed FeaturePython)
  n = 1
  ref = Br_element
FEATURE [App::DocumentObjectGroupPython] G4_Br  # scripted group (container) (typed FeaturePython)
  Dunit = g/cm3
  Dvalue = 0.0070721
  Group = -> [Br_element007]
  conduct = 2
  density = 1
  expand = 3
  formula = Br
  name = G4_Br
  specific = 4
FEATURE [App::DocumentObjectGroupPython] Kr_element001  label="Kr_element : 1"  # scripted group (container) (typed FeaturePython)
  n = 1
  ref = Kr_element
FEATURE [App::DocumentObjectGroupPython] G4_Kr  # scripted group (container) (typed FeaturePython)
  Dunit = g/cm3
  Dvalue = 0.00347832
  Group = -> [Kr_element001]
  conduct = 2
  density = 1
  expand = 3
  formula = Kr
  name = G4_Kr
  specific = 4
FEATURE [App::DocumentObjectGroupPython] Rb_element001  label="Rb_element : 1"  # scripted group (container) (typed FeaturePython)
  n = 1
  ref = Rb_element
FEATURE [App::DocumentObjectGroupPython] G4_Rb  # scripted group (container) (typed FeaturePython)
  Dunit = g/cm3
  Dvalue = 1.532
  Group = -> [Rb_element001]
  conduct = 2
  density = 1
  expand = 3
  formula = Rb
  name = G4_Rb
  specific = 4
FEATURE [App::DocumentObjectGroupPython] Sr_element001  label="Sr_element : 1"  # scripted group (container) (typed FeaturePython)
  n = 1
  ref = Sr_element
FEATURE [App::DocumentObjectGroupPython] G4_Sr  # scripted group (container) (typed FeaturePython)
  Dunit = g/cm3
  Dvalue = 2.54
  Group = -> [Sr_element001]
  conduct = 2
  density = 1
  expand = 3
  formula = Sr
  name = G4_Sr
  specific = 4
FEATURE [App::DocumentObjectGroupPython] Y_element001  label="Y_element : 1"  # scripted group (container) (typed FeaturePython)
  n = 1
  ref = Y_element
FEATURE [App::DocumentObjectGroupPython] G4_Y  # scripted group (container) (typed FeaturePython)
  Dunit = g/cm3
  Dvalue = 4.469
  Group = -> [Y_element001]
  conduct = 2
  density = 1
  expand = 3
  formula = Y
  name = G4_Y
  specific = 4
FEATURE [App::DocumentObjectGroupPython] Zr_element001  label="Zr_element : 1"  # scripted group (container) (typed FeaturePython)
  n = 1
  ref = Zr_element
FEATURE [App::DocumentObjectGroupPython] G4_Zr  # scripted group (container) (typed FeaturePython)
  Dunit = g/cm3
  Dvalue = 6.506
  Group = -> [Zr_element001]
  conduct = 2
  density = 1
  expand = 3
  formula = Zr
  name = G4_Zr
  specific = 4
FEATURE [App::DocumentObjectGroupPython] Nb_element001  label="Nb_element : 1"  # scripted group (container) (typed FeaturePython)
  n = 1
  ref = Nb_element
FEATURE [App::DocumentObjectGroupPython] G4_Nb  # scripted group (container) (typed FeaturePython)
  Dunit = g/cm3
  Dvalue = 8.57
  Group = -> [Nb_element001]
  conduct = 2
  density = 1
  expand = 3
  formula = Nb
  name = G4_Nb
  specific = 4
FEATURE [App::DocumentObjectGroupPython] Mo_element001  label="Mo_element : 1"  # scripted group (container) (typed FeaturePython)
  n = 1
  ref = Mo_element
FEATURE [App::DocumentObjectGroupPython] G4_Mo  # scripted group (container) (typed FeaturePython)
  Dunit = g/cm3
  Dvalue = 10.22
  Group = -> [Mo_element001]
  conduct = 2
  density = 1
  expand = 3
  formula = Mo
  name = G4_Mo
  specific = 4
FEATURE [App::DocumentObjectGroupPython] Tc_element001  label="Tc_element : 1"  # scripted group (container) (typed FeaturePython)
  n = 1
  ref = Tc_element
FEATURE [App::DocumentObjectGroupPython] G4_Tc  # scripted group (container) (typed FeaturePython)
  Dunit = g/cm3
  Dvalue = 11.5
  Group = -> [Tc_element001]
  conduct = 2
  density = 1
  expand = 3
  formula = Tc
  name = G4_Tc
  specific = 4
FEATURE [App::DocumentObjectGroupPython] Ru_element001  label="Ru_element : 1"  # scripted group (container) (typed FeaturePython)
  n = 1
  ref = Ru_element
FEATURE [App::DocumentObjectGroupPython] G4_Ru  # scripted group (container) (typed FeaturePython)
  Dunit = g/cm3
  Dvalue = 12.41
  Group = -> [Ru_element001]
  conduct = 2
  density = 1
  expand = 3
  formula = Ru
  name = G4_Ru
  specific = 4
FEATURE [App::DocumentObjectGroupPython] Rh_element001  label="Rh_element : 1"  # scripted group (container) (typed FeaturePython)
  n = 1
  ref = Rh_element
FEATURE [App::DocumentObjectGroupPython] G4_Rh  # scripted group (container) (typed FeaturePython)
  Dunit = g/cm3
  Dvalue = 12.41
  Group = -> [Rh_element001]
  conduct = 2
  density = 1
  expand = 3
  formula = Rh
  name = G4_Rh
  specific = 4
FEATURE [App::DocumentObjectGroupPython] Pd_element001  label="Pd_element : 1"  # scripted group (container) (typed FeaturePython)
  n = 1
  ref = Pd_element
FEATURE [App::DocumentObjectGroupPython] G4_Pd  # scripted group (container) (typed FeaturePython)
  Dunit = g/cm3
  Dvalue = 12.02
  Group = -> [Pd_element001]
  conduct = 2
  density = 1
  expand = 3
  formula = Pd
  name = G4_Pd
  specific = 4
FEATURE [App::DocumentObjectGroupPython] Ag_element006  label="Ag_element : 004"  # scripted group (container) (typed FeaturePython)
  n = 1
  ref = Ag_element
FEATURE [App::DocumentObjectGroupPython] G4_Ag  # scripted group (container) (typed FeaturePython)
  Dunit = g/cm3
  Dvalue = 10.5
  Group = -> [Ag_element006]
  conduct = 2
  density = 1
  expand = 3
  formula = Ag
  name = G4_Ag
  specific = 4
FEATURE [App::DocumentObjectGroupPython] Cd_element003  label="Cd_element : 003"  # scripted group (container) (typed FeaturePython)
  n = 1
  ref = Cd_element
FEATURE [App::DocumentObjectGroupPython] G4_Cd  # scripted group (container) (typed FeaturePython)
  Dunit = g/cm3
  Dvalue = 8.65
  Group = -> [Cd_element003]
  conduct = 2
  density = 1
  expand = 3
  formula = Cd
  name = G4_Cd
  specific = 4
FEATURE [App::DocumentObjectGroupPython] In_element001  label="In_element : 1"  # scripted group (container) (typed FeaturePython)
  n = 1
  ref = In_element
FEATURE [App::DocumentObjectGroupPython] G4_In  # scripted group (container) (typed FeaturePython)
  Dunit = g/cm3
  Dvalue = 7.31
  Group = -> [In_element001]
  conduct = 2
  density = 1
  expand = 3
  formula = In
  name = G4_In
  specific = 4
FEATURE [App::DocumentObjectGroupPython] Sn_element001  label="Sn_element : 1"  # scripted group (container) (typed FeaturePython)
  n = 1
  ref = Sn_element
FEATURE [App::DocumentObjectGroupPython] G4_Sn  # scripted group (container) (typed FeaturePython)
  Dunit = g/cm3
  Dvalue = 7.31
  Group = -> [Sn_element001]
  conduct = 2
  density = 1
  expand = 3
  formula = Sn
  name = G4_Sn
  specific = 4
FEATURE [App::DocumentObjectGroupPython] Sb_element001  label="Sb_element : 1"  # scripted group (container) (typed FeaturePython)
  n = 1
  ref = Sb_element
FEATURE [App::DocumentObjectGroupPython] G4_Sb  # scripted group (container) (typed FeaturePython)
  Dunit = g/cm3
  Dvalue = 6.691
  Group = -> [Sb_element001]
  conduct = 2
  density = 1
  expand = 3
  formula = Sb
  name = G4_Sb
  specific = 4
FEATURE [App::DocumentObjectGroupPython] Te_element002  label="Te_element : 002"  # scripted group (container) (typed FeaturePython)
  n = 1
  ref = Te_element
FEATURE [App::DocumentObjectGroupPython] G4_Te  # scripted group (container) (typed FeaturePython)
  Dunit = g/cm3
  Dvalue = 6.24
  Group = -> [Te_element002]
  conduct = 2
  density = 1
  expand = 3
  formula = Te
  name = G4_Te
  specific = 4
FEATURE [App::DocumentObjectGroupPython] I_element010  label="I_element : 006"  # scripted group (container) (typed FeaturePython)
  n = 1
  ref = I_element
FEATURE [App::DocumentObjectGroupPython] G4_I  # scripted group (container) (typed FeaturePython)
  Dunit = g/cm3
  Dvalue = 4.93
  Group = -> [I_element010]
  conduct = 2
  density = 1
  expand = 3
  formula = I
  name = G4_I
  specific = 4
FEATURE [App::DocumentObjectGroupPython] Xe_element001  label="Xe_element : 1"  # scripted group (container) (typed FeaturePython)
  n = 1
  ref = Xe_element
FEATURE [App::DocumentObjectGroupPython] G4_Xe  # scripted group (container) (typed FeaturePython)
  Dunit = g/cm3
  Dvalue = 0.00548536
  Group = -> [Xe_element001]
  conduct = 2
  density = 1
  expand = 3
  formula = Xe
  name = G4_Xe
  specific = 4
FEATURE [App::DocumentObjectGroupPython] Cs_element003  label="Cs_element : 003"  # scripted group (container) (typed FeaturePython)
  n = 1
  ref = Cs_element
FEATURE [App::DocumentObjectGroupPython] G4_Cs  # scripted group (container) (typed FeaturePython)
  Dunit = g/cm3
  Dvalue = 1.873
  Group = -> [Cs_element003]
  conduct = 2
  density = 1
  expand = 3
  formula = Cs
  name = G4_Cs
  specific = 4
FEATURE [App::DocumentObjectGroupPython] Ba_element003  label="Ba_element : 003"  # scripted group (container) (typed FeaturePython)
  n = 1
  ref = Ba_element
FEATURE [App::DocumentObjectGroupPython] G4_Ba  # scripted group (container) (typed FeaturePython)
  Dunit = g/cm3
  Dvalue = 3.5
  Group = -> [Ba_element003]
  conduct = 2
  density = 1
  expand = 3
  formula = Ba
  name = G4_Ba
  specific = 4
FEATURE [App::DocumentObjectGroupPython] La_element003  label="La_element : 003"  # scripted group (container) (typed FeaturePython)
  n = 1
  ref = La_element
FEATURE [App::DocumentObjectGroupPython] G4_La  # scripted group (container) (typed FeaturePython)
  Dunit = g/cm3
  Dvalue = 6.154
  Group = -> [La_element003]
  conduct = 2
  density = 1
  expand = 3
  formula = La
  name = G4_La
  specific = 4
FEATURE [App::DocumentObjectGroupPython] Ce_element002  label="Ce_element : 1"  # scripted group (container) (typed FeaturePython)
  n = 1
  ref = Ce_element
FEATURE [App::DocumentObjectGroupPython] G4_Ce  # scripted group (container) (typed FeaturePython)
  Dunit = g/cm3
  Dvalue = 6.657
  Group = -> [Ce_element002]
  conduct = 2
  density = 1
  expand = 3
  formula = Ce
  name = G4_Ce
  specific = 4
FEATURE [App::DocumentObjectGroupPython] Pr_element001  label="Pr_element : 1"  # scripted group (container) (typed FeaturePython)
  n = 1
  ref = Pr_element
FEATURE [App::DocumentObjectGroupPython] G4_Pr  # scripted group (container) (typed FeaturePython)
  Dunit = g/cm3
  Dvalue = 6.71
  Group = -> [Pr_element001]
  conduct = 2
  density = 1
  expand = 3
  formula = Pr
  name = G4_Pr
  specific = 4
FEATURE [App::DocumentObjectGroupPython] Nd_element001  label="Nd_element : 1"  # scripted group (container) (typed FeaturePython)
  n = 1
  ref = Nd_element
FEATURE [App::DocumentObjectGroupPython] G4_Nd  # scripted group (container) (typed FeaturePython)
  Dunit = g/cm3
  Dvalue = 6.9
  Group = -> [Nd_element001]
  conduct = 2
  density = 1
  expand = 3
  formula = Nd
  name = G4_Nd
  specific = 4
FEATURE [App::DocumentObjectGroupPython] Pm_element001  label="Pm_element : 1"  # scripted group (container) (typed FeaturePython)
  n = 1
  ref = Pm_element
FEATURE [App::DocumentObjectGroupPython] G4_Pm  # scripted group (container) (typed FeaturePython)
  Dunit = g/cm3
  Dvalue = 7.22
  Group = -> [Pm_element001]
  conduct = 2
  density = 1
  expand = 3
  formula = Pm
  name = G4_Pm
  specific = 4
FEATURE [App::DocumentObjectGroupPython] Sm_element001  label="Sm_element : 1"  # scripted group (container) (typed FeaturePython)
  n = 1
  ref = Sm_element
FEATURE [App::DocumentObjectGroupPython] G4_Sm  # scripted group (container) (typed FeaturePython)
  Dunit = g/cm3
  Dvalue = 7.46
  Group = -> [Sm_element001]
  conduct = 2
  density = 1
  expand = 3
  formula = Sm
  name = G4_Sm
  specific = 4
FEATURE [App::DocumentObjectGroupPython] Eu_element001  label="Eu_element : 1"  # scripted group (container) (typed FeaturePython)
  n = 1
  ref = Eu_element
FEATURE [App::DocumentObjectGroupPython] G4_Eu  # scripted group (container) (typed FeaturePython)
  Dunit = g/cm3
  Dvalue = 5.243
  Group = -> [Eu_element001]
  conduct = 2
  density = 1
  expand = 3
  formula = Eu
  name = G4_Eu
  specific = 4
FEATURE [App::DocumentObjectGroupPython] Gd_element002  label="Gd_element : 1"  # scripted group (container) (typed FeaturePython)
  n = 1
  ref = Gd_element
FEATURE [App::DocumentObjectGroupPython] G4_Gd  # scripted group (container) (typed FeaturePython)
  Dunit = g/cm3
  Dvalue = 7.9004
  Group = -> [Gd_element002]
  conduct = 2
  density = 1
  expand = 3
  formula = Gd
  name = G4_Gd
  specific = 4
FEATURE [App::DocumentObjectGroupPython] Tb_element001  label="Tb_element : 1"  # scripted group (container) (typed FeaturePython)
  n = 1
  ref = Tb_element
FEATURE [App::DocumentObjectGroupPython] G4_Tb  # scripted group (container) (typed FeaturePython)
  Dunit = g/cm3
  Dvalue = 8.229
  Group = -> [Tb_element001]
  conduct = 2
  density = 1
  expand = 3
  formula = Tb
  name = G4_Tb
  specific = 4
FEATURE [App::DocumentObjectGroupPython] Dy_element001  label="Dy_element : 1"  # scripted group (container) (typed FeaturePython)
  n = 1
  ref = Dy_element
FEATURE [App::DocumentObjectGroupPython] G4_Dy  # scripted group (container) (typed FeaturePython)
  Dunit = g/cm3
  Dvalue = 8.55
  Group = -> [Dy_element001]
  conduct = 2
  density = 1
  expand = 3
  formula = Dy
  name = G4_Dy
  specific = 4
FEATURE [App::DocumentObjectGroupPython] Ho_element001  label="Ho_element : 1"  # scripted group (container) (typed FeaturePython)
  n = 1
  ref = Ho_element
FEATURE [App::DocumentObjectGroupPython] G4_Ho  # scripted group (container) (typed FeaturePython)
  Dunit = g/cm3
  Dvalue = 8.795
  Group = -> [Ho_element001]
  conduct = 2
  density = 1
  expand = 3
  formula = Ho
  name = G4_Ho
  specific = 4
FEATURE [App::DocumentObjectGroupPython] Er_element001  label="Er_element : 1"  # scripted group (container) (typed FeaturePython)
  n = 1
  ref = Er_element
FEATURE [App::DocumentObjectGroupPython] G4_Er  # scripted group (container) (typed FeaturePython)
  Dunit = g/cm3
  Dvalue = 9.066
  Group = -> [Er_element001]
  conduct = 2
  density = 1
  expand = 3
  formula = Er
  name = G4_Er
  specific = 4
FEATURE [App::DocumentObjectGroupPython] Tm_element001  label="Tm_element : 1"  # scripted group (container) (typed FeaturePython)
  n = 1
  ref = Tm_element
FEATURE [App::DocumentObjectGroupPython] G4_Tm  # scripted group (container) (typed FeaturePython)
  Dunit = g/cm3
  Dvalue = 9.321
  Group = -> [Tm_element001]
  conduct = 2
  density = 1
  expand = 3
  formula = Tm
  name = G4_Tm
  specific = 4
FEATURE [App::DocumentObjectGroupPython] Yb_element001  label="Yb_element : 1"  # scripted group (container) (typed FeaturePython)
  n = 1
  ref = Yb_element
FEATURE [App::DocumentObjectGroupPython] G4_Yb  # scripted group (container) (typed FeaturePython)
  Dunit = g/cm3
  Dvalue = 6.73
  Group = -> [Yb_element001]
  conduct = 2
  density = 1
  expand = 3
  formula = Yb
  name = G4_Yb
  specific = 4
FEATURE [App::DocumentObjectGroupPython] Lu_element001  label="Lu_element : 1"  # scripted group (container) (typed FeaturePython)
  n = 1
  ref = Lu_element
FEATURE [App::DocumentObjectGroupPython] G4_Lu  # scripted group (container) (typed FeaturePython)
  Dunit = g/cm3
  Dvalue = 9.84
  Group = -> [Lu_element001]
  conduct = 2
  density = 1
  expand = 3
  formula = Lu
  name = G4_Lu
  specific = 4
FEATURE [App::DocumentObjectGroupPython] Hf_element001  label="Hf_element : 1"  # scripted group (container) (typed FeaturePython)
  n = 1
  ref = Hf_element
FEATURE [App::DocumentObjectGroupPython] G4_Hf  # scripted group (container) (typed FeaturePython)
  Dunit = g/cm3
  Dvalue = 13.31
  Group = -> [Hf_element001]
  conduct = 2
  density = 1
  expand = 3
  formula = Hf
  name = G4_Hf
  specific = 4
FEATURE [App::DocumentObjectGroupPython] Ta_element001  label="Ta_element : 1"  # scripted group (container) (typed FeaturePython)
  n = 1
  ref = Ta_element
FEATURE [App::DocumentObjectGroupPython] G4_Ta  # scripted group (container) (typed FeaturePython)
  Dunit = g/cm3
  Dvalue = 16.654
  Group = -> [Ta_element001]
  conduct = 2
  density = 1
  expand = 3
  formula = Ta
  name = G4_Ta
  specific = 4
FEATURE [App::DocumentObjectGroupPython] W_element004  label="W_element : 004"  # scripted group (container) (typed FeaturePython)
  n = 1
  ref = W_element
FEATURE [App::DocumentObjectGroupPython] G4_W  # scripted group (container) (typed FeaturePython)
  Dunit = g/cm3
  Dvalue = 19.3
  Group = -> [W_element004]
  conduct = 2
  density = 1
  expand = 3
  formula = W
  name = G4_W
  specific = 4
FEATURE [App::DocumentObjectGroupPython] Re_element001  label="Re_element : 1"  # scripted group (container) (typed FeaturePython)
  n = 1
  ref = Re_element
FEATURE [App::DocumentObjectGroupPython] G4_Re  # scripted group (container) (typed FeaturePython)
  Dunit = g/cm3
  Dvalue = 21.02
  Group = -> [Re_element001]
  conduct = 2
  density = 1
  expand = 3
  formula = Re
  name = G4_Re
  specific = 4
FEATURE [App::DocumentObjectGroupPython] Os_element001  label="Os_element : 1"  # scripted group (container) (typed FeaturePython)
  n = 1
  ref = Os_element
FEATURE [App::DocumentObjectGroupPython] G4_Os  # scripted group (container) (typed FeaturePython)
  Dunit = g/cm3
  Dvalue = 22.57
  Group = -> [Os_element001]
  conduct = 2
  density = 1
  expand = 3
  formula = Os
  name = G4_Os
  specific = 4
FEATURE [App::DocumentObjectGroupPython] Ir_element001  label="Ir_element : 1"  # scripted group (container) (typed FeaturePython)
  n = 1
  ref = Ir_element
FEATURE [App::DocumentObjectGroupPython] G4_Ir  # scripted group (container) (typed FeaturePython)
  Dunit = g/cm3
  Dvalue = 22.42
  Group = -> [Ir_element001]
  conduct = 2
  density = 1
  expand = 3
  formula = Ir
  name = G4_Ir
  specific = 4
FEATURE [App::DocumentObjectGroupPython] Pt_element001  label="Pt_element : 1"  # scripted group (container) (typed FeaturePython)
  n = 1
  ref = Pt_element
FEATURE [App::DocumentObjectGroupPython] G4_Pt  # scripted group (container) (typed FeaturePython)
  Dunit = g/cm3
  Dvalue = 21.45
  Group = -> [Pt_element001]
  conduct = 2
  density = 1
  expand = 3
  formula = Pt
  name = G4_Pt
  specific = 4
FEATURE [App::DocumentObjectGroupPython] Au_element001  label="Au_element : 1"  # scripted group (container) (typed FeaturePython)
  n = 1
  ref = Au_element
FEATURE [App::DocumentObjectGroupPython] G4_Au  # scripted group (container) (typed FeaturePython)
  Dunit = g/cm3
  Dvalue = 19.32
  Group = -> [Au_element001]
  conduct = 2
  density = 1
  expand = 3
  formula = Au
  name = G4_Au
  specific = 4
FEATURE [App::DocumentObjectGroupPython] Hg_element002  label="Hg_element : 002"  # scripted group (container) (typed FeaturePython)
  n = 1
  ref = Hg_element
FEATURE [App::DocumentObjectGroupPython] G4_Hg  # scripted group (container) (typed FeaturePython)
  Dunit = g/cm3
  Dvalue = 13.546
  Group = -> [Hg_element002]
  conduct = 2
  density = 1
  expand = 3
  formula = Hg
  name = G4_Hg
  specific = 4
FEATURE [App::DocumentObjectGroupPython] Tl_element002  label="Tl_element : 002"  # scripted group (container) (typed FeaturePython)
  n = 1
  ref = Tl_element
FEATURE [App::DocumentObjectGroupPython] G4_Tl  # scripted group (container) (typed FeaturePython)
  Dunit = g/cm3
  Dvalue = 11.72
  Group = -> [Tl_element002]
  conduct = 2
  density = 1
  expand = 3
  formula = Tl
  name = G4_Tl
  specific = 4
FEATURE [App::DocumentObjectGroupPython] Pb_element003  label="Pb_element : 1"  # scripted group (container) (typed FeaturePython)
  n = 1
  ref = Pb_element
FEATURE [App::DocumentObjectGroupPython] G4_Pb  # scripted group (container) (typed FeaturePython)
  Dunit = g/cm3
  Dvalue = 11.35
  Group = -> [Pb_element003]
  conduct = 2
  density = 1
  expand = 3
  formula = Pb
  name = G4_Pb
  specific = 4
FEATURE [App::DocumentObjectGroupPython] Bi_element002  label="Bi_element : 1"  # scripted group (container) (typed FeaturePython)
  n = 1
  ref = Bi_element
FEATURE [App::DocumentObjectGroupPython] G4_Bi  # scripted group (container) (typed FeaturePython)
  Dunit = g/cm3
  Dvalue = 9.747
  Group = -> [Bi_element002]
  conduct = 2
  density = 1
  expand = 3
  formula = Bi
  name = G4_Bi
  specific = 4
FEATURE [App::DocumentObjectGroupPython] Po_element001  label="Po_element : 1"  # scripted group (container) (typed FeaturePython)
  n = 1
  ref = Po_element
FEATURE [App::DocumentObjectGroupPython] G4_Po  # scripted group (container) (typed FeaturePython)
  Dunit = g/cm3
  Dvalue = 9.32
  Group = -> [Po_element001]
  conduct = 2
  density = 1
  expand = 3
  formula = Po
  name = G4_Po
  specific = 4
FEATURE [App::DocumentObjectGroupPython] At_element001  label="At_element : 1"  # scripted group (container) (typed FeaturePython)
  n = 1
  ref = At_element
FEATURE [App::DocumentObjectGroupPython] G4_At  # scripted group (container) (typed FeaturePython)
  Dunit = g/cm3
  Dvalue = 9.32
  Group = -> [At_element001]
  conduct = 2
  density = 1
  expand = 3
  formula = At
  name = G4_At
  specific = 4
FEATURE [App::DocumentObjectGroupPython] Rn_element001  label="Rn_element : 1"  # scripted group (container) (typed FeaturePython)
  n = 1
  ref = Rn_element
FEATURE [App::DocumentObjectGroupPython] G4_Rn  # scripted group (container) (typed FeaturePython)
  Dunit = g/cm3
  Dvalue = 0.00900662
  Group = -> [Rn_element001]
  conduct = 2
  density = 1
  expand = 3
  formula = Rn
  name = G4_Rn
  specific = 4
FEATURE [App::DocumentObjectGroupPython] Fr_element001  label="Fr_element : 1"  # scripted group (container) (typed FeaturePython)
  n = 1
  ref = Fr_element
FEATURE [App::DocumentObjectGroupPython] G4_Fr  # scripted group (container) (typed FeaturePython)
  Dunit = g/cm3
  Dvalue = 1
  Group = -> [Fr_element001]
  conduct = 2
  density = 1
  expand = 3
  formula = Fr
  name = G4_Fr
  specific = 4
FEATURE [App::DocumentObjectGroupPython] Ra_element001  label="Ra_element : 1"  # scripted group (container) (typed FeaturePython)
  n = 1
  ref = Ra_element
FEATURE [App::DocumentObjectGroupPython] G4_Ra  # scripted group (container) (typed FeaturePython)
  Dunit = g/cm3
  Dvalue = 5
  Group = -> [Ra_element001]
  conduct = 2
  density = 1
  expand = 3
  formula = Ra
  name = G4_Ra
  specific = 4
FEATURE [App::DocumentObjectGroupPython] Ac_element001  label="Ac_element : 1"  # scripted group (container) (typed FeaturePython)
  n = 1
  ref = Ac_element
FEATURE [App::DocumentObjectGroupPython] G4_Ac  # scripted group (container) (typed FeaturePython)
  Dunit = g/cm3
  Dvalue = 10.07
  Group = -> [Ac_element001]
  conduct = 2
  density = 1
  expand = 3
  formula = Ac
  name = G4_Ac
  specific = 4
FEATURE [App::DocumentObjectGroupPython] Th_element001  label="Th_element : 1"  # scripted group (container) (typed FeaturePython)
  n = 1
  ref = Th_element
FEATURE [App::DocumentObjectGroupPython] G4_Th  # scripted group (container) (typed FeaturePython)
  Dunit = g/cm3
  Dvalue = 11.72
  Group = -> [Th_element001]
  conduct = 2
  density = 1
  expand = 3
  formula = Th
  name = G4_Th
  specific = 4
FEATURE [App::DocumentObjectGroupPython] Pa_element001  label="Pa_element : 1"  # scripted group (container) (typed FeaturePython)
  n = 1
  ref = Pa_element
FEATURE [App::DocumentObjectGroupPython] G4_Pa  # scripted group (container) (typed FeaturePython)
  Dunit = g/cm3
  Dvalue = 15.37
  Group = -> [Pa_element001]
  conduct = 2
  density = 1
  expand = 3
  formula = Pa
  name = G4_Pa
  specific = 4
FEATURE [App::DocumentObjectGroupPython] U_element004  label="U_element : 004"  # scripted group (container) (typed FeaturePython)
  n = 1
  ref = U_element
FEATURE [App::DocumentObjectGroupPython] G4_U  # scripted group (container) (typed FeaturePython)
  Dunit = g/cm3
  Dvalue = 18.95
  Group = -> [U_element004]
  conduct = 2
  density = 1
  expand = 3
  formula = U
  name = G4_U
  specific = 4
FEATURE [App::DocumentObjectGroupPython] Np_element001  label="Np_element : 1"  # scripted group (container) (typed FeaturePython)
  n = 1
  ref = Np_element
FEATURE [App::DocumentObjectGroupPython] G4_Np  # scripted group (container) (typed FeaturePython)
  Dunit = g/cm3
  Dvalue = 20.25
  Group = -> [Np_element001]
  conduct = 2
  density = 1
  expand = 3
  formula = Np
  name = G4_Np
  specific = 4
FEATURE [App::DocumentObjectGroupPython] Pu_element002  label="Pu_element : 002"  # scripted group (container) (typed FeaturePython)
  n = 1
  ref = Pu_element
FEATURE [App::DocumentObjectGroupPython] G4_Pu  # scripted group (container) (typed FeaturePython)
  Dunit = g/cm3
  Dvalue = 19.84
  Group = -> [Pu_element002]
  conduct = 2
  density = 1
  expand = 3
  formula = Pu
  name = G4_Pu
  specific = 4
FEATURE [App::DocumentObjectGroupPython] Am_element001  label="Am_element : 1"  # scripted group (container) (typed FeaturePython)
  n = 1
  ref = Am_element
FEATURE [App::DocumentObjectGroupPython] G4_Am  # scripted group (container) (typed FeaturePython)
  Dunit = g/cm3
  Dvalue = 13.67
  Group = -> [Am_element001]
  conduct = 2
  density = 1
  expand = 3
  formula = Am
  name = G4_Am
  specific = 4
FEATURE [App::DocumentObjectGroupPython] Cm_element001  label="Cm_element : 1"  # scripted group (container) (typed FeaturePython)
  n = 1
  ref = Cm_element
FEATURE [App::DocumentObjectGroupPython] G4_Cm  # scripted group (container) (typed FeaturePython)
  Dunit = g/cm3
  Dvalue = 13.51
  Group = -> [Cm_element001]
  conduct = 2
  density = 1
  expand = 3
  formula = Cm
  name = G4_Cm
  specific = 4
FEATURE [App::DocumentObjectGroupPython] Bk_element001  label="Bk_element : 1"  # scripted group (container) (typed FeaturePython)
  n = 1
  ref = Bk_element
FEATURE [App::DocumentObjectGroupPython] G4_Bk  # scripted group (container) (typed FeaturePython)
  Dunit = g/cm3
  Dvalue = 14
  Group = -> [Bk_element001]
  conduct = 2
  density = 1
  expand = 3
  formula = Bk
  name = G4_Bk
  specific = 4
FEATURE [App::DocumentObjectGroupPython] Cf_element001  label="Cf_element : 1"  # scripted group (container) (typed FeaturePython)
  n = 1
  ref = Cf_element
FEATURE [App::DocumentObjectGroupPython] G4_Cf  # scripted group (container) (typed FeaturePython)
  Dunit = g/cm3
  Dvalue = 10
  Group = -> [Cf_element001]
  conduct = 2
  density = 1
  expand = 3
  formula = Cf
  name = G4_Cf
  specific = 4
FEATURE [App::DocumentObjectGroupPython] Element  # scripted group (container) (typed FeaturePython)
  Group = -> [G4_H,G4_He,G4_Li,G4_Be,G4_B,G4_C,G4_N,G4_O,G4_F,G4_Ne,G4_Na,G4_Mg,G4_Al,G4_Si,G4_P,G4_S,G4_Cl,G4_Ar,G4_K,G4_Ca,G4_Sc,G4_Ti,G4_V,G4_Cr,G4_Mn,G4_Fe,G4_Co,G4_Ni,G4_Cu,G4_Zn,G4_Ga,G4_Ge,G4_As,G4_Se,G4_Br,G4_Kr,G4_Rb,G4_Sr,G4_Y,G4_Zr,G4_Nb,G4_Mo,G4_Tc,G4_Ru,G4_Rh,G4_Pd,G4_Ag,G4_Cd,G4_In,G4_Sn,G4_Sb,G4_Te,G4_I,G4_Xe,G4_Cs,G4_Ba,G4_La,G4_Ce,G4_Pr,G4_Nd,G4_Pm,G4_Sm,G4_Eu,G4_Gd,G4_Tb,G4_Dy,G4_Ho,G4_Er,+30 more]
FEATURE [App::DocumentObjectGroupPython] H_element114  label="H_element : 063"  # scripted group (container) (typed FeaturePython)
  n = 2
  ref = H_element
FEATURE [App::DocumentObjectGroupPython] G4_lH2  # scripted group (container) (typed FeaturePython)
  Dunit = g/cm3
  Dvalue = 0.0708
  Group = -> [H_element114]
  conduct = 2
  density = 1
  expand = 3
  formula = G4_lH2
  name = G4_lH2
  specific = 4
FEATURE [App::DocumentObjectGroupPython] N_element049  label="N_element : 022"  # scripted group (container) (typed FeaturePython)
  n = 2
  ref = N_element
FEATURE [App::DocumentObjectGroupPython] G4_lN2  # scripted group (container) (typed FeaturePython)
  Dunit = g/cm3
  Dvalue = 0.807
  Group = -> [N_element049]
  conduct = 2
  density = 1
  expand = 3
  formula = G4_lN2
  name = G4_lN2
  specific = 4
FEATURE [App::DocumentObjectGroupPython] O_element106  label="O_element : 060"  # scripted group (container) (typed FeaturePython)
  n = 2
  ref = O_element
FEATURE [App::DocumentObjectGroupPython] G4_lO2  # scripted group (container) (typed FeaturePython)
  Dunit = g/cm3
  Dvalue = 1.141
  Group = -> [O_element106]
  conduct = 2
  density = 1
  expand = 3
  formula = G4_lO2
  name = G4_lO2
  specific = 4
FEATURE [App::DocumentObjectGroupPython] Ar  label="Ar : 1"  # scripted group (container) (typed FeaturePython)
  n = 1
  ref = Ar
FEATURE [App::DocumentObjectGroupPython] G4_lAr  # scripted group (container) (typed FeaturePython)
  Dunit = g/cm3
  Dvalue = 1.396
  Group = -> [Ar]
  conduct = 2
  density = 1
  expand = 3
  formula = G4_lAr
  name = G4_lAr
  specific = 4
FEATURE [App::DocumentObjectGroupPython] Br  label="Br : 1"  # scripted group (container) (typed FeaturePython)
  n = 1
  ref = Br
FEATURE [App::DocumentObjectGroupPython] G4_lBr  # scripted group (container) (typed FeaturePython)
  Dunit = g/cm3
  Dvalue = 3.1028
  Group = -> [Br]
  conduct = 2
  density = 1
  expand = 3
  formula = G4_lBr
  name = G4_lBr
  specific = 4
FEATURE [App::DocumentObjectGroupPython] Kr  label="Kr : 1"  # scripted group (container) (typed FeaturePython)
  n = 1
  ref = Kr
FEATURE [App::DocumentObjectGroupPython] G4_lKr  # scripted group (container) (typed FeaturePython)
  Dunit = g/cm3
  Dvalue = 2.418
  Group = -> [Kr]
  conduct = 2
  density = 1
  expand = 3
  formula = G4_lKr
  name = G4_lKr
  specific = 4
FEATURE [App::DocumentObjectGroupPython] Xe  label="Xe : 1"  # scripted group (container) (typed FeaturePython)
  n = 1
  ref = Xe
FEATURE [App::DocumentObjectGroupPython] G4_lXe  # scripted group (container) (typed FeaturePython)
  Dunit = g/cm3
  Dvalue = 2.953
  Group = -> [Xe]
  conduct = 2
  density = 1
  expand = 3
  formula = G4_lXe
  name = G4_lXe
  specific = 4
FEATURE [App::DocumentObjectGroupPython] O_element107  label="O_element : 061"  # scripted group (container) (typed FeaturePython)
  n = 4
  ref = O_element
FEATURE [App::DocumentObjectGroupPython] Pb_element004  label="Pb_element : 002"  # scripted group (container) (typed FeaturePython)
  n = 1
  ref = Pb_element
FEATURE [App::DocumentObjectGroupPython] W_element005  label="W_element : 005"  # scripted group (container) (typed FeaturePython)
  n = 1
  ref = W_element
FEATURE [App::DocumentObjectGroupPython] G4_PbWO4  # scripted group (container) (typed FeaturePython)
  Dunit = g/cm3
  Dvalue = 8.28
  Group = -> [O_element107,Pb_element004,W_element005]
  conduct = 2
  density = 1
  expand = 3
  formula = G4_PbWO4
  name = G4_PbWO4
  specific = 4
FEATURE [App::DocumentObjectGroupPython] alactic  label="alactic : 1"  # scripted group (container) (typed FeaturePython)
  n = 1
  ref = alactic
FEATURE [App::DocumentObjectGroupPython] G4_Galactic  # scripted group (container) (typed FeaturePython)
  Dunit = g/cm3
  Dvalue = 0
  Group = -> [alactic]
  conduct = 2
  density = 1
  expand = 3
  formula = G4_Galactic
  name = G4_Galactic
  specific = 4
FEATURE [App::DocumentObjectGroupPython] RAPHITE_POROUS  label="RAPHITE_POROUS : 1"  # scripted group (container) (typed FeaturePython)
  n = 1
  ref = RAPHITE_POROUS
FEATURE [App::DocumentObjectGroupPython] G4_GRAPHITE_POROUS  # scripted group (container) (typed FeaturePython)
  Dunit = g/cm3
  Dvalue = 1.7
  Group = -> [RAPHITE_POROUS]
  conduct = 2
  density = 1
  expand = 3
  formula = G4_GRAPHITE_POROUS
  name = G4_GRAPHITE_POROUS
  specific = 4
FEATURE [App::DocumentObjectGroupPython] H_element115  label="H_element : 0.150"  # scripted group (container) (typed FeaturePython)
  n = 0.080538
FEATURE [App::DocumentObjectGroupPython] C_element125  label="C_element : 0.600"  # scripted group (container) (typed FeaturePython)
  n = 0.599848
FEATURE [App::DocumentObjectGroupPython] O_element108  label="O_element : 0.320"  # scripted group (container) (typed FeaturePython)
  n = 0.319614
FEATURE [App::DocumentObjectGroupPython] G4_LUCITE  # scripted group (container) (typed FeaturePython)
  Dunit = g/cm3
  Dvalue = 1.19
  Group = -> [H_element115,C_element125,O_element108]
  conduct = 2
  density = 1
  expand = 3
  formula = G4_LUCITE
  name = G4_LUCITE
  specific = 4
FEATURE [App::DocumentObjectGroupPython] Cu_element002  label="Cu_element : 62"  # scripted group (container) (typed FeaturePython)
  n = 62
  ref = Cu_element
FEATURE [App::DocumentObjectGroupPython] Zn_element002  label="Zn_element : 35"  # scripted group (container) (typed FeaturePython)
  n = 35
  ref = Zn_element
FEATURE [App::DocumentObjectGroupPython] Pb_element005  label="Pb_element : 3"  # scripted group (container) (typed FeaturePython)
  n = 3
  ref = Pb_element
FEATURE [App::DocumentObjectGroupPython] G4_BRASS  # scripted group (container) (typed FeaturePython)
  Dunit = g/cm3
  Dvalue = 8.52
  Group = -> [Cu_element002,Zn_element002,Pb_element005]
  conduct = 2
  density = 1
  expand = 3
  formula = G4_BRASS
  name = G4_BRASS
  specific = 4
FEATURE [App::DocumentObjectGroupPython] Cu_element003  label="Cu_element : 89"  # scripted group (container) (typed FeaturePython)
  n = 89
  ref = Cu_element
FEATURE [App::DocumentObjectGroupPython] Zn_element003  label="Zn_element : 9"  # scripted group (container) (typed FeaturePython)
  n = 9
  ref = Zn_element
FEATURE [App::DocumentObjectGroupPython] Pb_element006  label="Pb_element : 2"  # scripted group (container) (typed FeaturePython)
  n = 2
  ref = Pb_element
FEATURE [App::DocumentObjectGroupPython] G4_BRONZE  # scripted group (container) (typed FeaturePython)
  Dunit = g/cm3
  Dvalue = 8.82
  Group = -> [Cu_element003,Zn_element003,Pb_element006]
  conduct = 2
  density = 1
  expand = 3
  formula = G4_BRONZE
  name = G4_BRONZE
  specific = 4
FEATURE [App::DocumentObjectGroupPython] Fe_element008  label="Fe_element : 74"  # scripted group (container) (typed FeaturePython)
  n = 74
  ref = Fe_element
FEATURE [App::DocumentObjectGroupPython] Cr_element002  label="Cr_element : 18"  # scripted group (container) (typed FeaturePython)
  n = 18
  ref = Cr_element
FEATURE [App::DocumentObjectGroupPython] Ni_element002  label="Ni_element : 8"  # scripted group (container) (typed FeaturePython)
  n = 8
  ref = Ni_element
FEATURE [App::DocumentObjectGroupPython] G4_STAINLESS_STEEL  label="G4_STAINLESS-STEEL"  # scripted group (container) (typed FeaturePython)
  Dunit = g/cm3
  Dvalue = 8
  Group = -> [Fe_element008,Cr_element002,Ni_element002]
  conduct = 2
  density = 1
  expand = 3
  formula = G4_STAINLESS-STEEL
  name = G4_STAINLESS-STEEL
  specific = 4
FEATURE [App::DocumentObjectGroupPython] H_element116  label="H_element : 064"  # scripted group (container) (typed FeaturePython)
  n = 18
  ref = H_element
FEATURE [App::DocumentObjectGroupPython] C_element126  label="C_element : 071"  # scripted group (container) (typed FeaturePython)
  n = 12
  ref = C_element
FEATURE [App::DocumentObjectGroupPython] O_element109  label="O_element : 062"  # scripted group (container) (typed FeaturePython)
  n = 7
  ref = O_element
FEATURE [App::DocumentObjectGroupPython] G4_CR39  # scripted group (container) (typed FeaturePython)
  Dunit = g/cm3
  Dvalue = 1.32
  Group = -> [H_element116,C_element126,O_element109]
  conduct = 2
  density = 1
  expand = 3
  formula = G4_CR39
  name = G4_CR39
  specific = 4
FEATURE [App::DocumentObjectGroupPython] H_element117  label="H_element : 38"  # scripted group (container) (typed FeaturePython)
  n = 38
  ref = H_element
FEATURE [App::DocumentObjectGroupPython] C_element127  label="C_element : 072"  # scripted group (container) (typed FeaturePython)
  n = 18
  ref = C_element
FEATURE [App::DocumentObjectGroupPython] O_element110  label="O_element : 063"  # scripted group (container) (typed FeaturePython)
  n = 1
  ref = O_element
FEATURE [App::DocumentObjectGroupPython] G4_OCTADECANOL  # scripted group (container) (typed FeaturePython)
  Dunit = g/cm3
  Dvalue = 0.812
  Group = -> [H_element117,C_element127,O_element110]
  conduct = 2
  density = 1
  expand = 3
  formula = G4_OCTADECANOL
  name = G4_OCTADECANOL
  specific = 4
FEATURE [App::DocumentObjectGroupPython] HEP  # scripted group (container) (typed FeaturePython)
  Group = -> [G4_lH2,G4_lN2,G4_lO2,G4_lAr,G4_lBr,G4_lKr,G4_lXe,G4_PbWO4,G4_Galactic,G4_GRAPHITE_POROUS,G4_LUCITE,G4_BRASS,G4_BRONZE,G4_STAINLESS_STEEL,G4_CR39,G4_OCTADECANOL]
FEATURE [App::DocumentObjectGroupPython] C_element128  label="C_element : 073"  # scripted group (container) (typed FeaturePython)
  n = 14
  ref = C_element
FEATURE [App::DocumentObjectGroupPython] H_element118  label="H_element : 065"  # scripted group (container) (typed FeaturePython)
  n = 10
  ref = H_element
FEATURE [App::DocumentObjectGroupPython] O_element111  label="O_element : 064"  # scripted group (container) (typed FeaturePython)
  n = 2
  ref = O_element
FEATURE [App::DocumentObjectGroupPython] N_element050  label="N_element : 023"  # scripted group (container) (typed FeaturePython)
  n = 2
  ref = N_element
FEATURE [App::DocumentObjectGroupPython] G4_KEVLAR  # scripted group (container) (typed FeaturePython)
  Dunit = g/cm3
  Dvalue = 1.44
  Group = -> [C_element128,H_element118,O_element111,N_element050]
  conduct = 2
  density = 1
  expand = 3
  formula = G4_KEVLAR
  name = G4_KEVLAR
  specific = 4
FEATURE [App::DocumentObjectGroupPython] C_element129  label="C_element : 074"  # scripted group (container) (typed FeaturePython)
  n = 10
  ref = C_element
FEATURE [App::DocumentObjectGroupPython] H_element119  label="H_element : 066"  # scripted group (container) (typed FeaturePython)
  n = 8
  ref = H_element
FEATURE [App::DocumentObjectGroupPython] O_element112  label="O_element : 065"  # scripted group (container) (typed FeaturePython)
  n = 4
  ref = O_element
FEATURE [App::DocumentObjectGroupPython] G4_DACRON  # scripted group (container) (typed FeaturePython)
  Dunit = g/cm3
  Dvalue = 1.4
  Group = -> [C_element129,H_element119,O_element112]
  conduct = 2
  density = 1
  expand = 3
  formula = G4_DACRON
  name = G4_DACRON
  specific = 4
FEATURE [App::DocumentObjectGroupPython] C_element130  label="C_element : 075"  # scripted group (container) (typed FeaturePython)
  n = 4
  ref = C_element
FEATURE [App::DocumentObjectGroupPython] H_element120  label="H_element : 067"  # scripted group (container) (typed FeaturePython)
  n = 5
  ref = H_element
FEATURE [App::DocumentObjectGroupPython] Cl_element030  label="Cl_element : 016"  # scripted group (container) (typed FeaturePython)
  n = 1
  ref = Cl_element
FEATURE [App::DocumentObjectGroupPython] G4_NEOPRENE  # scripted group (container) (typed FeaturePython)
  Dunit = g/cm3
  Dvalue = 1.23
  Group = -> [C_element130,H_element120,Cl_element030]
  conduct = 2
  density = 1
  expand = 3
  formula = G4_NEOPRENE
  name = G4_NEOPRENE
  specific = 4
FEATURE [App::DocumentObjectGroupPython] Space  # scripted group (container) (typed FeaturePython)
  Group = -> [G4_KEVLAR,G4_DACRON,G4_NEOPRENE]
FEATURE [App::DocumentObjectGroupPython] H_element121  label="H_element : 068"  # scripted group (container) (typed FeaturePython)
  n = 5
  ref = H_element
FEATURE [App::DocumentObjectGroupPython] C_element131  label="C_element : 076"  # scripted group (container) (typed FeaturePython)
  n = 4
  ref = C_element
FEATURE [App::DocumentObjectGroupPython] N_element051  label="N_element : 3"  # scripted group (container) (typed FeaturePython)
  n = 3
  ref = N_element
FEATURE [App::DocumentObjectGroupPython] O_element113  label="O_element : 066"  # scripted group (container) (typed FeaturePython)
  n = 1
  ref = O_element
FEATURE [App::DocumentObjectGroupPython] G4_CYTOSINE  # scripted group (container) (typed FeaturePython)
  Dunit = g/cm3
  Dvalue = 1.55
  Group = -> [H_element121,C_element131,N_element051,O_element113]
  conduct = 2
  density = 1
  expand = 3
  formula = G4_CYTOSINE
  name = G4_CYTOSINE
  specific = 4
FEATURE [App::DocumentObjectGroupPython] H_element122  label="H_element : 069"  # scripted group (container) (typed FeaturePython)
  n = 6
  ref = H_element
FEATURE [App::DocumentObjectGroupPython] C_element132  label="C_element : 077"  # scripted group (container) (typed FeaturePython)
  n = 5
  ref = C_element
FEATURE [App::DocumentObjectGroupPython] N_element052  label="N_element : 024"  # scripted group (container) (typed FeaturePython)
  n = 2
  ref = N_element
FEATURE [App::DocumentObjectGroupPython] O_element114  label="O_element : 067"  # scripted group (container) (typed FeaturePython)
  n = 2
  ref = O_element
FEATURE [App::DocumentObjectGroupPython] G4_THYMINE  # scripted group (container) (typed FeaturePython)
  Dunit = g/cm3
  Dvalue = 1.23
  Group = -> [H_element122,C_element132,N_element052,O_element114]
  conduct = 2
  density = 1
  expand = 3
  formula = G4_THYMINE
  name = G4_THYMINE
  specific = 4
FEATURE [App::DocumentObjectGroupPython] H_element123  label="H_element : 070"  # scripted group (container) (typed FeaturePython)
  n = 4
  ref = H_element
FEATURE [App::DocumentObjectGroupPython] C_element133  label="C_element : 078"  # scripted group (container) (typed FeaturePython)
  n = 4
  ref = C_element
FEATURE [App::DocumentObjectGroupPython] N_element053  label="N_element : 025"  # scripted group (container) (typed FeaturePython)
  n = 2
  ref = N_element
FEATURE [App::DocumentObjectGroupPython] O_element115  label="O_element : 068"  # scripted group (container) (typed FeaturePython)
  n = 2
  ref = O_element
FEATURE [App::DocumentObjectGroupPython] G4_URACIL  # scripted group (container) (typed FeaturePython)
  Dunit = g/cm3
  Dvalue = 1.32
  Group = -> [H_element123,C_element133,N_element053,O_element115]
  conduct = 2
  density = 1
  expand = 3
  formula = G4_URACIL
  name = G4_URACIL
  specific = 4
FEATURE [App::DocumentObjectGroupPython] H_element124  label="H_element : 071"  # scripted group (container) (typed FeaturePython)
  n = 4
  ref = H_element
FEATURE [App::DocumentObjectGroupPython] C_element134  label="C_element : 079"  # scripted group (container) (typed FeaturePython)
  n = 5
  ref = C_element
FEATURE [App::DocumentObjectGroupPython] N_element054  label="N_element : 026"  # scripted group (container) (typed FeaturePython)
  n = 5
  ref = N_element
FEATURE [App::DocumentObjectGroupPython] G4_DNA_ADENINE  # scripted group (container) (typed FeaturePython)
  Dunit = g/cm3
  Dvalue = 1
  Group = -> [H_element124,C_element134,N_element054]
  conduct = 2
  density = 1
  expand = 3
  formula = G4_DNA_ADENINE
  name = G4_DNA_ADENINE
  specific = 4
FEATURE [App::DocumentObjectGroupPython] H_element125  label="H_element : 072"  # scripted group (container) (typed FeaturePython)
  n = 4
  ref = H_element
FEATURE [App::DocumentObjectGroupPython] C_element135  label="C_element : 080"  # scripted group (container) (typed FeaturePython)
  n = 5
  ref = C_element
FEATURE [App::DocumentObjectGroupPython] N_element055  label="N_element : 027"  # scripted group (container) (typed FeaturePython)
  n = 5
  ref = N_element
FEATURE [App::DocumentObjectGroupPython] O_element116  label="O_element : 069"  # scripted group (container) (typed FeaturePython)
  n = 1
  ref = O_element
FEATURE [App::DocumentObjectGroupPython] G4_DNA_GUANINE  # scripted group (container) (typed FeaturePython)
  Dunit = g/cm3
  Dvalue = 1
  Group = -> [H_element125,C_element135,N_element055,O_element116]
  conduct = 2
  density = 1
  expand = 3
  formula = G4_DNA_GUANINE
  name = G4_DNA_GUANINE
  specific = 4
FEATURE [App::DocumentObjectGroupPython] H_element126  label="H_element : 073"  # scripted group (container) (typed FeaturePython)
  n = 4
  ref = H_element
FEATURE [App::DocumentObjectGroupPython] C_element136  label="C_element : 081"  # scripted group (container) (typed FeaturePython)
  n = 4
  ref = C_element
FEATURE [App::DocumentObjectGroupPython] N_element056  label="N_element : 028"  # scripted group (container) (typed FeaturePython)
  n = 3
  ref = N_element
FEATURE [App::DocumentObjectGroupPython] O_element117  label="O_element : 070"  # scripted group (container) (typed FeaturePython)
  n = 1
  ref = O_element
FEATURE [App::DocumentObjectGroupPython] G4_DNA_CYTOSINE  # scripted group (container) (typed FeaturePython)
  Dunit = g/cm3
  Dvalue = 1
  Group = -> [H_element126,C_element136,N_element056,O_element117]
  conduct = 2
  density = 1
  expand = 3
  formula = G4_DNA_CYTOSINE
  name = G4_DNA_CYTOSINE
  specific = 4
FEATURE [App::DocumentObjectGroupPython] H_element127  label="H_element : 074"  # scripted group (container) (typed FeaturePython)
  n = 5
  ref = H_element
FEATURE [App::DocumentObjectGroupPython] C_element137  label="C_element : 082"  # scripted group (container) (typed FeaturePython)
  n = 5
  ref = C_element
FEATURE [App::DocumentObjectGroupPython] N_element057  label="N_element : 029"  # scripted group (container) (typed FeaturePython)
  n = 2
  ref = N_element
FEATURE [App::DocumentObjectGroupPython] O_element118  label="O_element : 071"  # scripted group (container) (typed FeaturePython)
  n = 2
  ref = O_element
FEATURE [App::DocumentObjectGroupPython] G4_DNA_THYMINE  # scripted group (container) (typed FeaturePython)
  Dunit = g/cm3
  Dvalue = 1
  Group = -> [H_element127,C_element137,N_element057,O_element118]
  conduct = 2
  density = 1
  expand = 3
  formula = G4_DNA_THYMINE
  name = G4_DNA_THYMINE
  specific = 4
FEATURE [App::DocumentObjectGroupPython] H_element128  label="H_element : 075"  # scripted group (container) (typed FeaturePython)
  n = 3
  ref = H_element
FEATURE [App::DocumentObjectGroupPython] C_element138  label="C_element : 083"  # scripted group (container) (typed FeaturePython)
  n = 4
  ref = C_element
FEATURE [App::DocumentObjectGroupPython] N_element058  label="N_element : 030"  # scripted group (container) (typed FeaturePython)
  n = 2
  ref = N_element
FEATURE [App::DocumentObjectGroupPython] O_element119  label="O_element : 072"  # scripted group (container) (typed FeaturePython)
  n = 2
  ref = O_element
FEATURE [App::DocumentObjectGroupPython] G4_DNA_URACIL  # scripted group (container) (typed FeaturePython)
  Dunit = g/cm3
  Dvalue = 1
  Group = -> [H_element128,C_element138,N_element058,O_element119]
  conduct = 2
  density = 1
  expand = 3
  formula = G4_DNA_URACIL
  name = G4_DNA_URACIL
  specific = 4
FEATURE [App::DocumentObjectGroupPython] H_element129  label="H_element : 076"  # scripted group (container) (typed FeaturePython)
  n = 10
  ref = H_element
FEATURE [App::DocumentObjectGroupPython] C_element139  label="C_element : 084"  # scripted group (container) (typed FeaturePython)
  n = 10
  ref = C_element
FEATURE [App::DocumentObjectGroupPython] N_element059  label="N_element : 031"  # scripted group (container) (typed FeaturePython)
  n = 5
  ref = N_element
FEATURE [App::DocumentObjectGroupPython] O_element120  label="O_element : 073"  # scripted group (container) (typed FeaturePython)
  n = 4
  ref = O_element
FEATURE [App::DocumentObjectGroupPython] G4_DNA_ADENOSINE  # scripted group (container) (typed FeaturePython)
  Dunit = g/cm3
  Dvalue = 1
  Group = -> [H_element129,C_element139,N_element059,O_element120]
  conduct = 2
  density = 1
  expand = 3
  formula = G4_DNA_ADENOSINE
  name = G4_DNA_ADENOSINE
  specific = 4
FEATURE [App::DocumentObjectGroupPython] H_element130  label="H_element : 077"  # scripted group (container) (typed FeaturePython)
  n = 10
  ref = H_element
FEATURE [App::DocumentObjectGroupPython] C_element140  label="C_element : 085"  # scripted group (container) (typed FeaturePython)
  n = 10
  ref = C_element
FEATURE [App::DocumentObjectGroupPython] N_element060  label="N_element : 032"  # scripted group (container) (typed FeaturePython)
  n = 5
  ref = N_element
FEATURE [App::DocumentObjectGroupPython] O_element121  label="O_element : 074"  # scripted group (container) (typed FeaturePython)
  n = 5
  ref = O_element
FEATURE [App::DocumentObjectGroupPython] G4_DNA_GUANOSINE  # scripted group (container) (typed FeaturePython)
  Dunit = g/cm3
  Dvalue = 1
  Group = -> [H_element130,C_element140,N_element060,O_element121]
  conduct = 2
  density = 1
  expand = 3
  formula = G4_DNA_GUANOSINE
  name = G4_DNA_GUANOSINE
  specific = 4
FEATURE [App::DocumentObjectGroupPython] H_element131  label="H_element : 078"  # scripted group (container) (typed FeaturePython)
  n = 10
  ref = H_element
FEATURE [App::DocumentObjectGroupPython] C_element141  label="C_element : 086"  # scripted group (container) (typed FeaturePython)
  n = 9
  ref = C_element
FEATURE [App::DocumentObjectGroupPython] N_element061  label="N_element : 033"  # scripted group (container) (typed FeaturePython)
  n = 3
  ref = N_element
FEATURE [App::DocumentObjectGroupPython] O_element122  label="O_element : 075"  # scripted group (container) (typed FeaturePython)
  n = 5
  ref = O_element
FEATURE [App::DocumentObjectGroupPython] G4_DNA_CYTIDINE  # scripted group (container) (typed FeaturePython)
  Dunit = g/cm3
  Dvalue = 1
  Group = -> [H_element131,C_element141,N_element061,O_element122]
  conduct = 2
  density = 1
  expand = 3
  formula = G4_DNA_CYTIDINE
  name = G4_DNA_CYTIDINE
  specific = 4
FEATURE [App::DocumentObjectGroupPython] H_element132  label="H_element : 079"  # scripted group (container) (typed FeaturePython)
  n = 9
  ref = H_element
FEATURE [App::DocumentObjectGroupPython] C_element142  label="C_element : 087"  # scripted group (container) (typed FeaturePython)
  n = 9
  ref = C_element
FEATURE [App::DocumentObjectGroupPython] N_element062  label="N_element : 034"  # scripted group (container) (typed FeaturePython)
  n = 2
  ref = N_element
FEATURE [App::DocumentObjectGroupPython] O_element123  label="O_element : 076"  # scripted group (container) (typed FeaturePython)
  n = 6
  ref = O_element
FEATURE [App::DocumentObjectGroupPython] G4_DNA_URIDINE  # scripted group (container) (typed FeaturePython)
  Dunit = g/cm3
  Dvalue = 1
  Group = -> [H_element132,C_element142,N_element062,O_element123]
  conduct = 2
  density = 1
  expand = 3
  formula = G4_DNA_URIDINE
  name = G4_DNA_URIDINE
  specific = 4
FEATURE [App::DocumentObjectGroupPython] H_element133  label="H_element : 080"  # scripted group (container) (typed FeaturePython)
  n = 11
  ref = H_element
FEATURE [App::DocumentObjectGroupPython] C_element143  label="C_element : 088"  # scripted group (container) (typed FeaturePython)
  n = 10
  ref = C_element
FEATURE [App::DocumentObjectGroupPython] N_element063  label="N_element : 035"  # scripted group (container) (typed FeaturePython)
  n = 2
  ref = N_element
FEATURE [App::DocumentObjectGroupPython] O_element124  label="O_element : 077"  # scripted group (container) (typed FeaturePython)
  n = 6
  ref = O_element
FEATURE [App::DocumentObjectGroupPython] G4_DNA_METHYLURIDINE  # scripted group (container) (typed FeaturePython)
  Dunit = g/cm3
  Dvalue = 1
  Group = -> [H_element133,C_element143,N_element063,O_element124]
  conduct = 2
  density = 1
  expand = 3
  formula = G4_DNA_METHYLURIDINE
  name = G4_DNA_METHYLURIDINE
  specific = 4
FEATURE [App::DocumentObjectGroupPython] P_element014  label="P_element : 003"  # scripted group (container) (typed FeaturePython)
  n = 1
  ref = P_element
FEATURE [App::DocumentObjectGroupPython] O_element125  label="O_element : 078"  # scripted group (container) (typed FeaturePython)
  n = 3
  ref = O_element
FEATURE [App::DocumentObjectGroupPython] G4_DNA_MONOPHOSPHATE  # scripted group (container) (typed FeaturePython)
  Dunit = g/cm3
  Dvalue = 1
  Group = -> [P_element014,O_element125]
  conduct = 2
  density = 1
  expand = 3
  formula = G4_DNA_MONOPHOSPHATE
  name = G4_DNA_MONOPHOSPHATE
  specific = 4
FEATURE [App::DocumentObjectGroupPython] H_element134  label="H_element : 081"  # scripted group (container) (typed FeaturePython)
  n = 10
  ref = H_element
FEATURE [App::DocumentObjectGroupPython] C_element144  label="C_element : 089"  # scripted group (container) (typed FeaturePython)
  n = 10
  ref = C_element
FEATURE [App::DocumentObjectGroupPython] N_element064  label="N_element : 036"  # scripted group (container) (typed FeaturePython)
  n = 5
  ref = N_element
FEATURE [App::DocumentObjectGroupPython] O_element126  label="O_element : 079"  # scripted group (container) (typed FeaturePython)
  n = 7
  ref = O_element
FEATURE [App::DocumentObjectGroupPython] P_element015  label="P_element : 004"  # scripted group (container) (typed FeaturePython)
  n = 1
  ref = P_element
FEATURE [App::DocumentObjectGroupPython] G4_DNA_A  # scripted group (container) (typed FeaturePython)
  Dunit = g/cm3
  Dvalue = 1
  Group = -> [H_element134,C_element144,N_element064,O_element126,P_element015]
  conduct = 2
  density = 1
  expand = 3
  formula = G4_DNA_A
  name = G4_DNA_A
  specific = 4
FEATURE [App::DocumentObjectGroupPython] H_element135  label="H_element : 082"  # scripted group (container) (typed FeaturePython)
  n = 10
  ref = H_element
FEATURE [App::DocumentObjectGroupPython] C_element145  label="C_element : 090"  # scripted group (container) (typed FeaturePython)
  n = 10
  ref = C_element
FEATURE [App::DocumentObjectGroupPython] N_element065  label="N_element : 037"  # scripted group (container) (typed FeaturePython)
  n = 5
  ref = N_element
FEATURE [App::DocumentObjectGroupPython] O_element127  label="O_element : 8"  # scripted group (container) (typed FeaturePython)
  n = 8
  ref = O_element
FEATURE [App::DocumentObjectGroupPython] P_element016  label="P_element : 005"  # scripted group (container) (typed FeaturePython)
  n = 1
  ref = P_element
FEATURE [App::DocumentObjectGroupPython] G4_DNA_G  # scripted group (container) (typed FeaturePython)
  Dunit = g/cm3
  Dvalue = 1
  Group = -> [H_element135,C_element145,N_element065,O_element127,P_element016]
  conduct = 2
  density = 1
  expand = 3
  formula = G4_DNA_G
  name = G4_DNA_G
  specific = 4
FEATURE [App::DocumentObjectGroupPython] H_element136  label="H_element : 083"  # scripted group (container) (typed FeaturePython)
  n = 10
  ref = H_element
FEATURE [App::DocumentObjectGroupPython] C_element146  label="C_element : 091"  # scripted group (container) (typed FeaturePython)
  n = 9
  ref = C_element
FEATURE [App::DocumentObjectGroupPython] N_element066  label="N_element : 038"  # scripted group (container) (typed FeaturePython)
  n = 3
  ref = N_element
FEATURE [App::DocumentObjectGroupPython] O_element128  label="O_element : 080"  # scripted group (container) (typed FeaturePython)
  n = 8
  ref = O_element
FEATURE [App::DocumentObjectGroupPython] P_element017  label="P_element : 006"  # scripted group (container) (typed FeaturePython)
  n = 1
  ref = P_element
FEATURE [App::DocumentObjectGroupPython] G4_DNA_C  # scripted group (container) (typed FeaturePython)
  Dunit = g/cm3
  Dvalue = 1
  Group = -> [H_element136,C_element146,N_element066,O_element128,P_element017]
  conduct = 2
  density = 1
  expand = 3
  formula = G4_DNA_C
  name = G4_DNA_C
  specific = 4
FEATURE [App::DocumentObjectGroupPython] H_element137  label="H_element : 084"  # scripted group (container) (typed FeaturePython)
  n = 9
  ref = H_element
FEATURE [App::DocumentObjectGroupPython] C_element147  label="C_element : 092"  # scripted group (container) (typed FeaturePython)
  n = 9
  ref = C_element
FEATURE [App::DocumentObjectGroupPython] N_element067  label="N_element : 039"  # scripted group (container) (typed FeaturePython)
  n = 2
  ref = N_element
FEATURE [App::DocumentObjectGroupPython] O_element129  label="O_element : 9"  # scripted group (container) (typed FeaturePython)
  n = 9
  ref = O_element
FEATURE [App::DocumentObjectGroupPython] P_element018  label="P_element : 007"  # scripted group (container) (typed FeaturePython)
  n = 1
  ref = P_element
FEATURE [App::DocumentObjectGroupPython] G4_DNA_U  # scripted group (container) (typed FeaturePython)
  Dunit = g/cm3
  Dvalue = 1
  Group = -> [H_element137,C_element147,N_element067,O_element129,P_element018]
  conduct = 2
  density = 1
  expand = 3
  formula = G4_DNA_U
  name = G4_DNA_U
  specific = 4
FEATURE [App::DocumentObjectGroupPython] H_element138  label="H_element : 085"  # scripted group (container) (typed FeaturePython)
  n = 11
  ref = H_element
FEATURE [App::DocumentObjectGroupPython] C_element148  label="C_element : 093"  # scripted group (container) (typed FeaturePython)
  n = 10
  ref = C_element
FEATURE [App::DocumentObjectGroupPython] N_element068  label="N_element : 040"  # scripted group (container) (typed FeaturePython)
  n = 2
  ref = N_element
FEATURE [App::DocumentObjectGroupPython] O_element130  label="O_element : 081"  # scripted group (container) (typed FeaturePython)
  n = 9
  ref = O_element
FEATURE [App::DocumentObjectGroupPython] P_element019  label="P_element : 008"  # scripted group (container) (typed FeaturePython)
  n = 1
  ref = P_element
FEATURE [App::DocumentObjectGroupPython] G4_DNA_MU  # scripted group (container) (typed FeaturePython)
  Dunit = g/cm3
  Dvalue = 1
  Group = -> [H_element138,C_element148,N_element068,O_element130,P_element019]
  conduct = 2
  density = 1
  expand = 3
  formula = G4_DNA_MU
  name = G4_DNA_MU
  specific = 4
FEATURE [App::DocumentObjectGroupPython] BioChemical  # scripted group (container) (typed FeaturePython)
  Group = -> [G4_CYTOSINE,G4_THYMINE,G4_URACIL,G4_DNA_ADENINE,G4_DNA_GUANINE,G4_DNA_CYTOSINE,G4_DNA_THYMINE,G4_DNA_URACIL,G4_DNA_ADENOSINE,G4_DNA_GUANOSINE,G4_DNA_CYTIDINE,G4_DNA_URIDINE,G4_DNA_METHYLURIDINE,G4_DNA_MONOPHOSPHATE,G4_DNA_A,G4_DNA_G,G4_DNA_C,G4_DNA_U,G4_DNA_MU]
FEATURE [App::DocumentObjectGroupPython] G4Materials  # scripted group (container) (typed FeaturePython)
  Group = -> [NIST,Element,HEP,Space,BioChemical]
  version = 1
FEATURE [App::DocumentObjectGroupPython] Geant4  # scripted group (container) (typed FeaturePython)
  Group = -> [G4Isotopes,G4Elements,G4Materials]
FEATURE [App::DocumentObjectGroupPython] Materials  # scripted group (container) (typed FeaturePython)
  Group = -> [Geant4]
FEATURE [Part::FeaturePython] GDMLBox_WorldBox  # WARN: FeaturePython — macro-defined, semantics opaque (R4)
  lunit = 2
  material = 5
  x = 273
  y = 273
  z = 130
FEATURE [Part::FeaturePython] GDMLBox_Box  # WARN: FeaturePython — macro-defined, semantics opaque (R4)
  Placement = pos=(20,0,0) rot=(0,0,1;0rad)
  lunit = 2
  material = 0
  x = 10
  y = 10
  z = 10
FEATURE [Part::FeaturePython] GDMLTube  # WARN: FeaturePython — macro-defined, semantics opaque (R4)
  Placement = pos=(17,-4,0) rot=(0,0,1;0rad)
  aunit = 1
  deltaphi = 90
  lunit = 2
  material = 0
  rmax = 7
  rmin = 5
  startphi = 0
  z = 7
FEATURE [App::Part] LV_Tube
  Group = -> [GDMLTube]
  Origin = -> Origin003
  SkinSurface = 0
FEATURE [App::Part] LV_Box
  Group = -> [GDMLBox_Box,LV_Tube]
  Origin = -> Origin002
FEATURE [Part::FeaturePython] Array  # Draft array (typed FeaturePython)
  AlwaysSyncPlacement = false
  Angle = 180
  ArrayType = 1
  Axis = (0,0,1)
  Base = -> LV_Box
  Center = (0,0,0)
  Count = 5
  ExpandArray = false
  Fuse = false
  IntervalAxis = (0,0,0)
  IntervalX = (100,0,0)
  IntervalY = (0,100,0)
  IntervalZ = (0,0,100)
  NumberCircles = 3
  NumberPolar = 5
  NumberX = 2
  NumberY = 2
  NumberZ = 1
  PlacementList = 5 placements: [(0,0,0),(0,0,0),(0,0,0),(0,0,0),(0,0,0)]
  RadialDistance = 50
  ScaleList = (5) [(1,1,1),(1,1,1),(1,1,1),(1,1,1),(1,1,1)]
  Symmetry = 1
  TangentialDistance = 25
FEATURE [App::Part] Part  label="experiment"
  Group = -> [LV_Box,Array]
  Origin = -> Origin001
FEATURE [App::Part] worldVOL
  Group = -> [GDMLBox_WorldBox,Part]
  Origin = -> Origin
